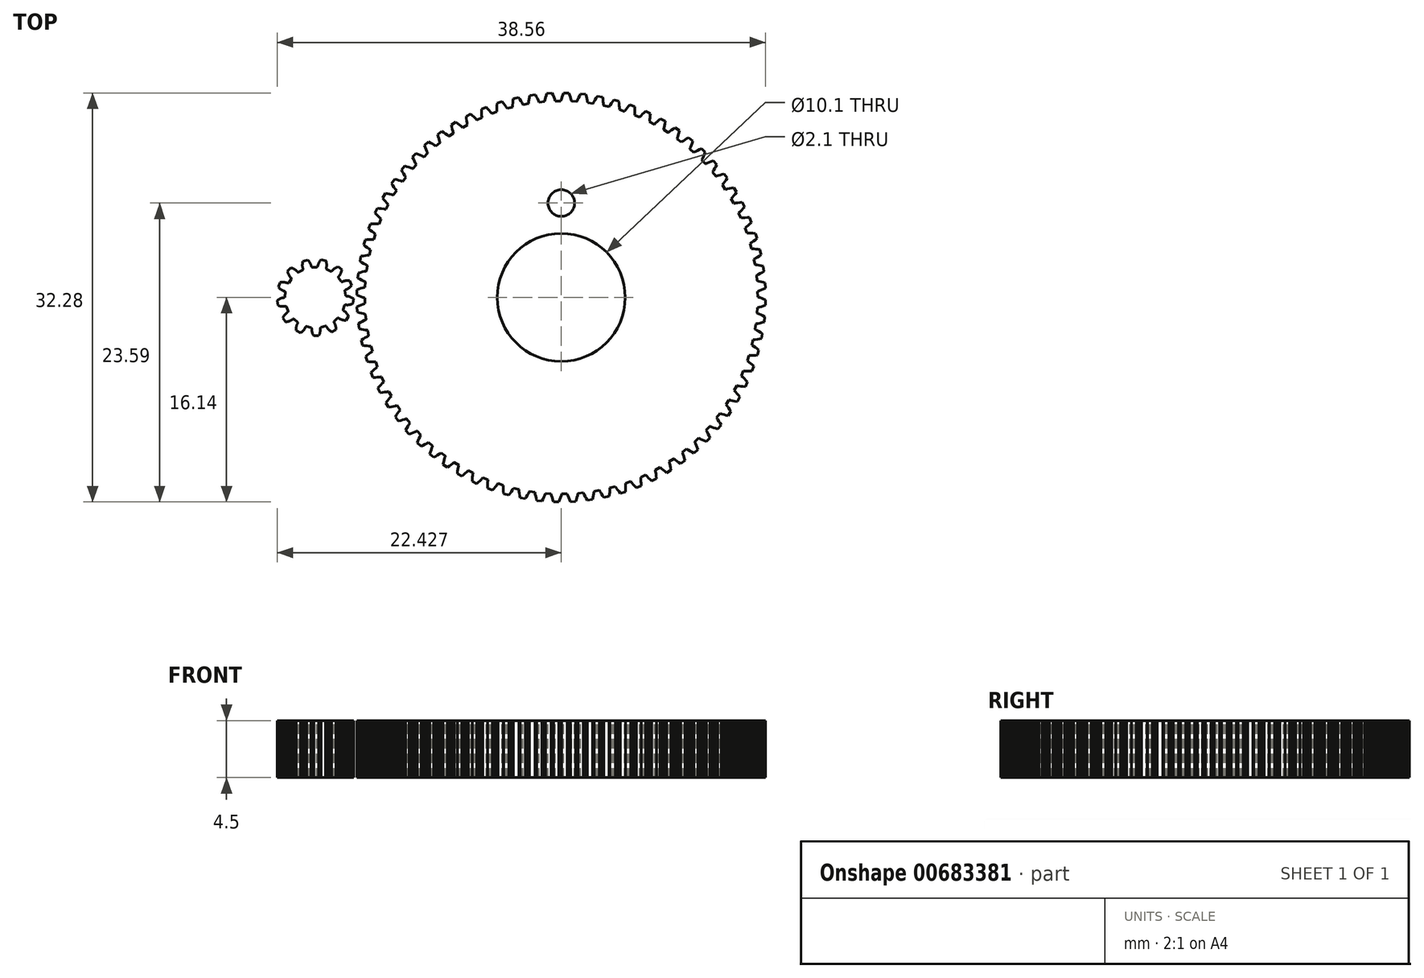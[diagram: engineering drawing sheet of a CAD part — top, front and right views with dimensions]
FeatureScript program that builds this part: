
annotation { "Feature Type Name" : "Feature", "Feature Type Description" : "" }
export const myFeature = defineFeature(function(context is Context, id is Id, definition is map)
    precondition{}
    {
        {
            var Q0;
            Q0=qCreatedBy(makeId("Top.planeOp"),FACE);
            var sketch = newSketch(context, id + "F0", { "sketchPlane" : qUnion([Q0])});
            skLineSegment(sketch, "E0", {"start": v(-13.88, 0.17) * mm, "end": v(-13.87, 0.14) * mm});
            skLineSegment(sketch, "E1", {"start": v(-13.87, 0.14) * mm, "end": v(-13.86, 0.13) * mm});
            skLineSegment(sketch, "E2", {"start": v(-13.86, 0.13) * mm, "end": v(-13.85, 0.12) * mm});
            skLineSegment(sketch, "E3", {"start": v(-13.85, 0.12) * mm, "end": v(-13.84, 0.12) * mm});
            skLineSegment(sketch, "E4", {"start": v(-13.84, 0.12) * mm, "end": v(-13.83, 0.11) * mm});
            skLineSegment(sketch, "E5", {"start": v(-13.83, 0.11) * mm, "end": v(-13.82, 0.1) * mm});
            skLineSegment(sketch, "E6", {"start": v(-13.82, 0.1) * mm, "end": v(-13.8, 0.1) * mm});
            skLineSegment(sketch, "E7", {"start": v(-13.8, 0.1) * mm, "end": v(-13.78, 0.1) * mm});
            skLineSegment(sketch, "E8", {"start": v(-13.78, 0.1) * mm, "end": v(-13.76, 0.1) * mm});
            skLineSegment(sketch, "E9", {"start": v(-13.76, 0.1) * mm, "end": v(-13.71, 0.1) * mm});
            skLineSegment(sketch, "E10", {"start": v(-13.71, 0.1) * mm, "end": v(-13.67, 0.1) * mm});
            skLineSegment(sketch, "E11", {"start": v(-13.67, 0.1) * mm, "end": v(-13.63, 0.08) * mm});
            skLineSegment(sketch, "E12", {"start": v(-13.63, 0.08) * mm, "end": v(-13.59, 0.07) * mm});
            skLineSegment(sketch, "E13", {"start": v(-13.59, 0.07) * mm, "end": v(-13.54, 0.06) * mm});
            skLineSegment(sketch, "E14", {"start": v(-13.54, 0.06) * mm, "end": v(-13.5, 0.04) * mm});
            skLineSegment(sketch, "E15", {"start": v(-13.5, 0.04) * mm, "end": v(-13.46, 0.02) * mm});
            skLineSegment(sketch, "E16", {"start": v(-13.46, 0.02) * mm, "end": v(-13.42, 0) * mm});
            skLineSegment(sketch, "E17", {"start": v(-13.42, 0) * mm, "end": v(-13.38, -0.02) * mm});
            skLineSegment(sketch, "E18", {"start": v(-13.38, -0.02) * mm, "end": v(-13.34, -0.04) * mm});
            skLineSegment(sketch, "E19", {"start": v(-13.34, -0.04) * mm, "end": v(-13.3, -0.07) * mm});
            skLineSegment(sketch, "E20", {"start": v(-13.3, -0.07) * mm, "end": v(-13.25, -0.1) * mm});
            skLineSegment(sketch, "E21", {"start": v(-13.25, -0.1) * mm, "end": v(-13.3, -0.49) * mm});
            skLineSegment(sketch, "E22", {"start": v(-13.3, -0.49) * mm, "end": v(-13.34, -0.5) * mm});
            skLineSegment(sketch, "E23", {"start": v(-13.34, -0.5) * mm, "end": v(-13.38, -0.52) * mm});
            skLineSegment(sketch, "E24", {"start": v(-13.38, -0.52) * mm, "end": v(-13.43, -0.54) * mm});
            skLineSegment(sketch, "E25", {"start": v(-13.43, -0.54) * mm, "end": v(-13.47, -0.55) * mm});
            skLineSegment(sketch, "E26", {"start": v(-13.47, -0.55) * mm, "end": v(-13.52, -0.56) * mm});
            skLineSegment(sketch, "E27", {"start": v(-13.52, -0.56) * mm, "end": v(-13.56, -0.57) * mm});
            skLineSegment(sketch, "E28", {"start": v(-13.56, -0.57) * mm, "end": v(-13.6, -0.58) * mm});
            skLineSegment(sketch, "E29", {"start": v(-13.6, -0.58) * mm, "end": v(-13.65, -0.59) * mm});
            skLineSegment(sketch, "E30", {"start": v(-13.65, -0.59) * mm, "end": v(-13.7, -0.6) * mm});
            skLineSegment(sketch, "E31", {"start": v(-13.7, -0.6) * mm, "end": v(-13.74, -0.6) * mm});
            skLineSegment(sketch, "E32", {"start": v(-13.74, -0.6) * mm, "end": v(-13.78, -0.59) * mm});
            skLineSegment(sketch, "E33", {"start": v(-13.78, -0.59) * mm, "end": v(-13.82, -0.58) * mm});
            skLineSegment(sketch, "E34", {"start": v(-13.82, -0.58) * mm, "end": v(-13.84, -0.58) * mm});
            skLineSegment(sketch, "E35", {"start": v(-13.84, -0.58) * mm, "end": v(-13.86, -0.58) * mm});
            skLineSegment(sketch, "E36", {"start": v(-13.86, -0.58) * mm, "end": v(-13.89, -0.58) * mm});
            skLineSegment(sketch, "E37", {"start": v(-13.89, -0.58) * mm, "end": v(-13.9, -0.58) * mm});
            skLineSegment(sketch, "E38", {"start": v(-13.9, -0.58) * mm, "end": v(-13.9, -0.58) * mm});
            skLineSegment(sketch, "E39", {"start": v(-13.9, -0.58) * mm, "end": v(-13.92, -0.59) * mm});
            skLineSegment(sketch, "E40", {"start": v(-13.92, -0.59) * mm, "end": v(-13.93, -0.6) * mm});
            skLineSegment(sketch, "E41", {"start": v(-13.93, -0.6) * mm, "end": v(-13.94, -0.6) * mm});
            skLineSegment(sketch, "E42", {"start": v(-13.94, -0.6) * mm, "end": v(-13.96, -0.62) * mm});
            skLineSegment(sketch, "E43", {"start": v(-13.96, -0.62) * mm, "end": v(-14.08, -0.96) * mm});
            skLineSegment(sketch, "E44", {"start": v(-14.08, -0.96) * mm, "end": v(-14.08, -1) * mm});
            skLineSegment(sketch, "E45", {"start": v(-14.08, -1) * mm, "end": v(-14.08, -1) * mm});
            skLineSegment(sketch, "E46", {"start": v(-14.08, -1) * mm, "end": v(-14.07, -1.02) * mm});
            skLineSegment(sketch, "E47", {"start": v(-14.07, -1.02) * mm, "end": v(-14.06, -1.03) * mm});
            skLineSegment(sketch, "E48", {"start": v(-14.06, -1.03) * mm, "end": v(-14.06, -1.03) * mm});
            skLineSegment(sketch, "E49", {"start": v(-14.06, -1.03) * mm, "end": v(-14.05, -1.04) * mm});
            skLineSegment(sketch, "E50", {"start": v(-14.05, -1.04) * mm, "end": v(-14.03, -1.06) * mm});
            skLineSegment(sketch, "E51", {"start": v(-14.03, -1.06) * mm, "end": v(-14.01, -1.07) * mm});
            skLineSegment(sketch, "E52", {"start": v(-14.01, -1.07) * mm, "end": v(-14, -1.08) * mm});
            skLineSegment(sketch, "E53", {"start": v(-14, -1.08) * mm, "end": v(-13.96, -1.1) * mm});
            skLineSegment(sketch, "E54", {"start": v(-13.96, -1.1) * mm, "end": v(-13.93, -1.13) * mm});
            skLineSegment(sketch, "E55", {"start": v(-13.93, -1.13) * mm, "end": v(-13.9, -1.15) * mm});
            skLineSegment(sketch, "E56", {"start": v(-13.9, -1.15) * mm, "end": v(-13.86, -1.18) * mm});
            skLineSegment(sketch, "E57", {"start": v(-13.86, -1.18) * mm, "end": v(-13.83, -1.22) * mm});
            skLineSegment(sketch, "E58", {"start": v(-13.83, -1.22) * mm, "end": v(-13.8, -1.25) * mm});
            skLineSegment(sketch, "E59", {"start": v(-13.8, -1.25) * mm, "end": v(-13.77, -1.29) * mm});
            skLineSegment(sketch, "E60", {"start": v(-13.77, -1.29) * mm, "end": v(-13.74, -1.32) * mm});
            skLineSegment(sketch, "E61", {"start": v(-13.74, -1.32) * mm, "end": v(-13.72, -1.36) * mm});
            skLineSegment(sketch, "E62", {"start": v(-13.72, -1.36) * mm, "end": v(-13.7, -1.4) * mm});
            skLineSegment(sketch, "E63", {"start": v(-13.7, -1.4) * mm, "end": v(-13.67, -1.44) * mm});
            skLineSegment(sketch, "E64", {"start": v(-13.67, -1.44) * mm, "end": v(-13.64, -1.49) * mm});
            skLineSegment(sketch, "E65", {"start": v(-13.64, -1.49) * mm, "end": v(-13.86, -1.82) * mm});
            skLineSegment(sketch, "E66", {"start": v(-13.86, -1.82) * mm, "end": v(-13.9, -1.81) * mm});
            skLineSegment(sketch, "E67", {"start": v(-13.9, -1.81) * mm, "end": v(-13.96, -1.8) * mm});
            skLineSegment(sketch, "E68", {"start": v(-13.96, -1.8) * mm, "end": v(-14, -1.8) * mm});
            skLineSegment(sketch, "E69", {"start": v(-14, -1.8) * mm, "end": v(-14.05, -1.79) * mm});
            skLineSegment(sketch, "E70", {"start": v(-14.05, -1.79) * mm, "end": v(-14.1, -1.78) * mm});
            skLineSegment(sketch, "E71", {"start": v(-14.1, -1.78) * mm, "end": v(-14.14, -1.77) * mm});
            skLineSegment(sketch, "E72", {"start": v(-14.14, -1.77) * mm, "end": v(-14.18, -1.75) * mm});
            skLineSegment(sketch, "E73", {"start": v(-14.18, -1.75) * mm, "end": v(-14.22, -1.74) * mm});
            skLineSegment(sketch, "E74", {"start": v(-14.22, -1.74) * mm, "end": v(-14.26, -1.72) * mm});
            skLineSegment(sketch, "E75", {"start": v(-14.26, -1.72) * mm, "end": v(-14.3, -1.7) * mm});
            skLineSegment(sketch, "E76", {"start": v(-14.3, -1.7) * mm, "end": v(-14.34, -1.68) * mm});
            skLineSegment(sketch, "E77", {"start": v(-14.34, -1.68) * mm, "end": v(-14.37, -1.65) * mm});
            skLineSegment(sketch, "E78", {"start": v(-14.37, -1.65) * mm, "end": v(-14.39, -1.64) * mm});
            skLineSegment(sketch, "E79", {"start": v(-14.39, -1.64) * mm, "end": v(-14.4, -1.63) * mm});
            skLineSegment(sketch, "E80", {"start": v(-14.4, -1.63) * mm, "end": v(-14.43, -1.62) * mm});
            skLineSegment(sketch, "E81", {"start": v(-14.43, -1.62) * mm, "end": v(-14.44, -1.62) * mm});
            skLineSegment(sketch, "E82", {"start": v(-14.44, -1.62) * mm, "end": v(-14.45, -1.61) * mm});
            skLineSegment(sketch, "E83", {"start": v(-14.45, -1.61) * mm, "end": v(-14.46, -1.61) * mm});
            skLineSegment(sketch, "E84", {"start": v(-14.46, -1.61) * mm, "end": v(-14.47, -1.61) * mm});
            skLineSegment(sketch, "E85", {"start": v(-14.47, -1.61) * mm, "end": v(-14.49, -1.61) * mm});
            skLineSegment(sketch, "E86", {"start": v(-14.49, -1.61) * mm, "end": v(-14.51, -1.62) * mm});
            skLineSegment(sketch, "E87", {"start": v(-14.51, -1.62) * mm, "end": v(-14.78, -1.87) * mm});
            skLineSegment(sketch, "E88", {"start": v(-14.78, -1.87) * mm, "end": v(-14.8, -1.9) * mm});
            skLineSegment(sketch, "E89", {"start": v(-14.8, -1.9) * mm, "end": v(-14.8, -1.9) * mm});
            skLineSegment(sketch, "E90", {"start": v(-14.8, -1.9) * mm, "end": v(-14.8, -1.92) * mm});
            skLineSegment(sketch, "E91", {"start": v(-14.8, -1.92) * mm, "end": v(-14.8, -1.93) * mm});
            skLineSegment(sketch, "E92", {"start": v(-14.8, -1.93) * mm, "end": v(-14.8, -1.95) * mm});
            skLineSegment(sketch, "E93", {"start": v(-14.8, -1.95) * mm, "end": v(-14.79, -1.96) * mm});
            skLineSegment(sketch, "E94", {"start": v(-14.79, -1.96) * mm, "end": v(-14.78, -1.98) * mm});
            skLineSegment(sketch, "E95", {"start": v(-14.78, -1.98) * mm, "end": v(-14.77, -2) * mm});
            skLineSegment(sketch, "E96", {"start": v(-14.77, -2) * mm, "end": v(-14.76, -2.01) * mm});
            skLineSegment(sketch, "E97", {"start": v(-14.76, -2.01) * mm, "end": v(-14.74, -2.05) * mm});
            skLineSegment(sketch, "E98", {"start": v(-14.74, -2.05) * mm, "end": v(-14.72, -2.09) * mm});
            skLineSegment(sketch, "E99", {"start": v(-14.72, -2.09) * mm, "end": v(-14.7, -2.13) * mm});
            skLineSegment(sketch, "E100", {"start": v(-14.7, -2.13) * mm, "end": v(-14.69, -2.17) * mm});
            skLineSegment(sketch, "E101", {"start": v(-14.69, -2.17) * mm, "end": v(-14.67, -2.21) * mm});
            skLineSegment(sketch, "E102", {"start": v(-14.67, -2.21) * mm, "end": v(-14.66, -2.26) * mm});
            skLineSegment(sketch, "E103", {"start": v(-14.66, -2.26) * mm, "end": v(-14.66, -2.3) * mm});
            skLineSegment(sketch, "E104", {"start": v(-14.66, -2.3) * mm, "end": v(-14.65, -2.35) * mm});
            skLineSegment(sketch, "E105", {"start": v(-14.65, -2.35) * mm, "end": v(-14.64, -2.4) * mm});
            skLineSegment(sketch, "E106", {"start": v(-14.64, -2.4) * mm, "end": v(-14.64, -2.44) * mm});
            skLineSegment(sketch, "E107", {"start": v(-14.64, -2.44) * mm, "end": v(-14.64, -2.49) * mm});
            skLineSegment(sketch, "E108", {"start": v(-14.64, -2.49) * mm, "end": v(-14.64, -2.54) * mm});
            skLineSegment(sketch, "E109", {"start": v(-14.64, -2.54) * mm, "end": v(-14.98, -2.73) * mm});
            skLineSegment(sketch, "E110", {"start": v(-14.98, -2.73) * mm, "end": v(-15.02, -2.7) * mm});
            skLineSegment(sketch, "E111", {"start": v(-15.02, -2.7) * mm, "end": v(-15.06, -2.67) * mm});
            skLineSegment(sketch, "E112", {"start": v(-15.06, -2.67) * mm, "end": v(-15.1, -2.65) * mm});
            skLineSegment(sketch, "E113", {"start": v(-15.1, -2.65) * mm, "end": v(-15.13, -2.62) * mm});
            skLineSegment(sketch, "E114", {"start": v(-15.13, -2.62) * mm, "end": v(-15.17, -2.59) * mm});
            skLineSegment(sketch, "E115", {"start": v(-15.17, -2.59) * mm, "end": v(-15.2, -2.56) * mm});
            skLineSegment(sketch, "E116", {"start": v(-15.2, -2.56) * mm, "end": v(-15.24, -2.52) * mm});
            skLineSegment(sketch, "E117", {"start": v(-15.24, -2.52) * mm, "end": v(-15.27, -2.5) * mm});
            skLineSegment(sketch, "E118", {"start": v(-15.27, -2.5) * mm, "end": v(-15.3, -2.46) * mm});
            skLineSegment(sketch, "E119", {"start": v(-15.3, -2.46) * mm, "end": v(-15.32, -2.42) * mm});
            skLineSegment(sketch, "E120", {"start": v(-15.32, -2.42) * mm, "end": v(-15.34, -2.38) * mm});
            skLineSegment(sketch, "E121", {"start": v(-15.34, -2.38) * mm, "end": v(-15.36, -2.35) * mm});
            skLineSegment(sketch, "E122", {"start": v(-15.36, -2.35) * mm, "end": v(-15.37, -2.33) * mm});
            skLineSegment(sketch, "E123", {"start": v(-15.37, -2.33) * mm, "end": v(-15.38, -2.31) * mm});
            skLineSegment(sketch, "E124", {"start": v(-15.38, -2.31) * mm, "end": v(-15.4, -2.3) * mm});
            skLineSegment(sketch, "E125", {"start": v(-15.4, -2.3) * mm, "end": v(-15.4, -2.28) * mm});
            skLineSegment(sketch, "E126", {"start": v(-15.4, -2.28) * mm, "end": v(-15.4, -2.28) * mm});
            skLineSegment(sketch, "E127", {"start": v(-15.4, -2.28) * mm, "end": v(-15.42, -2.27) * mm});
            skLineSegment(sketch, "E128", {"start": v(-15.42, -2.27) * mm, "end": v(-15.43, -2.26) * mm});
            skLineSegment(sketch, "E129", {"start": v(-15.43, -2.26) * mm, "end": v(-15.44, -2.26) * mm});
            skLineSegment(sketch, "E130", {"start": v(-15.44, -2.26) * mm, "end": v(-15.47, -2.25) * mm});
            skLineSegment(sketch, "E131", {"start": v(-15.47, -2.25) * mm, "end": v(-15.82, -2.35) * mm});
            skLineSegment(sketch, "E132", {"start": v(-15.82, -2.35) * mm, "end": v(-15.84, -2.36) * mm});
            skLineSegment(sketch, "E133", {"start": v(-15.84, -2.36) * mm, "end": v(-15.85, -2.38) * mm});
            skLineSegment(sketch, "E134", {"start": v(-15.85, -2.38) * mm, "end": v(-15.86, -2.39) * mm});
            skLineSegment(sketch, "E135", {"start": v(-15.86, -2.39) * mm, "end": v(-15.86, -2.4) * mm});
            skLineSegment(sketch, "E136", {"start": v(-15.86, -2.4) * mm, "end": v(-15.86, -2.41) * mm});
            skLineSegment(sketch, "E137", {"start": v(-15.86, -2.41) * mm, "end": v(-15.87, -2.42) * mm});
            skLineSegment(sketch, "E138", {"start": v(-15.87, -2.42) * mm, "end": v(-15.87, -2.44) * mm});
            skLineSegment(sketch, "E139", {"start": v(-15.87, -2.44) * mm, "end": v(-15.87, -2.46) * mm});
            skLineSegment(sketch, "E140", {"start": v(-15.87, -2.46) * mm, "end": v(-15.87, -2.49) * mm});
            skLineSegment(sketch, "E141", {"start": v(-15.87, -2.49) * mm, "end": v(-15.87, -2.53) * mm});
            skLineSegment(sketch, "E142", {"start": v(-15.87, -2.53) * mm, "end": v(-15.87, -2.57) * mm});
            skLineSegment(sketch, "E143", {"start": v(-15.87, -2.57) * mm, "end": v(-15.87, -2.61) * mm});
            skLineSegment(sketch, "E144", {"start": v(-15.87, -2.61) * mm, "end": v(-15.88, -2.66) * mm});
            skLineSegment(sketch, "E145", {"start": v(-15.88, -2.66) * mm, "end": v(-15.89, -2.7) * mm});
            skLineSegment(sketch, "E146", {"start": v(-15.89, -2.7) * mm, "end": v(-15.9, -2.74) * mm});
            skLineSegment(sketch, "E147", {"start": v(-15.9, -2.74) * mm, "end": v(-15.9, -2.79) * mm});
            skLineSegment(sketch, "E148", {"start": v(-15.9, -2.79) * mm, "end": v(-15.92, -2.83) * mm});
            skLineSegment(sketch, "E149", {"start": v(-15.92, -2.83) * mm, "end": v(-15.94, -2.88) * mm});
            skLineSegment(sketch, "E150", {"start": v(-15.94, -2.88) * mm, "end": v(-15.96, -2.92) * mm});
            skLineSegment(sketch, "E151", {"start": v(-15.96, -2.92) * mm, "end": v(-15.98, -2.96) * mm});
            skLineSegment(sketch, "E152", {"start": v(-15.98, -2.96) * mm, "end": v(-16, -3) * mm});
            skLineSegment(sketch, "E153", {"start": v(-16, -3) * mm, "end": v(-16.4, -3.02) * mm});
            skLineSegment(sketch, "E154", {"start": v(-16.4, -3.02) * mm, "end": v(-16.42, -2.97) * mm});
            skLineSegment(sketch, "E155", {"start": v(-16.42, -2.97) * mm, "end": v(-16.44, -2.93) * mm});
            skLineSegment(sketch, "E156", {"start": v(-16.44, -2.93) * mm, "end": v(-16.46, -2.89) * mm});
            skLineSegment(sketch, "E157", {"start": v(-16.46, -2.89) * mm, "end": v(-16.48, -2.85) * mm});
            skLineSegment(sketch, "E158", {"start": v(-16.48, -2.85) * mm, "end": v(-16.5, -2.8) * mm});
            skLineSegment(sketch, "E159", {"start": v(-16.5, -2.8) * mm, "end": v(-16.51, -2.76) * mm});
            skLineSegment(sketch, "E160", {"start": v(-16.51, -2.76) * mm, "end": v(-16.53, -2.72) * mm});
            skLineSegment(sketch, "E161", {"start": v(-16.53, -2.72) * mm, "end": v(-16.54, -2.67) * mm});
            skLineSegment(sketch, "E162", {"start": v(-16.54, -2.67) * mm, "end": v(-16.55, -2.63) * mm});
            skLineSegment(sketch, "E163", {"start": v(-16.55, -2.63) * mm, "end": v(-16.55, -2.59) * mm});
            skLineSegment(sketch, "E164", {"start": v(-16.55, -2.59) * mm, "end": v(-16.56, -2.54) * mm});
            skLineSegment(sketch, "E165", {"start": v(-16.56, -2.54) * mm, "end": v(-16.55, -2.5) * mm});
            skLineSegment(sketch, "E166", {"start": v(-16.55, -2.5) * mm, "end": v(-16.55, -2.48) * mm});
            skLineSegment(sketch, "E167", {"start": v(-16.55, -2.48) * mm, "end": v(-16.56, -2.46) * mm});
            skLineSegment(sketch, "E168", {"start": v(-16.56, -2.46) * mm, "end": v(-16.56, -2.44) * mm});
            skLineSegment(sketch, "E169", {"start": v(-16.56, -2.44) * mm, "end": v(-16.56, -2.43) * mm});
            skLineSegment(sketch, "E170", {"start": v(-16.56, -2.43) * mm, "end": v(-16.56, -2.42) * mm});
            skLineSegment(sketch, "E171", {"start": v(-16.56, -2.42) * mm, "end": v(-16.57, -2.4) * mm});
            skLineSegment(sketch, "E172", {"start": v(-16.57, -2.4) * mm, "end": v(-16.58, -2.4) * mm});
            skLineSegment(sketch, "E173", {"start": v(-16.58, -2.4) * mm, "end": v(-16.58, -2.38) * mm});
            skLineSegment(sketch, "E174", {"start": v(-16.58, -2.38) * mm, "end": v(-16.6, -2.37) * mm});
            skLineSegment(sketch, "E175", {"start": v(-16.6, -2.37) * mm, "end": v(-16.96, -2.3) * mm});
            skLineSegment(sketch, "E176", {"start": v(-16.96, -2.3) * mm, "end": v(-17, -2.3) * mm});
            skLineSegment(sketch, "E177", {"start": v(-17, -2.3) * mm, "end": v(-17, -2.3) * mm});
            skLineSegment(sketch, "E178", {"start": v(-17, -2.3) * mm, "end": v(-17.02, -2.3) * mm});
            skLineSegment(sketch, "E179", {"start": v(-17.02, -2.3) * mm, "end": v(-17.02, -2.32) * mm});
            skLineSegment(sketch, "E180", {"start": v(-17.02, -2.32) * mm, "end": v(-17.03, -2.32) * mm});
            skLineSegment(sketch, "E181", {"start": v(-17.03, -2.32) * mm, "end": v(-17.04, -2.33) * mm});
            skLineSegment(sketch, "E182", {"start": v(-17.04, -2.33) * mm, "end": v(-17.05, -2.35) * mm});
            skLineSegment(sketch, "E183", {"start": v(-17.05, -2.35) * mm, "end": v(-17.06, -2.37) * mm});
            skLineSegment(sketch, "E184", {"start": v(-17.06, -2.37) * mm, "end": v(-17.07, -2.39) * mm});
            skLineSegment(sketch, "E185", {"start": v(-17.07, -2.39) * mm, "end": v(-17.09, -2.43) * mm});
            skLineSegment(sketch, "E186", {"start": v(-17.09, -2.43) * mm, "end": v(-17.1, -2.46) * mm});
            skLineSegment(sketch, "E187", {"start": v(-17.1, -2.46) * mm, "end": v(-17.13, -2.5) * mm});
            skLineSegment(sketch, "E188", {"start": v(-17.13, -2.5) * mm, "end": v(-17.16, -2.54) * mm});
            skLineSegment(sketch, "E189", {"start": v(-17.16, -2.54) * mm, "end": v(-17.18, -2.57) * mm});
            skLineSegment(sketch, "E190", {"start": v(-17.18, -2.57) * mm, "end": v(-17.21, -2.6) * mm});
            skLineSegment(sketch, "E191", {"start": v(-17.21, -2.6) * mm, "end": v(-17.25, -2.64) * mm});
            skLineSegment(sketch, "E192", {"start": v(-17.25, -2.64) * mm, "end": v(-17.28, -2.67) * mm});
            skLineSegment(sketch, "E193", {"start": v(-17.28, -2.67) * mm, "end": v(-17.32, -2.7) * mm});
            skLineSegment(sketch, "E194", {"start": v(-17.32, -2.7) * mm, "end": v(-17.35, -2.73) * mm});
            skLineSegment(sketch, "E195", {"start": v(-17.35, -2.73) * mm, "end": v(-17.4, -2.76) * mm});
            skLineSegment(sketch, "E196", {"start": v(-17.4, -2.76) * mm, "end": v(-17.43, -2.79) * mm});
            skLineSegment(sketch, "E197", {"start": v(-17.43, -2.79) * mm, "end": v(-17.78, -2.61) * mm});
            skLineSegment(sketch, "E198", {"start": v(-17.78, -2.61) * mm, "end": v(-17.78, -2.57) * mm});
            skLineSegment(sketch, "E199", {"start": v(-17.78, -2.57) * mm, "end": v(-17.78, -2.52) * mm});
            skLineSegment(sketch, "E200", {"start": v(-17.78, -2.52) * mm, "end": v(-17.78, -2.47) * mm});
            skLineSegment(sketch, "E201", {"start": v(-17.78, -2.47) * mm, "end": v(-17.78, -2.42) * mm});
            skLineSegment(sketch, "E202", {"start": v(-17.78, -2.42) * mm, "end": v(-17.77, -2.38) * mm});
            skLineSegment(sketch, "E203", {"start": v(-17.77, -2.38) * mm, "end": v(-17.77, -2.33) * mm});
            skLineSegment(sketch, "E204", {"start": v(-17.77, -2.33) * mm, "end": v(-17.76, -2.29) * mm});
            skLineSegment(sketch, "E205", {"start": v(-17.76, -2.29) * mm, "end": v(-17.75, -2.24) * mm});
            skLineSegment(sketch, "E206", {"start": v(-17.75, -2.24) * mm, "end": v(-17.74, -2.2) * mm});
            skLineSegment(sketch, "E207", {"start": v(-17.74, -2.2) * mm, "end": v(-17.72, -2.16) * mm});
            skLineSegment(sketch, "E208", {"start": v(-17.72, -2.16) * mm, "end": v(-17.7, -2.12) * mm});
            skLineSegment(sketch, "E209", {"start": v(-17.7, -2.12) * mm, "end": v(-17.68, -2.08) * mm});
            skLineSegment(sketch, "E210", {"start": v(-17.68, -2.08) * mm, "end": v(-17.67, -2.07) * mm});
            skLineSegment(sketch, "E211", {"start": v(-17.67, -2.07) * mm, "end": v(-17.67, -2.05) * mm});
            skLineSegment(sketch, "E212", {"start": v(-17.67, -2.05) * mm, "end": v(-17.66, -2.03) * mm});
            skLineSegment(sketch, "E213", {"start": v(-17.66, -2.03) * mm, "end": v(-17.66, -2.02) * mm});
            skLineSegment(sketch, "E214", {"start": v(-17.66, -2.02) * mm, "end": v(-17.65, -2) * mm});
            skLineSegment(sketch, "E215", {"start": v(-17.65, -2) * mm, "end": v(-17.65, -2) * mm});
            skLineSegment(sketch, "E216", {"start": v(-17.65, -2) * mm, "end": v(-17.65, -1.98) * mm});
            skLineSegment(sketch, "E217", {"start": v(-17.65, -1.98) * mm, "end": v(-17.66, -1.96) * mm});
            skLineSegment(sketch, "E218", {"start": v(-17.66, -1.96) * mm, "end": v(-17.67, -1.94) * mm});
            skLineSegment(sketch, "E219", {"start": v(-17.67, -1.94) * mm, "end": v(-17.95, -1.7) * mm});
            skLineSegment(sketch, "E220", {"start": v(-17.95, -1.7) * mm, "end": v(-17.97, -1.7) * mm});
            skLineSegment(sketch, "E221", {"start": v(-17.97, -1.7) * mm, "end": v(-17.99, -1.7) * mm});
            skLineSegment(sketch, "E222", {"start": v(-17.99, -1.7) * mm, "end": v(-18, -1.7) * mm});
            skLineSegment(sketch, "E223", {"start": v(-18, -1.7) * mm, "end": v(-18.01, -1.7) * mm});
            skLineSegment(sketch, "E224", {"start": v(-18.01, -1.7) * mm, "end": v(-18.02, -1.7) * mm});
            skLineSegment(sketch, "E225", {"start": v(-18.02, -1.7) * mm, "end": v(-18.03, -1.7) * mm});
            skLineSegment(sketch, "E226", {"start": v(-18.03, -1.7) * mm, "end": v(-18.05, -1.72) * mm});
            skLineSegment(sketch, "E227", {"start": v(-18.05, -1.72) * mm, "end": v(-18.07, -1.73) * mm});
            skLineSegment(sketch, "E228", {"start": v(-18.07, -1.73) * mm, "end": v(-18.09, -1.74) * mm});
            skLineSegment(sketch, "E229", {"start": v(-18.09, -1.74) * mm, "end": v(-18.12, -1.77) * mm});
            skLineSegment(sketch, "E230", {"start": v(-18.12, -1.77) * mm, "end": v(-18.16, -1.8) * mm});
            skLineSegment(sketch, "E231", {"start": v(-18.16, -1.8) * mm, "end": v(-18.2, -1.82) * mm});
            skLineSegment(sketch, "E232", {"start": v(-18.2, -1.82) * mm, "end": v(-18.23, -1.83) * mm});
            skLineSegment(sketch, "E233", {"start": v(-18.23, -1.83) * mm, "end": v(-18.27, -1.85) * mm});
            skLineSegment(sketch, "E234", {"start": v(-18.27, -1.85) * mm, "end": v(-18.32, -1.87) * mm});
            skLineSegment(sketch, "E235", {"start": v(-18.32, -1.87) * mm, "end": v(-18.36, -1.88) * mm});
            skLineSegment(sketch, "E236", {"start": v(-18.36, -1.88) * mm, "end": v(-18.4, -1.9) * mm});
            skLineSegment(sketch, "E237", {"start": v(-18.4, -1.9) * mm, "end": v(-18.45, -1.9) * mm});
            skLineSegment(sketch, "E238", {"start": v(-18.45, -1.9) * mm, "end": v(-18.5, -1.91) * mm});
            skLineSegment(sketch, "E239", {"start": v(-18.5, -1.91) * mm, "end": v(-18.55, -1.92) * mm});
            skLineSegment(sketch, "E240", {"start": v(-18.55, -1.92) * mm, "end": v(-18.6, -1.93) * mm});
            skLineSegment(sketch, "E241", {"start": v(-18.6, -1.93) * mm, "end": v(-18.82, -1.61) * mm});
            skLineSegment(sketch, "E242", {"start": v(-18.82, -1.61) * mm, "end": v(-18.8, -1.57) * mm});
            skLineSegment(sketch, "E243", {"start": v(-18.8, -1.57) * mm, "end": v(-18.78, -1.53) * mm});
            skLineSegment(sketch, "E244", {"start": v(-18.78, -1.53) * mm, "end": v(-18.76, -1.48) * mm});
            skLineSegment(sketch, "E245", {"start": v(-18.76, -1.48) * mm, "end": v(-18.73, -1.44) * mm});
            skLineSegment(sketch, "E246", {"start": v(-18.73, -1.44) * mm, "end": v(-18.7, -1.4) * mm});
            skLineSegment(sketch, "E247", {"start": v(-18.7, -1.4) * mm, "end": v(-18.68, -1.37) * mm});
            skLineSegment(sketch, "E248", {"start": v(-18.68, -1.37) * mm, "end": v(-18.65, -1.33) * mm});
            skLineSegment(sketch, "E249", {"start": v(-18.65, -1.33) * mm, "end": v(-18.62, -1.3) * mm});
            skLineSegment(sketch, "E250", {"start": v(-18.62, -1.3) * mm, "end": v(-18.6, -1.27) * mm});
            skLineSegment(sketch, "E251", {"start": v(-18.6, -1.27) * mm, "end": v(-18.56, -1.24) * mm});
            skLineSegment(sketch, "E252", {"start": v(-18.56, -1.24) * mm, "end": v(-18.53, -1.21) * mm});
            skLineSegment(sketch, "E253", {"start": v(-18.53, -1.21) * mm, "end": v(-18.5, -1.19) * mm});
            skLineSegment(sketch, "E254", {"start": v(-18.5, -1.19) * mm, "end": v(-18.47, -1.18) * mm});
            skLineSegment(sketch, "E255", {"start": v(-18.47, -1.18) * mm, "end": v(-18.46, -1.16) * mm});
            skLineSegment(sketch, "E256", {"start": v(-18.46, -1.16) * mm, "end": v(-18.44, -1.15) * mm});
            skLineSegment(sketch, "E257", {"start": v(-18.44, -1.15) * mm, "end": v(-18.43, -1.14) * mm});
            skLineSegment(sketch, "E258", {"start": v(-18.43, -1.14) * mm, "end": v(-18.43, -1.13) * mm});
            skLineSegment(sketch, "E259", {"start": v(-18.43, -1.13) * mm, "end": v(-18.42, -1.12) * mm});
            skLineSegment(sketch, "E260", {"start": v(-18.42, -1.12) * mm, "end": v(-18.41, -1.11) * mm});
            skLineSegment(sketch, "E261", {"start": v(-18.41, -1.11) * mm, "end": v(-18.4, -1.1) * mm});
            skLineSegment(sketch, "E262", {"start": v(-18.4, -1.1) * mm, "end": v(-18.41, -1.07) * mm});
            skLineSegment(sketch, "E263", {"start": v(-18.41, -1.07) * mm, "end": v(-18.55, -0.73) * mm});
            skLineSegment(sketch, "E264", {"start": v(-18.55, -0.73) * mm, "end": v(-18.57, -0.7) * mm});
            skLineSegment(sketch, "E265", {"start": v(-18.57, -0.7) * mm, "end": v(-18.58, -0.7) * mm});
            skLineSegment(sketch, "E266", {"start": v(-18.58, -0.7) * mm, "end": v(-18.6, -0.7) * mm});
            skLineSegment(sketch, "E267", {"start": v(-18.6, -0.7) * mm, "end": v(-18.6, -0.7) * mm});
            skLineSegment(sketch, "E268", {"start": v(-18.6, -0.7) * mm, "end": v(-18.62, -0.7) * mm});
            skLineSegment(sketch, "E269", {"start": v(-18.62, -0.7) * mm, "end": v(-18.63, -0.7) * mm});
            skLineSegment(sketch, "E270", {"start": v(-18.63, -0.7) * mm, "end": v(-18.65, -0.7) * mm});
            skLineSegment(sketch, "E271", {"start": v(-18.65, -0.7) * mm, "end": v(-18.67, -0.7) * mm});
            skLineSegment(sketch, "E272", {"start": v(-18.67, -0.7) * mm, "end": v(-18.7, -0.7) * mm});
            skLineSegment(sketch, "E273", {"start": v(-18.7, -0.7) * mm, "end": v(-18.73, -0.7) * mm});
            skLineSegment(sketch, "E274", {"start": v(-18.73, -0.7) * mm, "end": v(-18.77, -0.71) * mm});
            skLineSegment(sketch, "E275", {"start": v(-18.77, -0.71) * mm, "end": v(-18.82, -0.71) * mm});
            skLineSegment(sketch, "E276", {"start": v(-18.82, -0.71) * mm, "end": v(-18.86, -0.71) * mm});
            skLineSegment(sketch, "E277", {"start": v(-18.86, -0.71) * mm, "end": v(-18.9, -0.7) * mm});
            skLineSegment(sketch, "E278", {"start": v(-18.9, -0.7) * mm, "end": v(-18.95, -0.7) * mm});
            skLineSegment(sketch, "E279", {"start": v(-18.95, -0.7) * mm, "end": v(-19, -0.7) * mm});
            skLineSegment(sketch, "E280", {"start": v(-19, -0.7) * mm, "end": v(-19.04, -0.69) * mm});
            skLineSegment(sketch, "E281", {"start": v(-19.04, -0.69) * mm, "end": v(-19.09, -0.67) * mm});
            skLineSegment(sketch, "E282", {"start": v(-19.09, -0.67) * mm, "end": v(-19.13, -0.66) * mm});
            skLineSegment(sketch, "E283", {"start": v(-19.13, -0.66) * mm, "end": v(-19.18, -0.65) * mm});
            skLineSegment(sketch, "E284", {"start": v(-19.18, -0.65) * mm, "end": v(-19.23, -0.63) * mm});
            skLineSegment(sketch, "E285", {"start": v(-19.23, -0.63) * mm, "end": v(-19.28, -0.24) * mm});
            skLineSegment(sketch, "E286", {"start": v(-19.28, -0.24) * mm, "end": v(-19.24, -0.21) * mm});
            skLineSegment(sketch, "E287", {"start": v(-19.24, -0.21) * mm, "end": v(-19.2, -0.18) * mm});
            skLineSegment(sketch, "E288", {"start": v(-19.2, -0.18) * mm, "end": v(-19.16, -0.16) * mm});
            skLineSegment(sketch, "E289", {"start": v(-19.16, -0.16) * mm, "end": v(-19.12, -0.13) * mm});
            skLineSegment(sketch, "E290", {"start": v(-19.12, -0.13) * mm, "end": v(-19.08, -0.11) * mm});
            skLineSegment(sketch, "E291", {"start": v(-19.08, -0.11) * mm, "end": v(-19.04, -0.1) * mm});
            skLineSegment(sketch, "E292", {"start": v(-19.04, -0.1) * mm, "end": v(-19, -0.07) * mm});
            skLineSegment(sketch, "E293", {"start": v(-19, -0.07) * mm, "end": v(-18.96, -0.06) * mm});
            skLineSegment(sketch, "E294", {"start": v(-18.96, -0.06) * mm, "end": v(-18.91, -0.04) * mm});
            skLineSegment(sketch, "E295", {"start": v(-18.91, -0.04) * mm, "end": v(-18.87, -0.03) * mm});
            skLineSegment(sketch, "E296", {"start": v(-18.87, -0.03) * mm, "end": v(-18.83, -0.02) * mm});
            skLineSegment(sketch, "E297", {"start": v(-18.83, -0.02) * mm, "end": v(-18.79, -0.02) * mm});
            skLineSegment(sketch, "E298", {"start": v(-18.79, -0.02) * mm, "end": v(-18.77, -0.02) * mm});
            skLineSegment(sketch, "E299", {"start": v(-18.77, -0.02) * mm, "end": v(-18.75, -0.02) * mm});
            skLineSegment(sketch, "E300", {"start": v(-18.75, -0.02) * mm, "end": v(-18.73, 0) * mm});
            skLineSegment(sketch, "E301", {"start": v(-18.73, 0) * mm, "end": v(-18.72, 0) * mm});
            skLineSegment(sketch, "E302", {"start": v(-18.72, 0) * mm, "end": v(-18.7, 0) * mm});
            skLineSegment(sketch, "E303", {"start": v(-18.7, 0) * mm, "end": v(-18.7, 0) * mm});
            skLineSegment(sketch, "E304", {"start": v(-18.7, 0) * mm, "end": v(-18.69, 0.01) * mm});
            skLineSegment(sketch, "E305", {"start": v(-18.69, 0.01) * mm, "end": v(-18.67, 0.02) * mm});
            skLineSegment(sketch, "E306", {"start": v(-18.67, 0.02) * mm, "end": v(-18.66, 0.05) * mm});
            skLineSegment(sketch, "E307", {"start": v(-18.66, 0.05) * mm, "end": v(-18.63, 0.41) * mm});
            skLineSegment(sketch, "E308", {"start": v(-18.63, 0.41) * mm, "end": v(-18.63, 0.44) * mm});
            skLineSegment(sketch, "E309", {"start": v(-18.63, 0.44) * mm, "end": v(-18.64, 0.45) * mm});
            skLineSegment(sketch, "E310", {"start": v(-18.64, 0.45) * mm, "end": v(-18.65, 0.46) * mm});
            skLineSegment(sketch, "E311", {"start": v(-18.65, 0.46) * mm, "end": v(-18.66, 0.47) * mm});
            skLineSegment(sketch, "E312", {"start": v(-18.66, 0.47) * mm, "end": v(-18.67, 0.47) * mm});
            skLineSegment(sketch, "E313", {"start": v(-18.67, 0.47) * mm, "end": v(-18.68, 0.48) * mm});
            skLineSegment(sketch, "E314", {"start": v(-18.68, 0.48) * mm, "end": v(-18.7, 0.5) * mm});
            skLineSegment(sketch, "E315", {"start": v(-18.7, 0.5) * mm, "end": v(-18.72, 0.5) * mm});
            skLineSegment(sketch, "E316", {"start": v(-18.72, 0.5) * mm, "end": v(-18.74, 0.5) * mm});
            skLineSegment(sketch, "E317", {"start": v(-18.74, 0.5) * mm, "end": v(-18.78, 0.52) * mm});
            skLineSegment(sketch, "E318", {"start": v(-18.78, 0.52) * mm, "end": v(-18.82, 0.53) * mm});
            skLineSegment(sketch, "E319", {"start": v(-18.82, 0.53) * mm, "end": v(-18.86, 0.55) * mm});
            skLineSegment(sketch, "E320", {"start": v(-18.86, 0.55) * mm, "end": v(-18.9, 0.57) * mm});
            skLineSegment(sketch, "E321", {"start": v(-18.9, 0.57) * mm, "end": v(-18.93, 0.6) * mm});
            skLineSegment(sketch, "E322", {"start": v(-18.93, 0.6) * mm, "end": v(-18.97, 0.62) * mm});
            skLineSegment(sketch, "E323", {"start": v(-18.97, 0.62) * mm, "end": v(-19, 0.65) * mm});
            skLineSegment(sketch, "E324", {"start": v(-19, 0.65) * mm, "end": v(-19.04, 0.68) * mm});
            skLineSegment(sketch, "E325", {"start": v(-19.04, 0.68) * mm, "end": v(-19.08, 0.71) * mm});
            skLineSegment(sketch, "E326", {"start": v(-19.08, 0.71) * mm, "end": v(-19.11, 0.74) * mm});
            skLineSegment(sketch, "E327", {"start": v(-19.11, 0.74) * mm, "end": v(-19.15, 0.78) * mm});
            skLineSegment(sketch, "E328", {"start": v(-19.15, 0.78) * mm, "end": v(-19.18, 0.82) * mm});
            skLineSegment(sketch, "E329", {"start": v(-19.18, 0.82) * mm, "end": v(-19.05, 1.19) * mm});
            skLineSegment(sketch, "E330", {"start": v(-19.05, 1.19) * mm, "end": v(-19, 1.2) * mm});
            skLineSegment(sketch, "E331", {"start": v(-19, 1.2) * mm, "end": v(-18.95, 1.2) * mm});
            skLineSegment(sketch, "E332", {"start": v(-18.95, 1.2) * mm, "end": v(-18.9, 1.2) * mm});
            skLineSegment(sketch, "E333", {"start": v(-18.9, 1.2) * mm, "end": v(-18.86, 1.2) * mm});
            skLineSegment(sketch, "E334", {"start": v(-18.86, 1.2) * mm, "end": v(-18.81, 1.2) * mm});
            skLineSegment(sketch, "E335", {"start": v(-18.81, 1.2) * mm, "end": v(-18.76, 1.2) * mm});
            skLineSegment(sketch, "E336", {"start": v(-18.76, 1.2) * mm, "end": v(-18.72, 1.2) * mm});
            skLineSegment(sketch, "E337", {"start": v(-18.72, 1.2) * mm, "end": v(-18.68, 1.2) * mm});
            skLineSegment(sketch, "E338", {"start": v(-18.68, 1.2) * mm, "end": v(-18.63, 1.19) * mm});
            skLineSegment(sketch, "E339", {"start": v(-18.63, 1.19) * mm, "end": v(-18.6, 1.18) * mm});
            skLineSegment(sketch, "E340", {"start": v(-18.6, 1.18) * mm, "end": v(-18.55, 1.17) * mm});
            skLineSegment(sketch, "E341", {"start": v(-18.55, 1.17) * mm, "end": v(-18.51, 1.15) * mm});
            skLineSegment(sketch, "E342", {"start": v(-18.51, 1.15) * mm, "end": v(-18.5, 1.14) * mm});
            skLineSegment(sketch, "E343", {"start": v(-18.5, 1.14) * mm, "end": v(-18.47, 1.14) * mm});
            skLineSegment(sketch, "E344", {"start": v(-18.47, 1.14) * mm, "end": v(-18.45, 1.13) * mm});
            skLineSegment(sketch, "E345", {"start": v(-18.45, 1.13) * mm, "end": v(-18.44, 1.13) * mm});
            skLineSegment(sketch, "E346", {"start": v(-18.44, 1.13) * mm, "end": v(-18.43, 1.13) * mm});
            skLineSegment(sketch, "E347", {"start": v(-18.43, 1.13) * mm, "end": v(-18.42, 1.13) * mm});
            skLineSegment(sketch, "E348", {"start": v(-18.42, 1.13) * mm, "end": v(-18.4, 1.13) * mm});
            skLineSegment(sketch, "E349", {"start": v(-18.4, 1.13) * mm, "end": v(-18.39, 1.14) * mm});
            skLineSegment(sketch, "E350", {"start": v(-18.39, 1.14) * mm, "end": v(-18.37, 1.16) * mm});
            skLineSegment(sketch, "E351", {"start": v(-18.37, 1.16) * mm, "end": v(-18.17, 1.46) * mm});
            skLineSegment(sketch, "E352", {"start": v(-18.17, 1.46) * mm, "end": v(-18.16, 1.49) * mm});
            skLineSegment(sketch, "E353", {"start": v(-18.16, 1.49) * mm, "end": v(-18.16, 1.5) * mm});
            skLineSegment(sketch, "E354", {"start": v(-18.16, 1.5) * mm, "end": v(-18.16, 1.51) * mm});
            skLineSegment(sketch, "E355", {"start": v(-18.16, 1.51) * mm, "end": v(-18.17, 1.52) * mm});
            skLineSegment(sketch, "E356", {"start": v(-18.17, 1.52) * mm, "end": v(-18.17, 1.54) * mm});
            skLineSegment(sketch, "E357", {"start": v(-18.17, 1.54) * mm, "end": v(-18.18, 1.54) * mm});
            skLineSegment(sketch, "E358", {"start": v(-18.18, 1.54) * mm, "end": v(-18.2, 1.56) * mm});
            skLineSegment(sketch, "E359", {"start": v(-18.2, 1.56) * mm, "end": v(-18.2, 1.58) * mm});
            skLineSegment(sketch, "E360", {"start": v(-18.2, 1.58) * mm, "end": v(-18.22, 1.6) * mm});
            skLineSegment(sketch, "E361", {"start": v(-18.22, 1.6) * mm, "end": v(-18.25, 1.62) * mm});
            skLineSegment(sketch, "E362", {"start": v(-18.25, 1.62) * mm, "end": v(-18.28, 1.65) * mm});
            skLineSegment(sketch, "E363", {"start": v(-18.28, 1.65) * mm, "end": v(-18.3, 1.69) * mm});
            skLineSegment(sketch, "E364", {"start": v(-18.3, 1.69) * mm, "end": v(-18.33, 1.73) * mm});
            skLineSegment(sketch, "E365", {"start": v(-18.33, 1.73) * mm, "end": v(-18.35, 1.76) * mm});
            skLineSegment(sketch, "E366", {"start": v(-18.35, 1.76) * mm, "end": v(-18.37, 1.8) * mm});
            skLineSegment(sketch, "E367", {"start": v(-18.37, 1.8) * mm, "end": v(-18.4, 1.85) * mm});
            skLineSegment(sketch, "E368", {"start": v(-18.4, 1.85) * mm, "end": v(-18.4, 1.89) * mm});
            skLineSegment(sketch, "E369", {"start": v(-18.4, 1.89) * mm, "end": v(-18.43, 1.93) * mm});
            skLineSegment(sketch, "E370", {"start": v(-18.43, 1.93) * mm, "end": v(-18.44, 1.98) * mm});
            skLineSegment(sketch, "E371", {"start": v(-18.44, 1.98) * mm, "end": v(-18.45, 2.03) * mm});
            skLineSegment(sketch, "E372", {"start": v(-18.45, 2.03) * mm, "end": v(-18.47, 2.07) * mm});
            skLineSegment(sketch, "E373", {"start": v(-18.47, 2.07) * mm, "end": v(-18.18, 2.34) * mm});
            skLineSegment(sketch, "E374", {"start": v(-18.18, 2.34) * mm, "end": v(-18.13, 2.32) * mm});
            skLineSegment(sketch, "E375", {"start": v(-18.13, 2.32) * mm, "end": v(-18.09, 2.3) * mm});
            skLineSegment(sketch, "E376", {"start": v(-18.09, 2.3) * mm, "end": v(-18.04, 2.29) * mm});
            skLineSegment(sketch, "E377", {"start": v(-18.04, 2.29) * mm, "end": v(-18, 2.27) * mm});
            skLineSegment(sketch, "E378", {"start": v(-18, 2.27) * mm, "end": v(-17.96, 2.25) * mm});
            skLineSegment(sketch, "E379", {"start": v(-17.96, 2.25) * mm, "end": v(-17.92, 2.23) * mm});
            skLineSegment(sketch, "E380", {"start": v(-17.92, 2.23) * mm, "end": v(-17.88, 2.2) * mm});
            skLineSegment(sketch, "E381", {"start": v(-17.88, 2.2) * mm, "end": v(-17.84, 2.18) * mm});
            skLineSegment(sketch, "E382", {"start": v(-17.84, 2.18) * mm, "end": v(-17.8, 2.15) * mm});
            skLineSegment(sketch, "E383", {"start": v(-17.8, 2.15) * mm, "end": v(-17.78, 2.12) * mm});
            skLineSegment(sketch, "E384", {"start": v(-17.78, 2.12) * mm, "end": v(-17.75, 2.1) * mm});
            skLineSegment(sketch, "E385", {"start": v(-17.75, 2.1) * mm, "end": v(-17.72, 2.06) * mm});
            skLineSegment(sketch, "E386", {"start": v(-17.72, 2.06) * mm, "end": v(-17.7, 2.04) * mm});
            skLineSegment(sketch, "E387", {"start": v(-17.7, 2.04) * mm, "end": v(-17.7, 2.03) * mm});
            skLineSegment(sketch, "E388", {"start": v(-17.7, 2.03) * mm, "end": v(-17.67, 2.02) * mm});
            skLineSegment(sketch, "E389", {"start": v(-17.67, 2.02) * mm, "end": v(-17.66, 2) * mm});
            skLineSegment(sketch, "E390", {"start": v(-17.66, 2) * mm, "end": v(-17.65, 2) * mm});
            skLineSegment(sketch, "E391", {"start": v(-17.65, 2) * mm, "end": v(-17.64, 2) * mm});
            skLineSegment(sketch, "E392", {"start": v(-17.64, 2) * mm, "end": v(-17.63, 2) * mm});
            skLineSegment(sketch, "E393", {"start": v(-17.63, 2) * mm, "end": v(-17.62, 2) * mm});
            skLineSegment(sketch, "E394", {"start": v(-17.62, 2) * mm, "end": v(-17.59, 2) * mm});
            skLineSegment(sketch, "E395", {"start": v(-17.59, 2) * mm, "end": v(-17.27, 2.17) * mm});
            skLineSegment(sketch, "E396", {"start": v(-17.27, 2.17) * mm, "end": v(-17.25, 2.2) * mm});
            skLineSegment(sketch, "E397", {"start": v(-17.25, 2.2) * mm, "end": v(-17.25, 2.2) * mm});
            skLineSegment(sketch, "E398", {"start": v(-17.25, 2.2) * mm, "end": v(-17.24, 2.22) * mm});
            skLineSegment(sketch, "E399", {"start": v(-17.24, 2.22) * mm, "end": v(-17.24, 2.23) * mm});
            skLineSegment(sketch, "E400", {"start": v(-17.24, 2.23) * mm, "end": v(-17.24, 2.24) * mm});
            skLineSegment(sketch, "E401", {"start": v(-17.24, 2.24) * mm, "end": v(-17.24, 2.25) * mm});
            skLineSegment(sketch, "E402", {"start": v(-17.24, 2.25) * mm, "end": v(-17.25, 2.28) * mm});
            skLineSegment(sketch, "E403", {"start": v(-17.25, 2.28) * mm, "end": v(-17.25, 2.3) * mm});
            skLineSegment(sketch, "E404", {"start": v(-17.25, 2.3) * mm, "end": v(-17.26, 2.32) * mm});
            skLineSegment(sketch, "E405", {"start": v(-17.26, 2.32) * mm, "end": v(-17.27, 2.36) * mm});
            skLineSegment(sketch, "E406", {"start": v(-17.27, 2.36) * mm, "end": v(-17.28, 2.4) * mm});
            skLineSegment(sketch, "E407", {"start": v(-17.28, 2.4) * mm, "end": v(-17.29, 2.44) * mm});
            skLineSegment(sketch, "E408", {"start": v(-17.29, 2.44) * mm, "end": v(-17.3, 2.48) * mm});
            skLineSegment(sketch, "E409", {"start": v(-17.3, 2.48) * mm, "end": v(-17.3, 2.53) * mm});
            skLineSegment(sketch, "E410", {"start": v(-17.3, 2.53) * mm, "end": v(-17.3, 2.57) * mm});
            skLineSegment(sketch, "E411", {"start": v(-17.3, 2.57) * mm, "end": v(-17.29, 2.62) * mm});
            skLineSegment(sketch, "E412", {"start": v(-17.29, 2.62) * mm, "end": v(-17.29, 2.67) * mm});
            skLineSegment(sketch, "E413", {"start": v(-17.29, 2.67) * mm, "end": v(-17.28, 2.71) * mm});
            skLineSegment(sketch, "E414", {"start": v(-17.28, 2.71) * mm, "end": v(-17.27, 2.76) * mm});
            skLineSegment(sketch, "E415", {"start": v(-17.27, 2.76) * mm, "end": v(-17.26, 2.8) * mm});
            skLineSegment(sketch, "E416", {"start": v(-17.26, 2.8) * mm, "end": v(-17.25, 2.86) * mm});
            skLineSegment(sketch, "E417", {"start": v(-17.25, 2.86) * mm, "end": v(-16.87, 2.96) * mm});
            skLineSegment(sketch, "E418", {"start": v(-16.87, 2.96) * mm, "end": v(-16.84, 2.92) * mm});
            skLineSegment(sketch, "E419", {"start": v(-16.84, 2.92) * mm, "end": v(-16.8, 2.89) * mm});
            skLineSegment(sketch, "E420", {"start": v(-16.8, 2.89) * mm, "end": v(-16.78, 2.85) * mm});
            skLineSegment(sketch, "E421", {"start": v(-16.78, 2.85) * mm, "end": v(-16.75, 2.81) * mm});
            skLineSegment(sketch, "E422", {"start": v(-16.75, 2.81) * mm, "end": v(-16.72, 2.77) * mm});
            skLineSegment(sketch, "E423", {"start": v(-16.72, 2.77) * mm, "end": v(-16.7, 2.74) * mm});
            skLineSegment(sketch, "E424", {"start": v(-16.7, 2.74) * mm, "end": v(-16.67, 2.7) * mm});
            skLineSegment(sketch, "E425", {"start": v(-16.67, 2.7) * mm, "end": v(-16.65, 2.66) * mm});
            skLineSegment(sketch, "E426", {"start": v(-16.65, 2.66) * mm, "end": v(-16.63, 2.62) * mm});
            skLineSegment(sketch, "E427", {"start": v(-16.63, 2.62) * mm, "end": v(-16.62, 2.58) * mm});
            skLineSegment(sketch, "E428", {"start": v(-16.62, 2.58) * mm, "end": v(-16.6, 2.54) * mm});
            skLineSegment(sketch, "E429", {"start": v(-16.6, 2.54) * mm, "end": v(-16.6, 2.5) * mm});
            skLineSegment(sketch, "E430", {"start": v(-16.6, 2.5) * mm, "end": v(-16.6, 2.48) * mm});
            skLineSegment(sketch, "E431", {"start": v(-16.6, 2.48) * mm, "end": v(-16.58, 2.46) * mm});
            skLineSegment(sketch, "E432", {"start": v(-16.58, 2.46) * mm, "end": v(-16.58, 2.44) * mm});
            skLineSegment(sketch, "E433", {"start": v(-16.58, 2.44) * mm, "end": v(-16.57, 2.43) * mm});
            skLineSegment(sketch, "E434", {"start": v(-16.57, 2.43) * mm, "end": v(-16.57, 2.42) * mm});
            skLineSegment(sketch, "E435", {"start": v(-16.57, 2.42) * mm, "end": v(-16.56, 2.4) * mm});
            skLineSegment(sketch, "E436", {"start": v(-16.56, 2.4) * mm, "end": v(-16.55, 2.4) * mm});
            skLineSegment(sketch, "E437", {"start": v(-16.55, 2.4) * mm, "end": v(-16.54, 2.39) * mm});
            skLineSegment(sketch, "E438", {"start": v(-16.54, 2.39) * mm, "end": v(-16.5, 2.38) * mm});
            skLineSegment(sketch, "E439", {"start": v(-16.5, 2.38) * mm, "end": v(-16.15, 2.39) * mm});
            skLineSegment(sketch, "E440", {"start": v(-16.15, 2.39) * mm, "end": v(-16.12, 2.4) * mm});
            skLineSegment(sketch, "E441", {"start": v(-16.12, 2.4) * mm, "end": v(-16.1, 2.4) * mm});
            skLineSegment(sketch, "E442", {"start": v(-16.1, 2.4) * mm, "end": v(-16.1, 2.42) * mm});
            skLineSegment(sketch, "E443", {"start": v(-16.1, 2.42) * mm, "end": v(-16.1, 2.43) * mm});
            skLineSegment(sketch, "E444", {"start": v(-16.1, 2.43) * mm, "end": v(-16.09, 2.44) * mm});
            skLineSegment(sketch, "E445", {"start": v(-16.09, 2.44) * mm, "end": v(-16.08, 2.45) * mm});
            skLineSegment(sketch, "E446", {"start": v(-16.08, 2.45) * mm, "end": v(-16.08, 2.47) * mm});
            skLineSegment(sketch, "E447", {"start": v(-16.08, 2.47) * mm, "end": v(-16.07, 2.49) * mm});
            skLineSegment(sketch, "E448", {"start": v(-16.07, 2.49) * mm, "end": v(-16.07, 2.5) * mm});
            skLineSegment(sketch, "E449", {"start": v(-16.07, 2.5) * mm, "end": v(-16.06, 2.55) * mm});
            skLineSegment(sketch, "E450", {"start": v(-16.06, 2.55) * mm, "end": v(-16.05, 2.6) * mm});
            skLineSegment(sketch, "E451", {"start": v(-16.05, 2.6) * mm, "end": v(-16.04, 2.63) * mm});
            skLineSegment(sketch, "E452", {"start": v(-16.04, 2.63) * mm, "end": v(-16.02, 2.67) * mm});
            skLineSegment(sketch, "E453", {"start": v(-16.02, 2.67) * mm, "end": v(-16, 2.71) * mm});
            skLineSegment(sketch, "E454", {"start": v(-16, 2.71) * mm, "end": v(-15.98, 2.75) * mm});
            skLineSegment(sketch, "E455", {"start": v(-15.98, 2.75) * mm, "end": v(-15.96, 2.8) * mm});
            skLineSegment(sketch, "E456", {"start": v(-15.96, 2.8) * mm, "end": v(-15.93, 2.83) * mm});
            skLineSegment(sketch, "E457", {"start": v(-15.93, 2.83) * mm, "end": v(-15.9, 2.87) * mm});
            skLineSegment(sketch, "E458", {"start": v(-15.9, 2.87) * mm, "end": v(-15.87, 2.9) * mm});
            skLineSegment(sketch, "E459", {"start": v(-15.87, 2.9) * mm, "end": v(-15.84, 2.95) * mm});
            skLineSegment(sketch, "E460", {"start": v(-15.84, 2.95) * mm, "end": v(-15.81, 2.99) * mm});
            skLineSegment(sketch, "E461", {"start": v(-15.81, 2.99) * mm, "end": v(-15.43, 2.9) * mm});
            skLineSegment(sketch, "E462", {"start": v(-15.43, 2.9) * mm, "end": v(-15.42, 2.85) * mm});
            skLineSegment(sketch, "E463", {"start": v(-15.42, 2.85) * mm, "end": v(-15.4, 2.8) * mm});
            skLineSegment(sketch, "E464", {"start": v(-15.4, 2.8) * mm, "end": v(-15.4, 2.76) * mm});
            skLineSegment(sketch, "E465", {"start": v(-15.4, 2.76) * mm, "end": v(-15.39, 2.71) * mm});
            skLineSegment(sketch, "E466", {"start": v(-15.39, 2.71) * mm, "end": v(-15.38, 2.67) * mm});
            skLineSegment(sketch, "E467", {"start": v(-15.38, 2.67) * mm, "end": v(-15.38, 2.62) * mm});
            skLineSegment(sketch, "E468", {"start": v(-15.38, 2.62) * mm, "end": v(-15.37, 2.58) * mm});
            skLineSegment(sketch, "E469", {"start": v(-15.37, 2.58) * mm, "end": v(-15.37, 2.53) * mm});
            skLineSegment(sketch, "E470", {"start": v(-15.37, 2.53) * mm, "end": v(-15.37, 2.49) * mm});
            skLineSegment(sketch, "E471", {"start": v(-15.37, 2.49) * mm, "end": v(-15.38, 2.44) * mm});
            skLineSegment(sketch, "E472", {"start": v(-15.38, 2.44) * mm, "end": v(-15.39, 2.4) * mm});
            skLineSegment(sketch, "E473", {"start": v(-15.39, 2.4) * mm, "end": v(-15.4, 2.36) * mm});
            skLineSegment(sketch, "E474", {"start": v(-15.4, 2.36) * mm, "end": v(-15.4, 2.34) * mm});
            skLineSegment(sketch, "E475", {"start": v(-15.4, 2.34) * mm, "end": v(-15.4, 2.32) * mm});
            skLineSegment(sketch, "E476", {"start": v(-15.4, 2.32) * mm, "end": v(-15.4, 2.3) * mm});
            skLineSegment(sketch, "E477", {"start": v(-15.4, 2.3) * mm, "end": v(-15.4, 2.29) * mm});
            skLineSegment(sketch, "E478", {"start": v(-15.4, 2.29) * mm, "end": v(-15.4, 2.28) * mm});
            skLineSegment(sketch, "E479", {"start": v(-15.4, 2.28) * mm, "end": v(-15.4, 2.26) * mm});
            skLineSegment(sketch, "E480", {"start": v(-15.4, 2.26) * mm, "end": v(-15.4, 2.25) * mm});
            skLineSegment(sketch, "E481", {"start": v(-15.4, 2.25) * mm, "end": v(-15.4, 2.24) * mm});
            skLineSegment(sketch, "E482", {"start": v(-15.4, 2.24) * mm, "end": v(-15.38, 2.22) * mm});
            skLineSegment(sketch, "E483", {"start": v(-15.38, 2.22) * mm, "end": v(-15.05, 2.06) * mm});
            skLineSegment(sketch, "E484", {"start": v(-15.05, 2.06) * mm, "end": v(-15.02, 2.05) * mm});
            skLineSegment(sketch, "E485", {"start": v(-15.02, 2.05) * mm, "end": v(-15, 2.06) * mm});
            skLineSegment(sketch, "E486", {"start": v(-15, 2.06) * mm, "end": v(-15, 2.06) * mm});
            skLineSegment(sketch, "E487", {"start": v(-15, 2.06) * mm, "end": v(-14.99, 2.07) * mm});
            skLineSegment(sketch, "E488", {"start": v(-14.99, 2.07) * mm, "end": v(-14.98, 2.07) * mm});
            skLineSegment(sketch, "E489", {"start": v(-14.98, 2.07) * mm, "end": v(-14.97, 2.08) * mm});
            skLineSegment(sketch, "E490", {"start": v(-14.97, 2.08) * mm, "end": v(-14.95, 2.1) * mm});
            skLineSegment(sketch, "E491", {"start": v(-14.95, 2.1) * mm, "end": v(-14.94, 2.11) * mm});
            skLineSegment(sketch, "E492", {"start": v(-14.94, 2.11) * mm, "end": v(-14.92, 2.13) * mm});
            skLineSegment(sketch, "E493", {"start": v(-14.92, 2.13) * mm, "end": v(-14.9, 2.16) * mm});
            skLineSegment(sketch, "E494", {"start": v(-14.9, 2.16) * mm, "end": v(-14.87, 2.2) * mm});
            skLineSegment(sketch, "E495", {"start": v(-14.87, 2.2) * mm, "end": v(-14.84, 2.22) * mm});
            skLineSegment(sketch, "E496", {"start": v(-14.84, 2.22) * mm, "end": v(-14.8, 2.25) * mm});
            skLineSegment(sketch, "E497", {"start": v(-14.8, 2.25) * mm, "end": v(-14.77, 2.28) * mm});
            skLineSegment(sketch, "E498", {"start": v(-14.77, 2.28) * mm, "end": v(-14.73, 2.3) * mm});
            skLineSegment(sketch, "E499", {"start": v(-14.73, 2.3) * mm, "end": v(-14.7, 2.33) * mm});
            skLineSegment(sketch, "E500", {"start": v(-14.7, 2.33) * mm, "end": v(-14.65, 2.35) * mm});
            skLineSegment(sketch, "E501", {"start": v(-14.65, 2.35) * mm, "end": v(-14.61, 2.37) * mm});
            skLineSegment(sketch, "E502", {"start": v(-14.61, 2.37) * mm, "end": v(-14.57, 2.4) * mm});
            skLineSegment(sketch, "E503", {"start": v(-14.57, 2.4) * mm, "end": v(-14.52, 2.41) * mm});
            skLineSegment(sketch, "E504", {"start": v(-14.52, 2.41) * mm, "end": v(-14.48, 2.43) * mm});
            skLineSegment(sketch, "E505", {"start": v(-14.48, 2.43) * mm, "end": v(-14.18, 2.18) * mm});
            skLineSegment(sketch, "E506", {"start": v(-14.18, 2.18) * mm, "end": v(-14.19, 2.13) * mm});
            skLineSegment(sketch, "E507", {"start": v(-14.19, 2.13) * mm, "end": v(-14.2, 2.08) * mm});
            skLineSegment(sketch, "E508", {"start": v(-14.2, 2.08) * mm, "end": v(-14.21, 2.04) * mm});
            skLineSegment(sketch, "E509", {"start": v(-14.21, 2.04) * mm, "end": v(-14.23, 2) * mm});
            skLineSegment(sketch, "E510", {"start": v(-14.23, 2) * mm, "end": v(-14.24, 1.95) * mm});
            skLineSegment(sketch, "E511", {"start": v(-14.24, 1.95) * mm, "end": v(-14.26, 1.9) * mm});
            skLineSegment(sketch, "E512", {"start": v(-14.26, 1.9) * mm, "end": v(-14.28, 1.86) * mm});
            skLineSegment(sketch, "E513", {"start": v(-14.28, 1.86) * mm, "end": v(-14.3, 1.82) * mm});
            skLineSegment(sketch, "E514", {"start": v(-14.3, 1.82) * mm, "end": v(-14.32, 1.79) * mm});
            skLineSegment(sketch, "E515", {"start": v(-14.32, 1.79) * mm, "end": v(-14.35, 1.75) * mm});
            skLineSegment(sketch, "E516", {"start": v(-14.35, 1.75) * mm, "end": v(-14.37, 1.72) * mm});
            skLineSegment(sketch, "E517", {"start": v(-14.37, 1.72) * mm, "end": v(-14.4, 1.69) * mm});
            skLineSegment(sketch, "E518", {"start": v(-14.4, 1.69) * mm, "end": v(-14.41, 1.67) * mm});
            skLineSegment(sketch, "E519", {"start": v(-14.41, 1.67) * mm, "end": v(-14.43, 1.65) * mm});
            skLineSegment(sketch, "E520", {"start": v(-14.43, 1.65) * mm, "end": v(-14.44, 1.64) * mm});
            skLineSegment(sketch, "E521", {"start": v(-14.44, 1.64) * mm, "end": v(-14.44, 1.63) * mm});
            skLineSegment(sketch, "E522", {"start": v(-14.44, 1.63) * mm, "end": v(-14.45, 1.61) * mm});
            skLineSegment(sketch, "E523", {"start": v(-14.45, 1.61) * mm, "end": v(-14.45, 1.6) * mm});
            skLineSegment(sketch, "E524", {"start": v(-14.45, 1.6) * mm, "end": v(-14.46, 1.6) * mm});
            skLineSegment(sketch, "E525", {"start": v(-14.46, 1.6) * mm, "end": v(-14.46, 1.58) * mm});
            skLineSegment(sketch, "E526", {"start": v(-14.46, 1.58) * mm, "end": v(-14.45, 1.55) * mm});
            skLineSegment(sketch, "E527", {"start": v(-14.45, 1.55) * mm, "end": v(-14.23, 1.26) * mm});
            skLineSegment(sketch, "E528", {"start": v(-14.23, 1.26) * mm, "end": v(-14.21, 1.24) * mm});
            skLineSegment(sketch, "E529", {"start": v(-14.21, 1.24) * mm, "end": v(-14.2, 1.23) * mm});
            skLineSegment(sketch, "E530", {"start": v(-14.2, 1.23) * mm, "end": v(-14.18, 1.23) * mm});
            skLineSegment(sketch, "E531", {"start": v(-14.18, 1.23) * mm, "end": v(-14.17, 1.23) * mm});
            skLineSegment(sketch, "E532", {"start": v(-14.17, 1.23) * mm, "end": v(-14.16, 1.24) * mm});
            skLineSegment(sketch, "E533", {"start": v(-14.16, 1.24) * mm, "end": v(-14.15, 1.24) * mm});
            skLineSegment(sketch, "E534", {"start": v(-14.15, 1.24) * mm, "end": v(-14.13, 1.24) * mm});
            skLineSegment(sketch, "E535", {"start": v(-14.13, 1.24) * mm, "end": v(-14.1, 1.25) * mm});
            skLineSegment(sketch, "E536", {"start": v(-14.1, 1.25) * mm, "end": v(-14.09, 1.26) * mm});
            skLineSegment(sketch, "E537", {"start": v(-14.09, 1.26) * mm, "end": v(-14.05, 1.28) * mm});
            skLineSegment(sketch, "E538", {"start": v(-14.05, 1.28) * mm, "end": v(-14.01, 1.3) * mm});
            skLineSegment(sketch, "E539", {"start": v(-14.01, 1.3) * mm, "end": v(-13.97, 1.3) * mm});
            skLineSegment(sketch, "E540", {"start": v(-13.97, 1.3) * mm, "end": v(-13.93, 1.31) * mm});
            skLineSegment(sketch, "E541", {"start": v(-13.93, 1.31) * mm, "end": v(-13.88, 1.32) * mm});
            skLineSegment(sketch, "E542", {"start": v(-13.88, 1.32) * mm, "end": v(-13.84, 1.32) * mm});
            skLineSegment(sketch, "E543", {"start": v(-13.84, 1.32) * mm, "end": v(-13.8, 1.33) * mm});
            skLineSegment(sketch, "E544", {"start": v(-13.8, 1.33) * mm, "end": v(-13.75, 1.33) * mm});
            skLineSegment(sketch, "E545", {"start": v(-13.75, 1.33) * mm, "end": v(-13.7, 1.33) * mm});
            skLineSegment(sketch, "E546", {"start": v(-13.7, 1.33) * mm, "end": v(-13.65, 1.33) * mm});
            skLineSegment(sketch, "E547", {"start": v(-13.65, 1.33) * mm, "end": v(-13.6, 1.32) * mm});
            skLineSegment(sketch, "E548", {"start": v(-13.6, 1.32) * mm, "end": v(-13.55, 1.32) * mm});
            skLineSegment(sketch, "E549", {"start": v(-13.55, 1.32) * mm, "end": v(-13.4, 0.96) * mm});
            skLineSegment(sketch, "E550", {"start": v(-13.4, 0.96) * mm, "end": v(-13.44, 0.92) * mm});
            skLineSegment(sketch, "E551", {"start": v(-13.44, 0.92) * mm, "end": v(-13.47, 0.88) * mm});
            skLineSegment(sketch, "E552", {"start": v(-13.47, 0.88) * mm, "end": v(-13.5, 0.85) * mm});
            skLineSegment(sketch, "E553", {"start": v(-13.5, 0.85) * mm, "end": v(-13.54, 0.81) * mm});
            skLineSegment(sketch, "E554", {"start": v(-13.54, 0.81) * mm, "end": v(-13.57, 0.78) * mm});
            skLineSegment(sketch, "E555", {"start": v(-13.57, 0.78) * mm, "end": v(-13.6, 0.75) * mm});
            skLineSegment(sketch, "E556", {"start": v(-13.6, 0.75) * mm, "end": v(-13.64, 0.72) * mm});
            skLineSegment(sketch, "E557", {"start": v(-13.64, 0.72) * mm, "end": v(-13.68, 0.7) * mm});
            skLineSegment(sketch, "E558", {"start": v(-13.68, 0.7) * mm, "end": v(-13.72, 0.68) * mm});
            skLineSegment(sketch, "E559", {"start": v(-13.72, 0.68) * mm, "end": v(-13.75, 0.65) * mm});
            skLineSegment(sketch, "E560", {"start": v(-13.75, 0.65) * mm, "end": v(-13.8, 0.64) * mm});
            skLineSegment(sketch, "E561", {"start": v(-13.8, 0.64) * mm, "end": v(-13.83, 0.62) * mm});
            skLineSegment(sketch, "E562", {"start": v(-13.83, 0.62) * mm, "end": v(-13.85, 0.62) * mm});
            skLineSegment(sketch, "E563", {"start": v(-13.85, 0.62) * mm, "end": v(-13.87, 0.6) * mm});
            skLineSegment(sketch, "E564", {"start": v(-13.87, 0.6) * mm, "end": v(-13.89, 0.6) * mm});
            skLineSegment(sketch, "E565", {"start": v(-13.89, 0.6) * mm, "end": v(-13.9, 0.6) * mm});
            skLineSegment(sketch, "E566", {"start": v(-13.9, 0.6) * mm, "end": v(-13.9, 0.58) * mm});
            skLineSegment(sketch, "E567", {"start": v(-13.9, 0.58) * mm, "end": v(-13.92, 0.57) * mm});
            skLineSegment(sketch, "E568", {"start": v(-13.92, 0.57) * mm, "end": v(-13.92, 0.57) * mm});
            skLineSegment(sketch, "E569", {"start": v(-13.92, 0.57) * mm, "end": v(-13.93, 0.55) * mm});
            skLineSegment(sketch, "E570", {"start": v(-13.93, 0.55) * mm, "end": v(-13.94, 0.52) * mm});
            skLineSegment(sketch, "E571", {"start": v(-13.94, 0.52) * mm, "end": v(-13.88, 0.17) * mm});
            skLineSegment(sketch, "E572", {"start": v(-17.28, 0) * mm, "end": v(-15.26, 0) * mm});
            skLineSegment(sketch, "E573", {"start": v(-16.27, -1) * mm, "end": v(-16.27, 1) * mm});
            skLineSegment(sketch, "E574", {"start": v(-12.36, -0.04) * mm, "end": v(-12.4, -0.03) * mm});
            skLineSegment(sketch, "E575", {"start": v(-12.4, -0.03) * mm, "end": v(-12.44, -0.01) * mm});
            skLineSegment(sketch, "E576", {"start": v(-12.44, -0.01) * mm, "end": v(-12.52, 0.01) * mm});
            skLineSegment(sketch, "E577", {"start": v(-12.52, 0.01) * mm, "end": v(-12.68, 0.07) * mm});
            skLineSegment(sketch, "E578", {"start": v(-12.68, 0.07) * mm, "end": v(-12.83, 0.13) * mm});
            skLineSegment(sketch, "E579", {"start": v(-12.83, 0.13) * mm, "end": v(-12.99, 0.2) * mm});
            skLineSegment(sketch, "E580", {"start": v(-12.99, 0.2) * mm, "end": v(-12.98, 0.6) * mm});
            skLineSegment(sketch, "E581", {"start": v(-12.98, 0.6) * mm, "end": v(-12.82, 0.67) * mm});
            skLineSegment(sketch, "E582", {"start": v(-12.82, 0.67) * mm, "end": v(-12.66, 0.72) * mm});
            skLineSegment(sketch, "E583", {"start": v(-12.66, 0.72) * mm, "end": v(-12.5, 0.77) * mm});
            skLineSegment(sketch, "E584", {"start": v(-12.5, 0.77) * mm, "end": v(-12.42, 0.79) * mm});
            skLineSegment(sketch, "E585", {"start": v(-12.42, 0.79) * mm, "end": v(-12.38, 0.8) * mm});
            skLineSegment(sketch, "E586", {"start": v(-12.38, 0.8) * mm, "end": v(-12.34, 0.8) * mm});
            skLineSegment(sketch, "E587", {"start": v(-12.34, 0.8) * mm, "end": v(-12.31, 1.24) * mm});
            skLineSegment(sketch, "E588", {"start": v(-12.31, 1.24) * mm, "end": v(-12.35, 1.26) * mm});
            skLineSegment(sketch, "E589", {"start": v(-12.35, 1.26) * mm, "end": v(-12.39, 1.27) * mm});
            skLineSegment(sketch, "E590", {"start": v(-12.39, 1.27) * mm, "end": v(-12.46, 1.3) * mm});
            skLineSegment(sketch, "E591", {"start": v(-12.46, 1.3) * mm, "end": v(-12.62, 1.37) * mm});
            skLineSegment(sketch, "E592", {"start": v(-12.62, 1.37) * mm, "end": v(-12.77, 1.44) * mm});
            skLineSegment(sketch, "E593", {"start": v(-12.77, 1.44) * mm, "end": v(-12.92, 1.52) * mm});
            skLineSegment(sketch, "E594", {"start": v(-12.92, 1.52) * mm, "end": v(-12.87, 1.94) * mm});
            skLineSegment(sketch, "E595", {"start": v(-12.87, 1.94) * mm, "end": v(-12.7, 1.98) * mm});
            skLineSegment(sketch, "E596", {"start": v(-12.7, 1.98) * mm, "end": v(-12.55, 2.02) * mm});
            skLineSegment(sketch, "E597", {"start": v(-12.55, 2.02) * mm, "end": v(-12.38, 2.06) * mm});
            skLineSegment(sketch, "E598", {"start": v(-12.38, 2.06) * mm, "end": v(-12.3, 2.07) * mm});
            skLineSegment(sketch, "E599", {"start": v(-12.3, 2.07) * mm, "end": v(-12.26, 2.08) * mm});
            skLineSegment(sketch, "E600", {"start": v(-12.26, 2.08) * mm, "end": v(-12.22, 2.08) * mm});
            skLineSegment(sketch, "E601", {"start": v(-12.22, 2.08) * mm, "end": v(-12.16, 2.51) * mm});
            skLineSegment(sketch, "E602", {"start": v(-12.16, 2.51) * mm, "end": v(-12.2, 2.53) * mm});
            skLineSegment(sketch, "E603", {"start": v(-12.2, 2.53) * mm, "end": v(-12.23, 2.55) * mm});
            skLineSegment(sketch, "E604", {"start": v(-12.23, 2.55) * mm, "end": v(-12.3, 2.59) * mm});
            skLineSegment(sketch, "E605", {"start": v(-12.3, 2.59) * mm, "end": v(-12.45, 2.67) * mm});
            skLineSegment(sketch, "E606", {"start": v(-12.45, 2.67) * mm, "end": v(-12.6, 2.75) * mm});
            skLineSegment(sketch, "E607", {"start": v(-12.6, 2.75) * mm, "end": v(-12.74, 2.84) * mm});
            skLineSegment(sketch, "E608", {"start": v(-12.74, 2.84) * mm, "end": v(-12.66, 3.25) * mm});
            skLineSegment(sketch, "E609", {"start": v(-12.66, 3.25) * mm, "end": v(-12.5, 3.29) * mm});
            skLineSegment(sketch, "E610", {"start": v(-12.5, 3.29) * mm, "end": v(-12.33, 3.31) * mm});
            skLineSegment(sketch, "E611", {"start": v(-12.33, 3.31) * mm, "end": v(-12.16, 3.33) * mm});
            skLineSegment(sketch, "E612", {"start": v(-12.16, 3.33) * mm, "end": v(-12.08, 3.34) * mm});
            skLineSegment(sketch, "E613", {"start": v(-12.08, 3.34) * mm, "end": v(-12.04, 3.34) * mm});
            skLineSegment(sketch, "E614", {"start": v(-12.04, 3.34) * mm, "end": v(-12, 3.35) * mm});
            skLineSegment(sketch, "E615", {"start": v(-12, 3.35) * mm, "end": v(-11.9, 3.77) * mm});
            skLineSegment(sketch, "E616", {"start": v(-11.9, 3.77) * mm, "end": v(-11.93, 3.8) * mm});
            skLineSegment(sketch, "E617", {"start": v(-11.93, 3.8) * mm, "end": v(-11.97, 3.81) * mm});
            skLineSegment(sketch, "E618", {"start": v(-11.97, 3.81) * mm, "end": v(-12.04, 3.86) * mm});
            skLineSegment(sketch, "E619", {"start": v(-12.04, 3.86) * mm, "end": v(-12.18, 3.95) * mm});
            skLineSegment(sketch, "E620", {"start": v(-12.18, 3.95) * mm, "end": v(-12.31, 4.04) * mm});
            skLineSegment(sketch, "E621", {"start": v(-12.31, 4.04) * mm, "end": v(-12.45, 4.15) * mm});
            skLineSegment(sketch, "E622", {"start": v(-12.45, 4.15) * mm, "end": v(-12.34, 4.55) * mm});
            skLineSegment(sketch, "E623", {"start": v(-12.34, 4.55) * mm, "end": v(-12.17, 4.57) * mm});
            skLineSegment(sketch, "E624", {"start": v(-12.17, 4.57) * mm, "end": v(-12, 4.58) * mm});
            skLineSegment(sketch, "E625", {"start": v(-12, 4.58) * mm, "end": v(-11.83, 4.58) * mm});
            skLineSegment(sketch, "E626", {"start": v(-11.83, 4.58) * mm, "end": v(-11.75, 4.59) * mm});
            skLineSegment(sketch, "E627", {"start": v(-11.75, 4.59) * mm, "end": v(-11.7, 4.59) * mm});
            skLineSegment(sketch, "E628", {"start": v(-11.7, 4.59) * mm, "end": v(-11.67, 4.59) * mm});
            skLineSegment(sketch, "E629", {"start": v(-11.67, 4.59) * mm, "end": v(-11.53, 5) * mm});
            skLineSegment(sketch, "E630", {"start": v(-11.53, 5) * mm, "end": v(-11.57, 5.02) * mm});
            skLineSegment(sketch, "E631", {"start": v(-11.57, 5.02) * mm, "end": v(-11.6, 5.05) * mm});
            skLineSegment(sketch, "E632", {"start": v(-11.6, 5.05) * mm, "end": v(-11.67, 5.1) * mm});
            skLineSegment(sketch, "E633", {"start": v(-11.67, 5.1) * mm, "end": v(-11.8, 5.2) * mm});
            skLineSegment(sketch, "E634", {"start": v(-11.8, 5.2) * mm, "end": v(-11.93, 5.3) * mm});
            skLineSegment(sketch, "E635", {"start": v(-11.93, 5.3) * mm, "end": v(-12.05, 5.42) * mm});
            skLineSegment(sketch, "E636", {"start": v(-12.05, 5.42) * mm, "end": v(-11.9, 5.81) * mm});
            skLineSegment(sketch, "E637", {"start": v(-11.9, 5.81) * mm, "end": v(-11.74, 5.81) * mm});
            skLineSegment(sketch, "E638", {"start": v(-11.74, 5.81) * mm, "end": v(-11.57, 5.81) * mm});
            skLineSegment(sketch, "E639", {"start": v(-11.57, 5.81) * mm, "end": v(-11.4, 5.8) * mm});
            skLineSegment(sketch, "E640", {"start": v(-11.4, 5.8) * mm, "end": v(-11.32, 5.8) * mm});
            skLineSegment(sketch, "E641", {"start": v(-11.32, 5.8) * mm, "end": v(-11.28, 5.8) * mm});
            skLineSegment(sketch, "E642", {"start": v(-11.28, 5.8) * mm, "end": v(-11.24, 5.8) * mm});
            skLineSegment(sketch, "E643", {"start": v(-11.24, 5.8) * mm, "end": v(-11.07, 6.2) * mm});
            skLineSegment(sketch, "E644", {"start": v(-11.07, 6.2) * mm, "end": v(-11.1, 6.22) * mm});
            skLineSegment(sketch, "E645", {"start": v(-11.1, 6.22) * mm, "end": v(-11.13, 6.25) * mm});
            skLineSegment(sketch, "E646", {"start": v(-11.13, 6.25) * mm, "end": v(-11.2, 6.3) * mm});
            skLineSegment(sketch, "E647", {"start": v(-11.2, 6.3) * mm, "end": v(-11.32, 6.42) * mm});
            skLineSegment(sketch, "E648", {"start": v(-11.32, 6.42) * mm, "end": v(-11.44, 6.53) * mm});
            skLineSegment(sketch, "E649", {"start": v(-11.44, 6.53) * mm, "end": v(-11.55, 6.66) * mm});
            skLineSegment(sketch, "E650", {"start": v(-11.55, 6.66) * mm, "end": v(-11.38, 7.03) * mm});
            skLineSegment(sketch, "E651", {"start": v(-11.38, 7.03) * mm, "end": v(-11.2, 7.02) * mm});
            skLineSegment(sketch, "E652", {"start": v(-11.2, 7.02) * mm, "end": v(-11.04, 7) * mm});
            skLineSegment(sketch, "E653", {"start": v(-11.04, 7) * mm, "end": v(-10.87, 6.99) * mm});
            skLineSegment(sketch, "E654", {"start": v(-10.87, 6.99) * mm, "end": v(-10.8, 6.97) * mm});
            skLineSegment(sketch, "E655", {"start": v(-10.8, 6.97) * mm, "end": v(-10.75, 6.97) * mm});
            skLineSegment(sketch, "E656", {"start": v(-10.75, 6.97) * mm, "end": v(-10.71, 6.96) * mm});
            skLineSegment(sketch, "E657", {"start": v(-10.71, 6.96) * mm, "end": v(-10.51, 7.35) * mm});
            skLineSegment(sketch, "E658", {"start": v(-10.51, 7.35) * mm, "end": v(-10.54, 7.38) * mm});
            skLineSegment(sketch, "E659", {"start": v(-10.54, 7.38) * mm, "end": v(-10.57, 7.4) * mm});
            skLineSegment(sketch, "E660", {"start": v(-10.57, 7.4) * mm, "end": v(-10.63, 7.47) * mm});
            skLineSegment(sketch, "E661", {"start": v(-10.63, 7.47) * mm, "end": v(-10.74, 7.59) * mm});
            skLineSegment(sketch, "E662", {"start": v(-10.74, 7.59) * mm, "end": v(-10.85, 7.72) * mm});
            skLineSegment(sketch, "E663", {"start": v(-10.85, 7.72) * mm, "end": v(-10.95, 7.85) * mm});
            skLineSegment(sketch, "E664", {"start": v(-10.95, 7.85) * mm, "end": v(-10.74, 8.21) * mm});
            skLineSegment(sketch, "E665", {"start": v(-10.74, 8.21) * mm, "end": v(-10.58, 8.19) * mm});
            skLineSegment(sketch, "E666", {"start": v(-10.58, 8.19) * mm, "end": v(-10.41, 8.16) * mm});
            skLineSegment(sketch, "E667", {"start": v(-10.41, 8.16) * mm, "end": v(-10.25, 8.12) * mm});
            skLineSegment(sketch, "E668", {"start": v(-10.25, 8.12) * mm, "end": v(-10.17, 8.1) * mm});
            skLineSegment(sketch, "E669", {"start": v(-10.17, 8.1) * mm, "end": v(-10.13, 8.1) * mm});
            skLineSegment(sketch, "E670", {"start": v(-10.13, 8.1) * mm, "end": v(-10.09, 8.08) * mm});
            skLineSegment(sketch, "E671", {"start": v(-10.09, 8.08) * mm, "end": v(-9.86, 8.45) * mm});
            skLineSegment(sketch, "E672", {"start": v(-9.86, 8.45) * mm, "end": v(-9.88, 8.48) * mm});
            skLineSegment(sketch, "E673", {"start": v(-9.88, 8.48) * mm, "end": v(-9.91, 8.51) * mm});
            skLineSegment(sketch, "E674", {"start": v(-9.91, 8.51) * mm, "end": v(-9.96, 8.58) * mm});
            skLineSegment(sketch, "E675", {"start": v(-9.96, 8.58) * mm, "end": v(-10.06, 8.7) * mm});
            skLineSegment(sketch, "E676", {"start": v(-10.06, 8.7) * mm, "end": v(-10.16, 8.84) * mm});
            skLineSegment(sketch, "E677", {"start": v(-10.16, 8.84) * mm, "end": v(-10.26, 8.99) * mm});
            skLineSegment(sketch, "E678", {"start": v(-10.26, 8.99) * mm, "end": v(-10.02, 9.33) * mm});
            skLineSegment(sketch, "E679", {"start": v(-10.02, 9.33) * mm, "end": v(-9.85, 9.3) * mm});
            skLineSegment(sketch, "E680", {"start": v(-9.85, 9.3) * mm, "end": v(-9.7, 9.25) * mm});
            skLineSegment(sketch, "E681", {"start": v(-9.7, 9.25) * mm, "end": v(-9.53, 9.2) * mm});
            skLineSegment(sketch, "E682", {"start": v(-9.53, 9.2) * mm, "end": v(-9.45, 9.17) * mm});
            skLineSegment(sketch, "E683", {"start": v(-9.45, 9.17) * mm, "end": v(-9.42, 9.16) * mm});
            skLineSegment(sketch, "E684", {"start": v(-9.42, 9.16) * mm, "end": v(-9.38, 9.15) * mm});
            skLineSegment(sketch, "E685", {"start": v(-9.38, 9.15) * mm, "end": v(-9.12, 9.5) * mm});
            skLineSegment(sketch, "E686", {"start": v(-9.12, 9.5) * mm, "end": v(-9.14, 9.53) * mm});
            skLineSegment(sketch, "E687", {"start": v(-9.14, 9.53) * mm, "end": v(-9.16, 9.56) * mm});
            skLineSegment(sketch, "E688", {"start": v(-9.16, 9.56) * mm, "end": v(-9.2, 9.63) * mm});
            skLineSegment(sketch, "E689", {"start": v(-9.2, 9.63) * mm, "end": v(-9.3, 9.77) * mm});
            skLineSegment(sketch, "E690", {"start": v(-9.3, 9.77) * mm, "end": v(-9.39, 9.91) * mm});
            skLineSegment(sketch, "E691", {"start": v(-9.39, 9.91) * mm, "end": v(-9.47, 10.06) * mm});
            skLineSegment(sketch, "E692", {"start": v(-9.47, 10.06) * mm, "end": v(-9.2, 10.38) * mm});
            skLineSegment(sketch, "E693", {"start": v(-9.2, 10.38) * mm, "end": v(-9.04, 10.33) * mm});
            skLineSegment(sketch, "E694", {"start": v(-9.04, 10.33) * mm, "end": v(-8.88, 10.28) * mm});
            skLineSegment(sketch, "E695", {"start": v(-8.88, 10.28) * mm, "end": v(-8.73, 10.22) * mm});
            skLineSegment(sketch, "E696", {"start": v(-8.73, 10.22) * mm, "end": v(-8.65, 10.18) * mm});
            skLineSegment(sketch, "E697", {"start": v(-8.65, 10.18) * mm, "end": v(-8.62, 10.17) * mm});
            skLineSegment(sketch, "E698", {"start": v(-8.62, 10.17) * mm, "end": v(-8.58, 10.15) * mm});
            skLineSegment(sketch, "E699", {"start": v(-8.58, 10.15) * mm, "end": v(-8.29, 10.48) * mm});
            skLineSegment(sketch, "E700", {"start": v(-8.29, 10.48) * mm, "end": v(-8.31, 10.51) * mm});
            skLineSegment(sketch, "E701", {"start": v(-8.31, 10.51) * mm, "end": v(-8.33, 10.55) * mm});
            skLineSegment(sketch, "E702", {"start": v(-8.33, 10.55) * mm, "end": v(-8.37, 10.62) * mm});
            skLineSegment(sketch, "E703", {"start": v(-8.37, 10.62) * mm, "end": v(-8.45, 10.76) * mm});
            skLineSegment(sketch, "E704", {"start": v(-8.45, 10.76) * mm, "end": v(-8.52, 10.91) * mm});
            skLineSegment(sketch, "E705", {"start": v(-8.52, 10.91) * mm, "end": v(-8.6, 11.07) * mm});
            skLineSegment(sketch, "E706", {"start": v(-8.6, 11.07) * mm, "end": v(-8.3, 11.37) * mm});
            skLineSegment(sketch, "E707", {"start": v(-8.3, 11.37) * mm, "end": v(-8.15, 11.3) * mm});
            skLineSegment(sketch, "E708", {"start": v(-8.15, 11.3) * mm, "end": v(-8, 11.23) * mm});
            skLineSegment(sketch, "E709", {"start": v(-8, 11.23) * mm, "end": v(-7.85, 11.16) * mm});
            skLineSegment(sketch, "E710", {"start": v(-7.85, 11.16) * mm, "end": v(-7.77, 11.12) * mm});
            skLineSegment(sketch, "E711", {"start": v(-7.77, 11.12) * mm, "end": v(-7.74, 11.1) * mm});
            skLineSegment(sketch, "E712", {"start": v(-7.74, 11.1) * mm, "end": v(-7.7, 11.08) * mm});
            skLineSegment(sketch, "E713", {"start": v(-7.7, 11.08) * mm, "end": v(-7.39, 11.38) * mm});
            skLineSegment(sketch, "E714", {"start": v(-7.39, 11.38) * mm, "end": v(-7.4, 11.42) * mm});
            skLineSegment(sketch, "E715", {"start": v(-7.4, 11.42) * mm, "end": v(-7.42, 11.46) * mm});
            skLineSegment(sketch, "E716", {"start": v(-7.42, 11.46) * mm, "end": v(-7.46, 11.53) * mm});
            skLineSegment(sketch, "E717", {"start": v(-7.46, 11.53) * mm, "end": v(-7.52, 11.69) * mm});
            skLineSegment(sketch, "E718", {"start": v(-7.52, 11.69) * mm, "end": v(-7.58, 11.84) * mm});
            skLineSegment(sketch, "E719", {"start": v(-7.58, 11.84) * mm, "end": v(-7.64, 12) * mm});
            skLineSegment(sketch, "E720", {"start": v(-7.64, 12) * mm, "end": v(-7.33, 12.28) * mm});
            skLineSegment(sketch, "E721", {"start": v(-7.33, 12.28) * mm, "end": v(-7.18, 12.2) * mm});
            skLineSegment(sketch, "E722", {"start": v(-7.18, 12.2) * mm, "end": v(-7.03, 12.12) * mm});
            skLineSegment(sketch, "E723", {"start": v(-7.03, 12.12) * mm, "end": v(-6.89, 12.03) * mm});
            skLineSegment(sketch, "E724", {"start": v(-6.89, 12.03) * mm, "end": v(-6.82, 11.99) * mm});
            skLineSegment(sketch, "E725", {"start": v(-6.82, 11.99) * mm, "end": v(-6.78, 11.96) * mm});
            skLineSegment(sketch, "E726", {"start": v(-6.78, 11.96) * mm, "end": v(-6.75, 11.94) * mm});
            skLineSegment(sketch, "E727", {"start": v(-6.75, 11.94) * mm, "end": v(-6.4, 12.21) * mm});
            skLineSegment(sketch, "E728", {"start": v(-6.4, 12.21) * mm, "end": v(-6.42, 12.25) * mm});
            skLineSegment(sketch, "E729", {"start": v(-6.42, 12.25) * mm, "end": v(-6.44, 12.3) * mm});
            skLineSegment(sketch, "E730", {"start": v(-6.44, 12.3) * mm, "end": v(-6.47, 12.37) * mm});
            skLineSegment(sketch, "E731", {"start": v(-6.47, 12.37) * mm, "end": v(-6.52, 12.53) * mm});
            skLineSegment(sketch, "E732", {"start": v(-6.52, 12.53) * mm, "end": v(-6.57, 12.69) * mm});
            skLineSegment(sketch, "E733", {"start": v(-6.57, 12.69) * mm, "end": v(-6.61, 12.85) * mm});
            skLineSegment(sketch, "E734", {"start": v(-6.61, 12.85) * mm, "end": v(-6.28, 13.1) * mm});
            skLineSegment(sketch, "E735", {"start": v(-6.28, 13.1) * mm, "end": v(-6.13, 13) * mm});
            skLineSegment(sketch, "E736", {"start": v(-6.13, 13) * mm, "end": v(-6, 12.92) * mm});
            skLineSegment(sketch, "E737", {"start": v(-6, 12.92) * mm, "end": v(-5.86, 12.82) * mm});
            skLineSegment(sketch, "E738", {"start": v(-5.86, 12.82) * mm, "end": v(-5.8, 12.77) * mm});
            skLineSegment(sketch, "E739", {"start": v(-5.8, 12.77) * mm, "end": v(-5.76, 12.74) * mm});
            skLineSegment(sketch, "E740", {"start": v(-5.76, 12.74) * mm, "end": v(-5.73, 12.72) * mm});
            skLineSegment(sketch, "E741", {"start": v(-5.73, 12.72) * mm, "end": v(-5.37, 12.96) * mm});
            skLineSegment(sketch, "E742", {"start": v(-5.37, 12.96) * mm, "end": v(-5.38, 13) * mm});
            skLineSegment(sketch, "E743", {"start": v(-5.38, 13) * mm, "end": v(-5.4, 13.04) * mm});
            skLineSegment(sketch, "E744", {"start": v(-5.4, 13.04) * mm, "end": v(-5.41, 13.12) * mm});
            skLineSegment(sketch, "E745", {"start": v(-5.41, 13.12) * mm, "end": v(-5.45, 13.28) * mm});
            skLineSegment(sketch, "E746", {"start": v(-5.45, 13.28) * mm, "end": v(-5.49, 13.45) * mm});
            skLineSegment(sketch, "E747", {"start": v(-5.49, 13.45) * mm, "end": v(-5.52, 13.61) * mm});
            skLineSegment(sketch, "E748", {"start": v(-5.52, 13.61) * mm, "end": v(-5.16, 13.83) * mm});
            skLineSegment(sketch, "E749", {"start": v(-5.16, 13.83) * mm, "end": v(-5.03, 13.73) * mm});
            skLineSegment(sketch, "E750", {"start": v(-5.03, 13.73) * mm, "end": v(-4.9, 13.63) * mm});
            skLineSegment(sketch, "E751", {"start": v(-4.9, 13.63) * mm, "end": v(-4.77, 13.52) * mm});
            skLineSegment(sketch, "E752", {"start": v(-4.77, 13.52) * mm, "end": v(-4.7, 13.46) * mm});
            skLineSegment(sketch, "E753", {"start": v(-4.7, 13.46) * mm, "end": v(-4.68, 13.44) * mm});
            skLineSegment(sketch, "E754", {"start": v(-4.68, 13.44) * mm, "end": v(-4.65, 13.4) * mm});
            skLineSegment(sketch, "E755", {"start": v(-4.65, 13.4) * mm, "end": v(-4.27, 13.62) * mm});
            skLineSegment(sketch, "E756", {"start": v(-4.27, 13.62) * mm, "end": v(-4.28, 13.66) * mm});
            skLineSegment(sketch, "E757", {"start": v(-4.28, 13.66) * mm, "end": v(-4.28, 13.7) * mm});
            skLineSegment(sketch, "E758", {"start": v(-4.28, 13.7) * mm, "end": v(-4.3, 13.78) * mm});
            skLineSegment(sketch, "E759", {"start": v(-4.3, 13.78) * mm, "end": v(-4.33, 13.95) * mm});
            skLineSegment(sketch, "E760", {"start": v(-4.33, 13.95) * mm, "end": v(-4.35, 14.11) * mm});
            skLineSegment(sketch, "E761", {"start": v(-4.35, 14.11) * mm, "end": v(-4.36, 14.28) * mm});
            skLineSegment(sketch, "E762", {"start": v(-4.36, 14.28) * mm, "end": v(-4, 14.47) * mm});
            skLineSegment(sketch, "E763", {"start": v(-4, 14.47) * mm, "end": v(-3.87, 14.36) * mm});
            skLineSegment(sketch, "E764", {"start": v(-3.87, 14.36) * mm, "end": v(-3.74, 14.24) * mm});
            skLineSegment(sketch, "E765", {"start": v(-3.74, 14.24) * mm, "end": v(-3.63, 14.13) * mm});
            skLineSegment(sketch, "E766", {"start": v(-3.63, 14.13) * mm, "end": v(-3.57, 14.07) * mm});
            skLineSegment(sketch, "E767", {"start": v(-3.57, 14.07) * mm, "end": v(-3.54, 14.04) * mm});
            skLineSegment(sketch, "E768", {"start": v(-3.54, 14.04) * mm, "end": v(-3.51, 14) * mm});
            skLineSegment(sketch, "E769", {"start": v(-3.51, 14) * mm, "end": v(-3.12, 14.19) * mm});
            skLineSegment(sketch, "E770", {"start": v(-3.12, 14.19) * mm, "end": v(-3.12, 14.23) * mm});
            skLineSegment(sketch, "E771", {"start": v(-3.12, 14.23) * mm, "end": v(-3.13, 14.27) * mm});
            skLineSegment(sketch, "E772", {"start": v(-3.13, 14.27) * mm, "end": v(-3.14, 14.35) * mm});
            skLineSegment(sketch, "E773", {"start": v(-3.14, 14.35) * mm, "end": v(-3.15, 14.52) * mm});
            skLineSegment(sketch, "E774", {"start": v(-3.15, 14.52) * mm, "end": v(-3.16, 14.68) * mm});
            skLineSegment(sketch, "E775", {"start": v(-3.16, 14.68) * mm, "end": v(-3.16, 14.85) * mm});
            skLineSegment(sketch, "E776", {"start": v(-3.16, 14.85) * mm, "end": v(-2.77, 15.01) * mm});
            skLineSegment(sketch, "E777", {"start": v(-2.77, 15.01) * mm, "end": v(-2.66, 14.89) * mm});
            skLineSegment(sketch, "E778", {"start": v(-2.66, 14.89) * mm, "end": v(-2.54, 14.76) * mm});
            skLineSegment(sketch, "E779", {"start": v(-2.54, 14.76) * mm, "end": v(-2.44, 14.64) * mm});
            skLineSegment(sketch, "E780", {"start": v(-2.44, 14.64) * mm, "end": v(-2.39, 14.57) * mm});
            skLineSegment(sketch, "E781", {"start": v(-2.39, 14.57) * mm, "end": v(-2.36, 14.54) * mm});
            skLineSegment(sketch, "E782", {"start": v(-2.36, 14.54) * mm, "end": v(-2.33, 14.5) * mm});
            skLineSegment(sketch, "E783", {"start": v(-2.33, 14.5) * mm, "end": v(-1.93, 14.66) * mm});
            skLineSegment(sketch, "E784", {"start": v(-1.93, 14.66) * mm, "end": v(-1.93, 14.7) * mm});
            skLineSegment(sketch, "E785", {"start": v(-1.93, 14.7) * mm, "end": v(-1.93, 14.74) * mm});
            skLineSegment(sketch, "E786", {"start": v(-1.93, 14.74) * mm, "end": v(-1.93, 14.82) * mm});
            skLineSegment(sketch, "E787", {"start": v(-1.93, 14.82) * mm, "end": v(-1.93, 14.99) * mm});
            skLineSegment(sketch, "E788", {"start": v(-1.93, 14.99) * mm, "end": v(-1.92, 15.15) * mm});
            skLineSegment(sketch, "E789", {"start": v(-1.92, 15.15) * mm, "end": v(-1.91, 15.32) * mm});
            skLineSegment(sketch, "E790", {"start": v(-1.91, 15.32) * mm, "end": v(-1.51, 15.45) * mm});
            skLineSegment(sketch, "E791", {"start": v(-1.51, 15.45) * mm, "end": v(-1.4, 15.32) * mm});
            skLineSegment(sketch, "E792", {"start": v(-1.4, 15.32) * mm, "end": v(-1.3, 15.18) * mm});
            skLineSegment(sketch, "E793", {"start": v(-1.3, 15.18) * mm, "end": v(-1.2, 15.05) * mm});
            skLineSegment(sketch, "E794", {"start": v(-1.2, 15.05) * mm, "end": v(-1.16, 14.98) * mm});
            skLineSegment(sketch, "E795", {"start": v(-1.16, 14.98) * mm, "end": v(-1.14, 14.95) * mm});
            skLineSegment(sketch, "E796", {"start": v(-1.14, 14.95) * mm, "end": v(-1.12, 14.91) * mm});
            skLineSegment(sketch, "E797", {"start": v(-1.12, 14.91) * mm, "end": v(-0.7, 15.02) * mm});
            skLineSegment(sketch, "E798", {"start": v(-0.7, 15.02) * mm, "end": v(-0.7, 15.07) * mm});
            skLineSegment(sketch, "E799", {"start": v(-0.7, 15.07) * mm, "end": v(-0.7, 15.1) * mm});
            skLineSegment(sketch, "E800", {"start": v(-0.7, 15.1) * mm, "end": v(-0.69, 15.19) * mm});
            skLineSegment(sketch, "E801", {"start": v(-0.69, 15.19) * mm, "end": v(-0.67, 15.35) * mm});
            skLineSegment(sketch, "E802", {"start": v(-0.67, 15.35) * mm, "end": v(-0.65, 15.52) * mm});
            skLineSegment(sketch, "E803", {"start": v(-0.65, 15.52) * mm, "end": v(-0.63, 15.69) * mm});
            skLineSegment(sketch, "E804", {"start": v(-0.63, 15.69) * mm, "end": v(-0.22, 15.78) * mm});
            skLineSegment(sketch, "E805", {"start": v(-0.22, 15.78) * mm, "end": v(-0.13, 15.64) * mm});
            skLineSegment(sketch, "E806", {"start": v(-0.13, 15.64) * mm, "end": v(-0.04, 15.5) * mm});
            skLineSegment(sketch, "E807", {"start": v(-0.04, 15.5) * mm, "end": v(0.05, 15.36) * mm});
            skLineSegment(sketch, "E808", {"start": v(0.05, 15.36) * mm, "end": v(0.09, 15.28) * mm});
            skLineSegment(sketch, "E809", {"start": v(0.09, 15.28) * mm, "end": v(0.1, 15.25) * mm});
            skLineSegment(sketch, "E810", {"start": v(0.1, 15.25) * mm, "end": v(0.13, 15.21) * mm});
            skLineSegment(sketch, "E811", {"start": v(0.13, 15.21) * mm, "end": v(0.56, 15.3) * mm});
            skLineSegment(sketch, "E812", {"start": v(0.56, 15.3) * mm, "end": v(0.56, 15.33) * mm});
            skLineSegment(sketch, "E813", {"start": v(0.56, 15.33) * mm, "end": v(0.57, 15.37) * mm});
            skLineSegment(sketch, "E814", {"start": v(0.57, 15.37) * mm, "end": v(0.58, 15.45) * mm});
            skLineSegment(sketch, "E815", {"start": v(0.58, 15.45) * mm, "end": v(0.6, 15.62) * mm});
            skLineSegment(sketch, "E816", {"start": v(0.6, 15.62) * mm, "end": v(0.64, 15.78) * mm});
            skLineSegment(sketch, "E817", {"start": v(0.64, 15.78) * mm, "end": v(0.68, 15.95) * mm});
            skLineSegment(sketch, "E818", {"start": v(0.68, 15.95) * mm, "end": v(1.1, 16) * mm});
            skLineSegment(sketch, "E819", {"start": v(1.1, 16) * mm, "end": v(1.18, 15.86) * mm});
            skLineSegment(sketch, "E820", {"start": v(1.18, 15.86) * mm, "end": v(1.25, 15.7) * mm});
            skLineSegment(sketch, "E821", {"start": v(1.25, 15.7) * mm, "end": v(1.33, 15.56) * mm});
            skLineSegment(sketch, "E822", {"start": v(1.33, 15.56) * mm, "end": v(1.36, 15.48) * mm});
            skLineSegment(sketch, "E823", {"start": v(1.36, 15.48) * mm, "end": v(1.38, 15.45) * mm});
            skLineSegment(sketch, "E824", {"start": v(1.38, 15.45) * mm, "end": v(1.4, 15.4) * mm});
            skLineSegment(sketch, "E825", {"start": v(1.4, 15.4) * mm, "end": v(1.83, 15.45) * mm});
            skLineSegment(sketch, "E826", {"start": v(1.83, 15.45) * mm, "end": v(1.84, 15.5) * mm});
            skLineSegment(sketch, "E827", {"start": v(1.84, 15.5) * mm, "end": v(1.84, 15.53) * mm});
            skLineSegment(sketch, "E828", {"start": v(1.84, 15.53) * mm, "end": v(1.86, 15.61) * mm});
            skLineSegment(sketch, "E829", {"start": v(1.86, 15.61) * mm, "end": v(1.9, 15.77) * mm});
            skLineSegment(sketch, "E830", {"start": v(1.9, 15.77) * mm, "end": v(1.95, 15.93) * mm});
            skLineSegment(sketch, "E831", {"start": v(1.95, 15.93) * mm, "end": v(2, 16.1) * mm});
            skLineSegment(sketch, "E832", {"start": v(2, 16.1) * mm, "end": v(2.42, 16.12) * mm});
            skLineSegment(sketch, "E833", {"start": v(2.42, 16.12) * mm, "end": v(2.5, 15.97) * mm});
            skLineSegment(sketch, "E834", {"start": v(2.5, 15.97) * mm, "end": v(2.56, 15.81) * mm});
            skLineSegment(sketch, "E835", {"start": v(2.56, 15.81) * mm, "end": v(2.62, 15.66) * mm});
            skLineSegment(sketch, "E836", {"start": v(2.62, 15.66) * mm, "end": v(2.65, 15.58) * mm});
            skLineSegment(sketch, "E837", {"start": v(2.65, 15.58) * mm, "end": v(2.66, 15.54) * mm});
            skLineSegment(sketch, "E838", {"start": v(2.66, 15.54) * mm, "end": v(2.67, 15.5) * mm});
            skLineSegment(sketch, "E839", {"start": v(2.67, 15.5) * mm, "end": v(3.1, 15.5) * mm});
            skLineSegment(sketch, "E840", {"start": v(3.1, 15.5) * mm, "end": v(3.12, 15.55) * mm});
            skLineSegment(sketch, "E841", {"start": v(3.12, 15.55) * mm, "end": v(3.13, 15.59) * mm});
            skLineSegment(sketch, "E842", {"start": v(3.13, 15.59) * mm, "end": v(3.16, 15.67) * mm});
            skLineSegment(sketch, "E843", {"start": v(3.16, 15.67) * mm, "end": v(3.21, 15.82) * mm});
            skLineSegment(sketch, "E844", {"start": v(3.21, 15.82) * mm, "end": v(3.27, 15.98) * mm});
            skLineSegment(sketch, "E845", {"start": v(3.27, 15.98) * mm, "end": v(3.34, 16.14) * mm});
            skLineSegment(sketch, "E846", {"start": v(3.34, 16.14) * mm, "end": v(3.76, 16.12) * mm});
            skLineSegment(sketch, "E847", {"start": v(3.76, 16.12) * mm, "end": v(3.81, 15.97) * mm});
            skLineSegment(sketch, "E848", {"start": v(3.81, 15.97) * mm, "end": v(3.87, 15.8) * mm});
            skLineSegment(sketch, "E849", {"start": v(3.87, 15.8) * mm, "end": v(3.91, 15.65) * mm});
            skLineSegment(sketch, "E850", {"start": v(3.91, 15.65) * mm, "end": v(3.93, 15.57) * mm});
            skLineSegment(sketch, "E851", {"start": v(3.93, 15.57) * mm, "end": v(3.94, 15.53) * mm});
            skLineSegment(sketch, "E852", {"start": v(3.94, 15.53) * mm, "end": v(3.95, 15.49) * mm});
            skLineSegment(sketch, "E853", {"start": v(3.95, 15.49) * mm, "end": v(4.39, 15.46) * mm});
            skLineSegment(sketch, "E854", {"start": v(4.39, 15.46) * mm, "end": v(4.4, 15.5) * mm});
            skLineSegment(sketch, "E855", {"start": v(4.4, 15.5) * mm, "end": v(4.42, 15.54) * mm});
            skLineSegment(sketch, "E856", {"start": v(4.42, 15.54) * mm, "end": v(4.45, 15.61) * mm});
            skLineSegment(sketch, "E857", {"start": v(4.45, 15.61) * mm, "end": v(4.52, 15.76) * mm});
            skLineSegment(sketch, "E858", {"start": v(4.52, 15.76) * mm, "end": v(4.6, 15.91) * mm});
            skLineSegment(sketch, "E859", {"start": v(4.6, 15.91) * mm, "end": v(4.67, 16.06) * mm});
            skLineSegment(sketch, "E860", {"start": v(4.67, 16.06) * mm, "end": v(5.09, 16.02) * mm});
            skLineSegment(sketch, "E861", {"start": v(5.09, 16.02) * mm, "end": v(5.13, 15.86) * mm});
            skLineSegment(sketch, "E862", {"start": v(5.13, 15.86) * mm, "end": v(5.17, 15.7) * mm});
            skLineSegment(sketch, "E863", {"start": v(5.17, 15.7) * mm, "end": v(5.2, 15.53) * mm});
            skLineSegment(sketch, "E864", {"start": v(5.2, 15.53) * mm, "end": v(5.22, 15.45) * mm});
            skLineSegment(sketch, "E865", {"start": v(5.22, 15.45) * mm, "end": v(5.22, 15.4) * mm});
            skLineSegment(sketch, "E866", {"start": v(5.22, 15.4) * mm, "end": v(5.23, 15.37) * mm});
            skLineSegment(sketch, "E867", {"start": v(5.23, 15.37) * mm, "end": v(5.66, 15.3) * mm});
            skLineSegment(sketch, "E868", {"start": v(5.66, 15.3) * mm, "end": v(5.68, 15.34) * mm});
            skLineSegment(sketch, "E869", {"start": v(5.68, 15.34) * mm, "end": v(5.7, 15.38) * mm});
            skLineSegment(sketch, "E870", {"start": v(5.7, 15.38) * mm, "end": v(5.74, 15.45) * mm});
            skLineSegment(sketch, "E871", {"start": v(5.74, 15.45) * mm, "end": v(5.82, 15.6) * mm});
            skLineSegment(sketch, "E872", {"start": v(5.82, 15.6) * mm, "end": v(5.9, 15.74) * mm});
            skLineSegment(sketch, "E873", {"start": v(5.9, 15.74) * mm, "end": v(6, 15.88) * mm});
            skLineSegment(sketch, "E874", {"start": v(6, 15.88) * mm, "end": v(6.4, 15.8) * mm});
            skLineSegment(sketch, "E875", {"start": v(6.4, 15.8) * mm, "end": v(6.43, 15.64) * mm});
            skLineSegment(sketch, "E876", {"start": v(6.43, 15.64) * mm, "end": v(6.46, 15.47) * mm});
            skLineSegment(sketch, "E877", {"start": v(6.46, 15.47) * mm, "end": v(6.48, 15.3) * mm});
            skLineSegment(sketch, "E878", {"start": v(6.48, 15.3) * mm, "end": v(6.49, 15.23) * mm});
            skLineSegment(sketch, "E879", {"start": v(6.49, 15.23) * mm, "end": v(6.49, 15.18) * mm});
            skLineSegment(sketch, "E880", {"start": v(6.49, 15.18) * mm, "end": v(6.5, 15.14) * mm});
            skLineSegment(sketch, "E881", {"start": v(6.5, 15.14) * mm, "end": v(6.92, 15.04) * mm});
            skLineSegment(sketch, "E882", {"start": v(6.92, 15.04) * mm, "end": v(6.94, 15.08) * mm});
            skLineSegment(sketch, "E883", {"start": v(6.94, 15.08) * mm, "end": v(6.96, 15.11) * mm});
            skLineSegment(sketch, "E884", {"start": v(6.96, 15.11) * mm, "end": v(7, 15.18) * mm});
            skLineSegment(sketch, "E885", {"start": v(7, 15.18) * mm, "end": v(7.1, 15.32) * mm});
            skLineSegment(sketch, "E886", {"start": v(7.1, 15.32) * mm, "end": v(7.2, 15.46) * mm});
            skLineSegment(sketch, "E887", {"start": v(7.2, 15.46) * mm, "end": v(7.3, 15.6) * mm});
            skLineSegment(sketch, "E888", {"start": v(7.3, 15.6) * mm, "end": v(7.7, 15.48) * mm});
            skLineSegment(sketch, "E889", {"start": v(7.7, 15.48) * mm, "end": v(7.71, 15.31) * mm});
            skLineSegment(sketch, "E890", {"start": v(7.71, 15.31) * mm, "end": v(7.72, 15.15) * mm});
            skLineSegment(sketch, "E891", {"start": v(7.72, 15.15) * mm, "end": v(7.73, 14.98) * mm});
            skLineSegment(sketch, "E892", {"start": v(7.73, 14.98) * mm, "end": v(7.73, 14.9) * mm});
            skLineSegment(sketch, "E893", {"start": v(7.73, 14.9) * mm, "end": v(7.73, 14.86) * mm});
            skLineSegment(sketch, "E894", {"start": v(7.73, 14.86) * mm, "end": v(7.73, 14.82) * mm});
            skLineSegment(sketch, "E895", {"start": v(7.73, 14.82) * mm, "end": v(8.15, 14.68) * mm});
            skLineSegment(sketch, "E896", {"start": v(8.15, 14.68) * mm, "end": v(8.17, 14.71) * mm});
            skLineSegment(sketch, "E897", {"start": v(8.17, 14.71) * mm, "end": v(8.2, 14.75) * mm});
            skLineSegment(sketch, "E898", {"start": v(8.2, 14.75) * mm, "end": v(8.24, 14.81) * mm});
            skLineSegment(sketch, "E899", {"start": v(8.24, 14.81) * mm, "end": v(8.35, 14.94) * mm});
            skLineSegment(sketch, "E900", {"start": v(8.35, 14.94) * mm, "end": v(8.45, 15.07) * mm});
            skLineSegment(sketch, "E901", {"start": v(8.45, 15.07) * mm, "end": v(8.57, 15.2) * mm});
            skLineSegment(sketch, "E902", {"start": v(8.57, 15.2) * mm, "end": v(8.96, 15.05) * mm});
            skLineSegment(sketch, "E903", {"start": v(8.96, 15.05) * mm, "end": v(8.96, 14.88) * mm});
            skLineSegment(sketch, "E904", {"start": v(8.96, 14.88) * mm, "end": v(8.96, 14.72) * mm});
            skLineSegment(sketch, "E905", {"start": v(8.96, 14.72) * mm, "end": v(8.95, 14.55) * mm});
            skLineSegment(sketch, "E906", {"start": v(8.95, 14.55) * mm, "end": v(8.95, 14.47) * mm});
            skLineSegment(sketch, "E907", {"start": v(8.95, 14.47) * mm, "end": v(8.94, 14.43) * mm});
            skLineSegment(sketch, "E908", {"start": v(8.94, 14.43) * mm, "end": v(8.94, 14.39) * mm});
            skLineSegment(sketch, "E909", {"start": v(8.94, 14.39) * mm, "end": v(9.34, 14.22) * mm});
            skLineSegment(sketch, "E910", {"start": v(9.34, 14.22) * mm, "end": v(9.37, 14.25) * mm});
            skLineSegment(sketch, "E911", {"start": v(9.37, 14.25) * mm, "end": v(9.4, 14.28) * mm});
            skLineSegment(sketch, "E912", {"start": v(9.4, 14.28) * mm, "end": v(9.45, 14.34) * mm});
            skLineSegment(sketch, "E913", {"start": v(9.45, 14.34) * mm, "end": v(9.56, 14.46) * mm});
            skLineSegment(sketch, "E914", {"start": v(9.56, 14.46) * mm, "end": v(9.68, 14.58) * mm});
            skLineSegment(sketch, "E915", {"start": v(9.68, 14.58) * mm, "end": v(9.8, 14.7) * mm});
            skLineSegment(sketch, "E916", {"start": v(9.8, 14.7) * mm, "end": v(10.18, 14.52) * mm});
            skLineSegment(sketch, "E917", {"start": v(10.18, 14.52) * mm, "end": v(10.17, 14.35) * mm});
            skLineSegment(sketch, "E918", {"start": v(10.17, 14.35) * mm, "end": v(10.15, 14.19) * mm});
            skLineSegment(sketch, "E919", {"start": v(10.15, 14.19) * mm, "end": v(10.13, 14.02) * mm});
            skLineSegment(sketch, "E920", {"start": v(10.13, 14.02) * mm, "end": v(10.12, 13.94) * mm});
            skLineSegment(sketch, "E921", {"start": v(10.12, 13.94) * mm, "end": v(10.11, 13.9) * mm});
            skLineSegment(sketch, "E922", {"start": v(10.11, 13.9) * mm, "end": v(10.1, 13.86) * mm});
            skLineSegment(sketch, "E923", {"start": v(10.1, 13.86) * mm, "end": v(10.5, 13.66) * mm});
            skLineSegment(sketch, "E924", {"start": v(10.5, 13.66) * mm, "end": v(10.52, 13.69) * mm});
            skLineSegment(sketch, "E925", {"start": v(10.52, 13.69) * mm, "end": v(10.55, 13.72) * mm});
            skLineSegment(sketch, "E926", {"start": v(10.55, 13.72) * mm, "end": v(10.61, 13.77) * mm});
            skLineSegment(sketch, "E927", {"start": v(10.61, 13.77) * mm, "end": v(10.73, 13.88) * mm});
            skLineSegment(sketch, "E928", {"start": v(10.73, 13.88) * mm, "end": v(10.86, 14) * mm});
            skLineSegment(sketch, "E929", {"start": v(10.86, 14) * mm, "end": v(11, 14.1) * mm});
            skLineSegment(sketch, "E930", {"start": v(11, 14.1) * mm, "end": v(11.36, 13.9) * mm});
            skLineSegment(sketch, "E931", {"start": v(11.36, 13.9) * mm, "end": v(11.33, 13.72) * mm});
            skLineSegment(sketch, "E932", {"start": v(11.33, 13.72) * mm, "end": v(11.3, 13.56) * mm});
            skLineSegment(sketch, "E933", {"start": v(11.3, 13.56) * mm, "end": v(11.27, 13.4) * mm});
            skLineSegment(sketch, "E934", {"start": v(11.27, 13.4) * mm, "end": v(11.25, 13.32) * mm});
            skLineSegment(sketch, "E935", {"start": v(11.25, 13.32) * mm, "end": v(11.24, 13.28) * mm});
            skLineSegment(sketch, "E936", {"start": v(11.24, 13.28) * mm, "end": v(11.23, 13.24) * mm});
            skLineSegment(sketch, "E937", {"start": v(11.23, 13.24) * mm, "end": v(11.6, 13) * mm});
            skLineSegment(sketch, "E938", {"start": v(11.6, 13) * mm, "end": v(11.63, 13.03) * mm});
            skLineSegment(sketch, "E939", {"start": v(11.63, 13.03) * mm, "end": v(11.66, 13.06) * mm});
            skLineSegment(sketch, "E940", {"start": v(11.66, 13.06) * mm, "end": v(11.72, 13.1) * mm});
            skLineSegment(sketch, "E941", {"start": v(11.72, 13.1) * mm, "end": v(11.86, 13.21) * mm});
            skLineSegment(sketch, "E942", {"start": v(11.86, 13.21) * mm, "end": v(12, 13.3) * mm});
            skLineSegment(sketch, "E943", {"start": v(12, 13.3) * mm, "end": v(12.13, 13.4) * mm});
            skLineSegment(sketch, "E944", {"start": v(12.13, 13.4) * mm, "end": v(12.48, 13.17) * mm});
            skLineSegment(sketch, "E945", {"start": v(12.48, 13.17) * mm, "end": v(12.44, 13) * mm});
            skLineSegment(sketch, "E946", {"start": v(12.44, 13) * mm, "end": v(12.4, 12.84) * mm});
            skLineSegment(sketch, "E947", {"start": v(12.4, 12.84) * mm, "end": v(12.35, 12.68) * mm});
            skLineSegment(sketch, "E948", {"start": v(12.35, 12.68) * mm, "end": v(12.32, 12.6) * mm});
            skLineSegment(sketch, "E949", {"start": v(12.32, 12.6) * mm, "end": v(12.3, 12.56) * mm});
            skLineSegment(sketch, "E950", {"start": v(12.3, 12.56) * mm, "end": v(12.3, 12.52) * mm});
            skLineSegment(sketch, "E951", {"start": v(12.3, 12.52) * mm, "end": v(12.64, 12.26) * mm});
            skLineSegment(sketch, "E952", {"start": v(12.64, 12.26) * mm, "end": v(12.68, 12.29) * mm});
            skLineSegment(sketch, "E953", {"start": v(12.68, 12.29) * mm, "end": v(12.7, 12.3) * mm});
            skLineSegment(sketch, "E954", {"start": v(12.7, 12.3) * mm, "end": v(12.78, 12.36) * mm});
            skLineSegment(sketch, "E955", {"start": v(12.78, 12.36) * mm, "end": v(12.92, 12.45) * mm});
            skLineSegment(sketch, "E956", {"start": v(12.92, 12.45) * mm, "end": v(13.06, 12.53) * mm});
            skLineSegment(sketch, "E957", {"start": v(13.06, 12.53) * mm, "end": v(13.2, 12.62) * mm});
            skLineSegment(sketch, "E958", {"start": v(13.2, 12.62) * mm, "end": v(13.53, 12.35) * mm});
            skLineSegment(sketch, "E959", {"start": v(13.53, 12.35) * mm, "end": v(13.48, 12.19) * mm});
            skLineSegment(sketch, "E960", {"start": v(13.48, 12.19) * mm, "end": v(13.42, 12.03) * mm});
            skLineSegment(sketch, "E961", {"start": v(13.42, 12.03) * mm, "end": v(13.36, 11.88) * mm});
            skLineSegment(sketch, "E962", {"start": v(13.36, 11.88) * mm, "end": v(13.33, 11.8) * mm});
            skLineSegment(sketch, "E963", {"start": v(13.33, 11.8) * mm, "end": v(13.31, 11.76) * mm});
            skLineSegment(sketch, "E964", {"start": v(13.31, 11.76) * mm, "end": v(13.3, 11.73) * mm});
            skLineSegment(sketch, "E965", {"start": v(13.3, 11.73) * mm, "end": v(13.62, 11.44) * mm});
            skLineSegment(sketch, "E966", {"start": v(13.62, 11.44) * mm, "end": v(13.66, 11.46) * mm});
            skLineSegment(sketch, "E967", {"start": v(13.66, 11.46) * mm, "end": v(13.7, 11.48) * mm});
            skLineSegment(sketch, "E968", {"start": v(13.7, 11.48) * mm, "end": v(13.76, 11.52) * mm});
            skLineSegment(sketch, "E969", {"start": v(13.76, 11.52) * mm, "end": v(13.91, 11.6) * mm});
            skLineSegment(sketch, "E970", {"start": v(13.91, 11.6) * mm, "end": v(14.06, 11.67) * mm});
            skLineSegment(sketch, "E971", {"start": v(14.06, 11.67) * mm, "end": v(14.22, 11.74) * mm});
            skLineSegment(sketch, "E972", {"start": v(14.22, 11.74) * mm, "end": v(14.52, 11.45) * mm});
            skLineSegment(sketch, "E973", {"start": v(14.52, 11.45) * mm, "end": v(14.45, 11.3) * mm});
            skLineSegment(sketch, "E974", {"start": v(14.45, 11.3) * mm, "end": v(14.38, 11.14) * mm});
            skLineSegment(sketch, "E975", {"start": v(14.38, 11.14) * mm, "end": v(14.3, 11) * mm});
            skLineSegment(sketch, "E976", {"start": v(14.3, 11) * mm, "end": v(14.27, 10.92) * mm});
            skLineSegment(sketch, "E977", {"start": v(14.27, 10.92) * mm, "end": v(14.25, 10.88) * mm});
            skLineSegment(sketch, "E978", {"start": v(14.25, 10.88) * mm, "end": v(14.23, 10.85) * mm});
            skLineSegment(sketch, "E979", {"start": v(14.23, 10.85) * mm, "end": v(14.53, 10.53) * mm});
            skLineSegment(sketch, "E980", {"start": v(14.53, 10.53) * mm, "end": v(14.57, 10.55) * mm});
            skLineSegment(sketch, "E981", {"start": v(14.57, 10.55) * mm, "end": v(14.6, 10.57) * mm});
            skLineSegment(sketch, "E982", {"start": v(14.6, 10.57) * mm, "end": v(14.68, 10.6) * mm});
            skLineSegment(sketch, "E983", {"start": v(14.68, 10.6) * mm, "end": v(14.83, 10.67) * mm});
            skLineSegment(sketch, "E984", {"start": v(14.83, 10.67) * mm, "end": v(14.99, 10.73) * mm});
            skLineSegment(sketch, "E985", {"start": v(14.99, 10.73) * mm, "end": v(15.15, 10.79) * mm});
            skLineSegment(sketch, "E986", {"start": v(15.15, 10.79) * mm, "end": v(15.42, 10.47) * mm});
            skLineSegment(sketch, "E987", {"start": v(15.42, 10.47) * mm, "end": v(15.34, 10.32) * mm});
            skLineSegment(sketch, "E988", {"start": v(15.34, 10.32) * mm, "end": v(15.26, 10.18) * mm});
            skLineSegment(sketch, "E989", {"start": v(15.26, 10.18) * mm, "end": v(15.18, 10.03) * mm});
            skLineSegment(sketch, "E990", {"start": v(15.18, 10.03) * mm, "end": v(15.13, 9.96) * mm});
            skLineSegment(sketch, "E991", {"start": v(15.13, 9.96) * mm, "end": v(15.11, 9.93) * mm});
            skLineSegment(sketch, "E992", {"start": v(15.11, 9.93) * mm, "end": v(15.09, 9.9) * mm});
            skLineSegment(sketch, "E993", {"start": v(15.09, 9.9) * mm, "end": v(15.36, 9.56) * mm});
            skLineSegment(sketch, "E994", {"start": v(15.36, 9.56) * mm, "end": v(15.4, 9.57) * mm});
            skLineSegment(sketch, "E995", {"start": v(15.4, 9.57) * mm, "end": v(15.44, 9.59) * mm});
            skLineSegment(sketch, "E996", {"start": v(15.44, 9.59) * mm, "end": v(15.52, 9.61) * mm});
            skLineSegment(sketch, "E997", {"start": v(15.52, 9.61) * mm, "end": v(15.67, 9.67) * mm});
            skLineSegment(sketch, "E998", {"start": v(15.67, 9.67) * mm, "end": v(15.83, 9.72) * mm});
            skLineSegment(sketch, "E999", {"start": v(15.83, 9.72) * mm, "end": v(16, 9.76) * mm});
            skLineSegment(sketch, "E1000", {"start": v(16, 9.76) * mm, "end": v(16.25, 9.42) * mm});
            skLineSegment(sketch, "E1001", {"start": v(16.25, 9.42) * mm, "end": v(16.16, 9.28) * mm});
            skLineSegment(sketch, "E1002", {"start": v(16.16, 9.28) * mm, "end": v(16.06, 9.14) * mm});
            skLineSegment(sketch, "E1003", {"start": v(16.06, 9.14) * mm, "end": v(15.97, 9) * mm});
            skLineSegment(sketch, "E1004", {"start": v(15.97, 9) * mm, "end": v(15.92, 8.94) * mm});
            skLineSegment(sketch, "E1005", {"start": v(15.92, 8.94) * mm, "end": v(15.9, 8.9) * mm});
            skLineSegment(sketch, "E1006", {"start": v(15.9, 8.9) * mm, "end": v(15.86, 8.88) * mm});
            skLineSegment(sketch, "E1007", {"start": v(15.86, 8.88) * mm, "end": v(16.1, 8.51) * mm});
            skLineSegment(sketch, "E1008", {"start": v(16.1, 8.51) * mm, "end": v(16.15, 8.53) * mm});
            skLineSegment(sketch, "E1009", {"start": v(16.15, 8.53) * mm, "end": v(16.19, 8.54) * mm});
            skLineSegment(sketch, "E1010", {"start": v(16.19, 8.54) * mm, "end": v(16.27, 8.56) * mm});
            skLineSegment(sketch, "E1011", {"start": v(16.27, 8.56) * mm, "end": v(16.43, 8.6) * mm});
            skLineSegment(sketch, "E1012", {"start": v(16.43, 8.6) * mm, "end": v(16.6, 8.63) * mm});
            skLineSegment(sketch, "E1013", {"start": v(16.6, 8.63) * mm, "end": v(16.76, 8.66) * mm});
            skLineSegment(sketch, "E1014", {"start": v(16.76, 8.66) * mm, "end": v(16.98, 8.3) * mm});
            skLineSegment(sketch, "E1015", {"start": v(16.98, 8.3) * mm, "end": v(16.88, 8.17) * mm});
            skLineSegment(sketch, "E1016", {"start": v(16.88, 8.17) * mm, "end": v(16.77, 8.04) * mm});
            skLineSegment(sketch, "E1017", {"start": v(16.77, 8.04) * mm, "end": v(16.67, 7.92) * mm});
            skLineSegment(sketch, "E1018", {"start": v(16.67, 7.92) * mm, "end": v(16.61, 7.85) * mm});
            skLineSegment(sketch, "E1019", {"start": v(16.61, 7.85) * mm, "end": v(16.58, 7.82) * mm});
            skLineSegment(sketch, "E1020", {"start": v(16.58, 7.82) * mm, "end": v(16.55, 7.8) * mm});
            skLineSegment(sketch, "E1021", {"start": v(16.55, 7.8) * mm, "end": v(16.77, 7.42) * mm});
            skLineSegment(sketch, "E1022", {"start": v(16.77, 7.42) * mm, "end": v(16.8, 7.42) * mm});
            skLineSegment(sketch, "E1023", {"start": v(16.8, 7.42) * mm, "end": v(16.85, 7.43) * mm});
            skLineSegment(sketch, "E1024", {"start": v(16.85, 7.43) * mm, "end": v(16.93, 7.45) * mm});
            skLineSegment(sketch, "E1025", {"start": v(16.93, 7.45) * mm, "end": v(17.1, 7.47) * mm});
            skLineSegment(sketch, "E1026", {"start": v(17.1, 7.47) * mm, "end": v(17.26, 7.5) * mm});
            skLineSegment(sketch, "E1027", {"start": v(17.26, 7.5) * mm, "end": v(17.43, 7.51) * mm});
            skLineSegment(sketch, "E1028", {"start": v(17.43, 7.51) * mm, "end": v(17.62, 7.14) * mm});
            skLineSegment(sketch, "E1029", {"start": v(17.62, 7.14) * mm, "end": v(17.5, 7.01) * mm});
            skLineSegment(sketch, "E1030", {"start": v(17.5, 7.01) * mm, "end": v(17.4, 6.9) * mm});
            skLineSegment(sketch, "E1031", {"start": v(17.4, 6.9) * mm, "end": v(17.27, 6.77) * mm});
            skLineSegment(sketch, "E1032", {"start": v(17.27, 6.77) * mm, "end": v(17.21, 6.72) * mm});
            skLineSegment(sketch, "E1033", {"start": v(17.21, 6.72) * mm, "end": v(17.18, 6.69) * mm});
            skLineSegment(sketch, "E1034", {"start": v(17.18, 6.69) * mm, "end": v(17.15, 6.66) * mm});
            skLineSegment(sketch, "E1035", {"start": v(17.15, 6.66) * mm, "end": v(17.33, 6.27) * mm});
            skLineSegment(sketch, "E1036", {"start": v(17.33, 6.27) * mm, "end": v(17.37, 6.27) * mm});
            skLineSegment(sketch, "E1037", {"start": v(17.37, 6.27) * mm, "end": v(17.42, 6.27) * mm});
            skLineSegment(sketch, "E1038", {"start": v(17.42, 6.27) * mm, "end": v(17.5, 6.28) * mm});
            skLineSegment(sketch, "E1039", {"start": v(17.5, 6.28) * mm, "end": v(17.66, 6.3) * mm});
            skLineSegment(sketch, "E1040", {"start": v(17.66, 6.3) * mm, "end": v(17.83, 6.3) * mm});
            skLineSegment(sketch, "E1041", {"start": v(17.83, 6.3) * mm, "end": v(18, 6.3) * mm});
            skLineSegment(sketch, "E1042", {"start": v(18, 6.3) * mm, "end": v(18.16, 5.92) * mm});
            skLineSegment(sketch, "E1043", {"start": v(18.16, 5.92) * mm, "end": v(18.04, 5.8) * mm});
            skLineSegment(sketch, "E1044", {"start": v(18.04, 5.8) * mm, "end": v(17.91, 5.7) * mm});
            skLineSegment(sketch, "E1045", {"start": v(17.91, 5.7) * mm, "end": v(17.78, 5.58) * mm});
            skLineSegment(sketch, "E1046", {"start": v(17.78, 5.58) * mm, "end": v(17.72, 5.53) * mm});
            skLineSegment(sketch, "E1047", {"start": v(17.72, 5.53) * mm, "end": v(17.69, 5.5) * mm});
            skLineSegment(sketch, "E1048", {"start": v(17.69, 5.5) * mm, "end": v(17.65, 5.48) * mm});
            skLineSegment(sketch, "E1049", {"start": v(17.65, 5.48) * mm, "end": v(17.8, 5.07) * mm});
            skLineSegment(sketch, "E1050", {"start": v(17.8, 5.07) * mm, "end": v(17.84, 5.07) * mm});
            skLineSegment(sketch, "E1051", {"start": v(17.84, 5.07) * mm, "end": v(17.88, 5.08) * mm});
            skLineSegment(sketch, "E1052", {"start": v(17.88, 5.08) * mm, "end": v(17.97, 5.08) * mm});
            skLineSegment(sketch, "E1053", {"start": v(17.97, 5.08) * mm, "end": v(18.13, 5.08) * mm});
            skLineSegment(sketch, "E1054", {"start": v(18.13, 5.08) * mm, "end": v(18.3, 5.07) * mm});
            skLineSegment(sketch, "E1055", {"start": v(18.3, 5.07) * mm, "end": v(18.47, 5.06) * mm});
            skLineSegment(sketch, "E1056", {"start": v(18.47, 5.06) * mm, "end": v(18.6, 4.66) * mm});
            skLineSegment(sketch, "E1057", {"start": v(18.6, 4.66) * mm, "end": v(18.46, 4.55) * mm});
            skLineSegment(sketch, "E1058", {"start": v(18.46, 4.55) * mm, "end": v(18.33, 4.45) * mm});
            skLineSegment(sketch, "E1059", {"start": v(18.33, 4.45) * mm, "end": v(18.2, 4.36) * mm});
            skLineSegment(sketch, "E1060", {"start": v(18.2, 4.36) * mm, "end": v(18.13, 4.3) * mm});
            skLineSegment(sketch, "E1061", {"start": v(18.13, 4.3) * mm, "end": v(18.1, 4.29) * mm});
            skLineSegment(sketch, "E1062", {"start": v(18.1, 4.29) * mm, "end": v(18.06, 4.26) * mm});
            skLineSegment(sketch, "E1063", {"start": v(18.06, 4.26) * mm, "end": v(18.17, 3.84) * mm});
            skLineSegment(sketch, "E1064", {"start": v(18.17, 3.84) * mm, "end": v(18.21, 3.84) * mm});
            skLineSegment(sketch, "E1065", {"start": v(18.21, 3.84) * mm, "end": v(18.25, 3.84) * mm});
            skLineSegment(sketch, "E1066", {"start": v(18.25, 3.84) * mm, "end": v(18.34, 3.84) * mm});
            skLineSegment(sketch, "E1067", {"start": v(18.34, 3.84) * mm, "end": v(18.5, 3.82) * mm});
            skLineSegment(sketch, "E1068", {"start": v(18.5, 3.82) * mm, "end": v(18.67, 3.8) * mm});
            skLineSegment(sketch, "E1069", {"start": v(18.67, 3.8) * mm, "end": v(18.84, 3.78) * mm});
            skLineSegment(sketch, "E1070", {"start": v(18.84, 3.78) * mm, "end": v(18.93, 3.37) * mm});
            skLineSegment(sketch, "E1071", {"start": v(18.93, 3.37) * mm, "end": v(18.79, 3.27) * mm});
            skLineSegment(sketch, "E1072", {"start": v(18.79, 3.27) * mm, "end": v(18.65, 3.18) * mm});
            skLineSegment(sketch, "E1073", {"start": v(18.65, 3.18) * mm, "end": v(18.5, 3.1) * mm});
            skLineSegment(sketch, "E1074", {"start": v(18.5, 3.1) * mm, "end": v(18.43, 3.06) * mm});
            skLineSegment(sketch, "E1075", {"start": v(18.43, 3.06) * mm, "end": v(18.4, 3.04) * mm});
            skLineSegment(sketch, "E1076", {"start": v(18.4, 3.04) * mm, "end": v(18.36, 3.02) * mm});
            skLineSegment(sketch, "E1077", {"start": v(18.36, 3.02) * mm, "end": v(18.44, 2.6) * mm});
            skLineSegment(sketch, "E1078", {"start": v(18.44, 2.6) * mm, "end": v(18.48, 2.59) * mm});
            skLineSegment(sketch, "E1079", {"start": v(18.48, 2.59) * mm, "end": v(18.52, 2.58) * mm});
            skLineSegment(sketch, "E1080", {"start": v(18.52, 2.58) * mm, "end": v(18.6, 2.57) * mm});
            skLineSegment(sketch, "E1081", {"start": v(18.6, 2.57) * mm, "end": v(18.76, 2.54) * mm});
            skLineSegment(sketch, "E1082", {"start": v(18.76, 2.54) * mm, "end": v(18.93, 2.5) * mm});
            skLineSegment(sketch, "E1083", {"start": v(18.93, 2.5) * mm, "end": v(19.1, 2.47) * mm});
            skLineSegment(sketch, "E1084", {"start": v(19.1, 2.47) * mm, "end": v(19.15, 2.05) * mm});
            skLineSegment(sketch, "E1085", {"start": v(19.15, 2.05) * mm, "end": v(19, 1.97) * mm});
            skLineSegment(sketch, "E1086", {"start": v(19, 1.97) * mm, "end": v(18.86, 1.9) * mm});
            skLineSegment(sketch, "E1087", {"start": v(18.86, 1.9) * mm, "end": v(18.7, 1.82) * mm});
            skLineSegment(sketch, "E1088", {"start": v(18.7, 1.82) * mm, "end": v(18.63, 1.79) * mm});
            skLineSegment(sketch, "E1089", {"start": v(18.63, 1.79) * mm, "end": v(18.6, 1.77) * mm});
            skLineSegment(sketch, "E1090", {"start": v(18.6, 1.77) * mm, "end": v(18.56, 1.75) * mm});
            skLineSegment(sketch, "E1091", {"start": v(18.56, 1.75) * mm, "end": v(18.6, 1.32) * mm});
            skLineSegment(sketch, "E1092", {"start": v(18.6, 1.32) * mm, "end": v(18.64, 1.31) * mm});
            skLineSegment(sketch, "E1093", {"start": v(18.64, 1.31) * mm, "end": v(18.68, 1.3) * mm});
            skLineSegment(sketch, "E1094", {"start": v(18.68, 1.3) * mm, "end": v(18.76, 1.28) * mm});
            skLineSegment(sketch, "E1095", {"start": v(18.76, 1.28) * mm, "end": v(18.92, 1.24) * mm});
            skLineSegment(sketch, "E1096", {"start": v(18.92, 1.24) * mm, "end": v(19.08, 1.2) * mm});
            skLineSegment(sketch, "E1097", {"start": v(19.08, 1.2) * mm, "end": v(19.24, 1.14) * mm});
            skLineSegment(sketch, "E1098", {"start": v(19.24, 1.14) * mm, "end": v(19.27, 0.72) * mm});
            skLineSegment(sketch, "E1099", {"start": v(19.27, 0.72) * mm, "end": v(19.11, 0.65) * mm});
            skLineSegment(sketch, "E1100", {"start": v(19.11, 0.65) * mm, "end": v(18.96, 0.59) * mm});
            skLineSegment(sketch, "E1101", {"start": v(18.96, 0.59) * mm, "end": v(18.8, 0.53) * mm});
            skLineSegment(sketch, "E1102", {"start": v(18.8, 0.53) * mm, "end": v(18.73, 0.5) * mm});
            skLineSegment(sketch, "E1103", {"start": v(18.73, 0.5) * mm, "end": v(18.69, 0.49) * mm});
            skLineSegment(sketch, "E1104", {"start": v(18.69, 0.49) * mm, "end": v(18.65, 0.47) * mm});
            skLineSegment(sketch, "E1105", {"start": v(18.65, 0.47) * mm, "end": v(18.66, 0.04) * mm});
            skLineSegment(sketch, "E1106", {"start": v(18.66, 0.04) * mm, "end": v(18.7, 0.03) * mm});
            skLineSegment(sketch, "E1107", {"start": v(18.7, 0.03) * mm, "end": v(18.73, 0.01) * mm});
            skLineSegment(sketch, "E1108", {"start": v(18.73, 0.01) * mm, "end": v(18.81, -0.01) * mm});
            skLineSegment(sketch, "E1109", {"start": v(18.81, -0.01) * mm, "end": v(18.97, -0.07) * mm});
            skLineSegment(sketch, "E1110", {"start": v(18.97, -0.07) * mm, "end": v(19.13, -0.13) * mm});
            skLineSegment(sketch, "E1111", {"start": v(19.13, -0.13) * mm, "end": v(19.28, -0.2) * mm});
            skLineSegment(sketch, "E1112", {"start": v(19.28, -0.2) * mm, "end": v(19.27, -0.6) * mm});
            skLineSegment(sketch, "E1113", {"start": v(19.27, -0.6) * mm, "end": v(19.11, -0.67) * mm});
            skLineSegment(sketch, "E1114", {"start": v(19.11, -0.67) * mm, "end": v(18.95, -0.72) * mm});
            skLineSegment(sketch, "E1115", {"start": v(18.95, -0.72) * mm, "end": v(18.8, -0.77) * mm});
            skLineSegment(sketch, "E1116", {"start": v(18.8, -0.77) * mm, "end": v(18.71, -0.79) * mm});
            skLineSegment(sketch, "E1117", {"start": v(18.71, -0.79) * mm, "end": v(18.67, -0.8) * mm});
            skLineSegment(sketch, "E1118", {"start": v(18.67, -0.8) * mm, "end": v(18.63, -0.8) * mm});
            skLineSegment(sketch, "E1119", {"start": v(18.63, -0.8) * mm, "end": v(18.6, -1.24) * mm});
            skLineSegment(sketch, "E1120", {"start": v(18.6, -1.24) * mm, "end": v(18.64, -1.26) * mm});
            skLineSegment(sketch, "E1121", {"start": v(18.64, -1.26) * mm, "end": v(18.68, -1.27) * mm});
            skLineSegment(sketch, "E1122", {"start": v(18.68, -1.27) * mm, "end": v(18.76, -1.3) * mm});
            skLineSegment(sketch, "E1123", {"start": v(18.76, -1.3) * mm, "end": v(18.9, -1.37) * mm});
            skLineSegment(sketch, "E1124", {"start": v(18.9, -1.37) * mm, "end": v(19.06, -1.44) * mm});
            skLineSegment(sketch, "E1125", {"start": v(19.06, -1.44) * mm, "end": v(19.21, -1.52) * mm});
            skLineSegment(sketch, "E1126", {"start": v(19.21, -1.52) * mm, "end": v(19.17, -1.94) * mm});
            skLineSegment(sketch, "E1127", {"start": v(19.17, -1.94) * mm, "end": v(19, -1.98) * mm});
            skLineSegment(sketch, "E1128", {"start": v(19, -1.98) * mm, "end": v(18.84, -2.02) * mm});
            skLineSegment(sketch, "E1129", {"start": v(18.84, -2.02) * mm, "end": v(18.68, -2.06) * mm});
            skLineSegment(sketch, "E1130", {"start": v(18.68, -2.06) * mm, "end": v(18.6, -2.07) * mm});
            skLineSegment(sketch, "E1131", {"start": v(18.6, -2.07) * mm, "end": v(18.56, -2.08) * mm});
            skLineSegment(sketch, "E1132", {"start": v(18.56, -2.08) * mm, "end": v(18.51, -2.08) * mm});
            skLineSegment(sketch, "E1133", {"start": v(18.51, -2.08) * mm, "end": v(18.45, -2.51) * mm});
            skLineSegment(sketch, "E1134", {"start": v(18.45, -2.51) * mm, "end": v(18.49, -2.53) * mm});
            skLineSegment(sketch, "E1135", {"start": v(18.49, -2.53) * mm, "end": v(18.52, -2.55) * mm});
            skLineSegment(sketch, "E1136", {"start": v(18.52, -2.55) * mm, "end": v(18.6, -2.59) * mm});
            skLineSegment(sketch, "E1137", {"start": v(18.6, -2.59) * mm, "end": v(18.74, -2.67) * mm});
            skLineSegment(sketch, "E1138", {"start": v(18.74, -2.67) * mm, "end": v(18.89, -2.75) * mm});
            skLineSegment(sketch, "E1139", {"start": v(18.89, -2.75) * mm, "end": v(19.03, -2.84) * mm});
            skLineSegment(sketch, "E1140", {"start": v(19.03, -2.84) * mm, "end": v(18.95, -3.25) * mm});
            skLineSegment(sketch, "E1141", {"start": v(18.95, -3.25) * mm, "end": v(18.78, -3.29) * mm});
            skLineSegment(sketch, "E1142", {"start": v(18.78, -3.29) * mm, "end": v(18.62, -3.31) * mm});
            skLineSegment(sketch, "E1143", {"start": v(18.62, -3.31) * mm, "end": v(18.45, -3.33) * mm});
            skLineSegment(sketch, "E1144", {"start": v(18.45, -3.33) * mm, "end": v(18.37, -3.34) * mm});
            skLineSegment(sketch, "E1145", {"start": v(18.37, -3.34) * mm, "end": v(18.33, -3.34) * mm});
            skLineSegment(sketch, "E1146", {"start": v(18.33, -3.34) * mm, "end": v(18.3, -3.35) * mm});
            skLineSegment(sketch, "E1147", {"start": v(18.3, -3.35) * mm, "end": v(18.2, -3.77) * mm});
            skLineSegment(sketch, "E1148", {"start": v(18.2, -3.77) * mm, "end": v(18.23, -3.8) * mm});
            skLineSegment(sketch, "E1149", {"start": v(18.23, -3.8) * mm, "end": v(18.26, -3.81) * mm});
            skLineSegment(sketch, "E1150", {"start": v(18.26, -3.81) * mm, "end": v(18.33, -3.86) * mm});
            skLineSegment(sketch, "E1151", {"start": v(18.33, -3.86) * mm, "end": v(18.47, -3.95) * mm});
            skLineSegment(sketch, "E1152", {"start": v(18.47, -3.95) * mm, "end": v(18.6, -4.04) * mm});
            skLineSegment(sketch, "E1153", {"start": v(18.6, -4.04) * mm, "end": v(18.74, -4.15) * mm});
            skLineSegment(sketch, "E1154", {"start": v(18.74, -4.15) * mm, "end": v(18.63, -4.55) * mm});
            skLineSegment(sketch, "E1155", {"start": v(18.63, -4.55) * mm, "end": v(18.46, -4.57) * mm});
            skLineSegment(sketch, "E1156", {"start": v(18.46, -4.57) * mm, "end": v(18.3, -4.58) * mm});
            skLineSegment(sketch, "E1157", {"start": v(18.3, -4.58) * mm, "end": v(18.13, -4.58) * mm});
            skLineSegment(sketch, "E1158", {"start": v(18.13, -4.58) * mm, "end": v(18.04, -4.59) * mm});
            skLineSegment(sketch, "E1159", {"start": v(18.04, -4.59) * mm, "end": v(18, -4.59) * mm});
            skLineSegment(sketch, "E1160", {"start": v(18, -4.59) * mm, "end": v(17.96, -4.59) * mm});
            skLineSegment(sketch, "E1161", {"start": v(17.96, -4.59) * mm, "end": v(17.83, -5) * mm});
            skLineSegment(sketch, "E1162", {"start": v(17.83, -5) * mm, "end": v(17.86, -5.02) * mm});
            skLineSegment(sketch, "E1163", {"start": v(17.86, -5.02) * mm, "end": v(17.9, -5.05) * mm});
            skLineSegment(sketch, "E1164", {"start": v(17.9, -5.05) * mm, "end": v(17.96, -5.1) * mm});
            skLineSegment(sketch, "E1165", {"start": v(17.96, -5.1) * mm, "end": v(18.1, -5.2) * mm});
            skLineSegment(sketch, "E1166", {"start": v(18.1, -5.2) * mm, "end": v(18.22, -5.3) * mm});
            skLineSegment(sketch, "E1167", {"start": v(18.22, -5.3) * mm, "end": v(18.35, -5.42) * mm});
            skLineSegment(sketch, "E1168", {"start": v(18.35, -5.42) * mm, "end": v(18.2, -5.81) * mm});
            skLineSegment(sketch, "E1169", {"start": v(18.2, -5.81) * mm, "end": v(18.03, -5.81) * mm});
            skLineSegment(sketch, "E1170", {"start": v(18.03, -5.81) * mm, "end": v(17.86, -5.81) * mm});
            skLineSegment(sketch, "E1171", {"start": v(17.86, -5.81) * mm, "end": v(17.7, -5.8) * mm});
            skLineSegment(sketch, "E1172", {"start": v(17.7, -5.8) * mm, "end": v(17.61, -5.8) * mm});
            skLineSegment(sketch, "E1173", {"start": v(17.61, -5.8) * mm, "end": v(17.57, -5.8) * mm});
            skLineSegment(sketch, "E1174", {"start": v(17.57, -5.8) * mm, "end": v(17.53, -5.8) * mm});
            skLineSegment(sketch, "E1175", {"start": v(17.53, -5.8) * mm, "end": v(17.36, -6.2) * mm});
            skLineSegment(sketch, "E1176", {"start": v(17.36, -6.2) * mm, "end": v(17.4, -6.22) * mm});
            skLineSegment(sketch, "E1177", {"start": v(17.4, -6.22) * mm, "end": v(17.43, -6.25) * mm});
            skLineSegment(sketch, "E1178", {"start": v(17.43, -6.25) * mm, "end": v(17.49, -6.3) * mm});
            skLineSegment(sketch, "E1179", {"start": v(17.49, -6.3) * mm, "end": v(17.61, -6.42) * mm});
            skLineSegment(sketch, "E1180", {"start": v(17.61, -6.42) * mm, "end": v(17.73, -6.53) * mm});
            skLineSegment(sketch, "E1181", {"start": v(17.73, -6.53) * mm, "end": v(17.85, -6.66) * mm});
            skLineSegment(sketch, "E1182", {"start": v(17.85, -6.66) * mm, "end": v(17.67, -7.03) * mm});
            skLineSegment(sketch, "E1183", {"start": v(17.67, -7.03) * mm, "end": v(17.5, -7.02) * mm});
            skLineSegment(sketch, "E1184", {"start": v(17.5, -7.02) * mm, "end": v(17.33, -7) * mm});
            skLineSegment(sketch, "E1185", {"start": v(17.33, -7) * mm, "end": v(17.17, -6.99) * mm});
            skLineSegment(sketch, "E1186", {"start": v(17.17, -6.99) * mm, "end": v(17.09, -6.97) * mm});
            skLineSegment(sketch, "E1187", {"start": v(17.09, -6.97) * mm, "end": v(17.05, -6.97) * mm});
            skLineSegment(sketch, "E1188", {"start": v(17.05, -6.97) * mm, "end": v(17, -6.96) * mm});
            skLineSegment(sketch, "E1189", {"start": v(17, -6.96) * mm, "end": v(16.8, -7.35) * mm});
            skLineSegment(sketch, "E1190", {"start": v(16.8, -7.35) * mm, "end": v(16.83, -7.38) * mm});
            skLineSegment(sketch, "E1191", {"start": v(16.83, -7.38) * mm, "end": v(16.86, -7.4) * mm});
            skLineSegment(sketch, "E1192", {"start": v(16.86, -7.4) * mm, "end": v(16.92, -7.47) * mm});
            skLineSegment(sketch, "E1193", {"start": v(16.92, -7.47) * mm, "end": v(17.03, -7.59) * mm});
            skLineSegment(sketch, "E1194", {"start": v(17.03, -7.59) * mm, "end": v(17.14, -7.72) * mm});
            skLineSegment(sketch, "E1195", {"start": v(17.14, -7.72) * mm, "end": v(17.25, -7.85) * mm});
            skLineSegment(sketch, "E1196", {"start": v(17.25, -7.85) * mm, "end": v(17.04, -8.21) * mm});
            skLineSegment(sketch, "E1197", {"start": v(17.04, -8.21) * mm, "end": v(16.87, -8.19) * mm});
            skLineSegment(sketch, "E1198", {"start": v(16.87, -8.19) * mm, "end": v(16.7, -8.16) * mm});
            skLineSegment(sketch, "E1199", {"start": v(16.7, -8.16) * mm, "end": v(16.54, -8.12) * mm});
            skLineSegment(sketch, "E1200", {"start": v(16.54, -8.12) * mm, "end": v(16.46, -8.1) * mm});
            skLineSegment(sketch, "E1201", {"start": v(16.46, -8.1) * mm, "end": v(16.42, -8.1) * mm});
            skLineSegment(sketch, "E1202", {"start": v(16.42, -8.1) * mm, "end": v(16.38, -8.08) * mm});
            skLineSegment(sketch, "E1203", {"start": v(16.38, -8.08) * mm, "end": v(16.15, -8.45) * mm});
            skLineSegment(sketch, "E1204", {"start": v(16.15, -8.45) * mm, "end": v(16.18, -8.48) * mm});
            skLineSegment(sketch, "E1205", {"start": v(16.18, -8.48) * mm, "end": v(16.2, -8.51) * mm});
            skLineSegment(sketch, "E1206", {"start": v(16.2, -8.51) * mm, "end": v(16.26, -8.58) * mm});
            skLineSegment(sketch, "E1207", {"start": v(16.26, -8.58) * mm, "end": v(16.36, -8.7) * mm});
            skLineSegment(sketch, "E1208", {"start": v(16.36, -8.7) * mm, "end": v(16.46, -8.84) * mm});
            skLineSegment(sketch, "E1209", {"start": v(16.46, -8.84) * mm, "end": v(16.55, -8.99) * mm});
            skLineSegment(sketch, "E1210", {"start": v(16.55, -8.99) * mm, "end": v(16.31, -9.33) * mm});
            skLineSegment(sketch, "E1211", {"start": v(16.31, -9.33) * mm, "end": v(16.15, -9.3) * mm});
            skLineSegment(sketch, "E1212", {"start": v(16.15, -9.3) * mm, "end": v(15.99, -9.25) * mm});
            skLineSegment(sketch, "E1213", {"start": v(15.99, -9.25) * mm, "end": v(15.83, -9.2) * mm});
            skLineSegment(sketch, "E1214", {"start": v(15.83, -9.2) * mm, "end": v(15.75, -9.17) * mm});
            skLineSegment(sketch, "E1215", {"start": v(15.75, -9.17) * mm, "end": v(15.7, -9.16) * mm});
            skLineSegment(sketch, "E1216", {"start": v(15.7, -9.16) * mm, "end": v(15.67, -9.15) * mm});
            skLineSegment(sketch, "E1217", {"start": v(15.67, -9.15) * mm, "end": v(15.4, -9.5) * mm});
            skLineSegment(sketch, "E1218", {"start": v(15.4, -9.5) * mm, "end": v(15.43, -9.53) * mm});
            skLineSegment(sketch, "E1219", {"start": v(15.43, -9.53) * mm, "end": v(15.46, -9.56) * mm});
            skLineSegment(sketch, "E1220", {"start": v(15.46, -9.56) * mm, "end": v(15.5, -9.63) * mm});
            skLineSegment(sketch, "E1221", {"start": v(15.5, -9.63) * mm, "end": v(15.6, -9.77) * mm});
            skLineSegment(sketch, "E1222", {"start": v(15.6, -9.77) * mm, "end": v(15.68, -9.91) * mm});
            skLineSegment(sketch, "E1223", {"start": v(15.68, -9.91) * mm, "end": v(15.76, -10.06) * mm});
            skLineSegment(sketch, "E1224", {"start": v(15.76, -10.06) * mm, "end": v(15.5, -10.38) * mm});
            skLineSegment(sketch, "E1225", {"start": v(15.5, -10.38) * mm, "end": v(15.34, -10.33) * mm});
            skLineSegment(sketch, "E1226", {"start": v(15.34, -10.33) * mm, "end": v(15.18, -10.28) * mm});
            skLineSegment(sketch, "E1227", {"start": v(15.18, -10.28) * mm, "end": v(15.02, -10.22) * mm});
            skLineSegment(sketch, "E1228", {"start": v(15.02, -10.22) * mm, "end": v(14.95, -10.18) * mm});
            skLineSegment(sketch, "E1229", {"start": v(14.95, -10.18) * mm, "end": v(14.91, -10.17) * mm});
            skLineSegment(sketch, "E1230", {"start": v(14.91, -10.17) * mm, "end": v(14.87, -10.15) * mm});
            skLineSegment(sketch, "E1231", {"start": v(14.87, -10.15) * mm, "end": v(14.58, -10.48) * mm});
            skLineSegment(sketch, "E1232", {"start": v(14.58, -10.48) * mm, "end": v(14.6, -10.51) * mm});
            skLineSegment(sketch, "E1233", {"start": v(14.6, -10.51) * mm, "end": v(14.62, -10.55) * mm});
            skLineSegment(sketch, "E1234", {"start": v(14.62, -10.55) * mm, "end": v(14.67, -10.62) * mm});
            skLineSegment(sketch, "E1235", {"start": v(14.67, -10.62) * mm, "end": v(14.74, -10.76) * mm});
            skLineSegment(sketch, "E1236", {"start": v(14.74, -10.76) * mm, "end": v(14.82, -10.91) * mm});
            skLineSegment(sketch, "E1237", {"start": v(14.82, -10.91) * mm, "end": v(14.89, -11.07) * mm});
            skLineSegment(sketch, "E1238", {"start": v(14.89, -11.07) * mm, "end": v(14.6, -11.37) * mm});
            skLineSegment(sketch, "E1239", {"start": v(14.6, -11.37) * mm, "end": v(14.44, -11.3) * mm});
            skLineSegment(sketch, "E1240", {"start": v(14.44, -11.3) * mm, "end": v(14.29, -11.23) * mm});
            skLineSegment(sketch, "E1241", {"start": v(14.29, -11.23) * mm, "end": v(14.14, -11.16) * mm});
            skLineSegment(sketch, "E1242", {"start": v(14.14, -11.16) * mm, "end": v(14.07, -11.12) * mm});
            skLineSegment(sketch, "E1243", {"start": v(14.07, -11.12) * mm, "end": v(14.03, -11.1) * mm});
            skLineSegment(sketch, "E1244", {"start": v(14.03, -11.1) * mm, "end": v(14, -11.08) * mm});
            skLineSegment(sketch, "E1245", {"start": v(14, -11.08) * mm, "end": v(13.68, -11.38) * mm});
            skLineSegment(sketch, "E1246", {"start": v(13.68, -11.38) * mm, "end": v(13.7, -11.42) * mm});
            skLineSegment(sketch, "E1247", {"start": v(13.7, -11.42) * mm, "end": v(13.71, -11.46) * mm});
            skLineSegment(sketch, "E1248", {"start": v(13.71, -11.46) * mm, "end": v(13.75, -11.53) * mm});
            skLineSegment(sketch, "E1249", {"start": v(13.75, -11.53) * mm, "end": v(13.81, -11.69) * mm});
            skLineSegment(sketch, "E1250", {"start": v(13.81, -11.69) * mm, "end": v(13.88, -11.84) * mm});
            skLineSegment(sketch, "E1251", {"start": v(13.88, -11.84) * mm, "end": v(13.93, -12) * mm});
            skLineSegment(sketch, "E1252", {"start": v(13.93, -12) * mm, "end": v(13.62, -12.28) * mm});
            skLineSegment(sketch, "E1253", {"start": v(13.62, -12.28) * mm, "end": v(13.47, -12.2) * mm});
            skLineSegment(sketch, "E1254", {"start": v(13.47, -12.2) * mm, "end": v(13.32, -12.12) * mm});
            skLineSegment(sketch, "E1255", {"start": v(13.32, -12.12) * mm, "end": v(13.18, -12.03) * mm});
            skLineSegment(sketch, "E1256", {"start": v(13.18, -12.03) * mm, "end": v(13.11, -11.99) * mm});
            skLineSegment(sketch, "E1257", {"start": v(13.11, -11.99) * mm, "end": v(13.08, -11.96) * mm});
            skLineSegment(sketch, "E1258", {"start": v(13.08, -11.96) * mm, "end": v(13.04, -11.94) * mm});
            skLineSegment(sketch, "E1259", {"start": v(13.04, -11.94) * mm, "end": v(12.7, -12.21) * mm});
            skLineSegment(sketch, "E1260", {"start": v(12.7, -12.21) * mm, "end": v(12.72, -12.25) * mm});
            skLineSegment(sketch, "E1261", {"start": v(12.72, -12.25) * mm, "end": v(12.73, -12.3) * mm});
            skLineSegment(sketch, "E1262", {"start": v(12.73, -12.3) * mm, "end": v(12.76, -12.37) * mm});
            skLineSegment(sketch, "E1263", {"start": v(12.76, -12.37) * mm, "end": v(12.81, -12.53) * mm});
            skLineSegment(sketch, "E1264", {"start": v(12.81, -12.53) * mm, "end": v(12.86, -12.69) * mm});
            skLineSegment(sketch, "E1265", {"start": v(12.86, -12.69) * mm, "end": v(12.9, -12.85) * mm});
            skLineSegment(sketch, "E1266", {"start": v(12.9, -12.85) * mm, "end": v(12.57, -13.1) * mm});
            skLineSegment(sketch, "E1267", {"start": v(12.57, -13.1) * mm, "end": v(12.43, -13) * mm});
            skLineSegment(sketch, "E1268", {"start": v(12.43, -13) * mm, "end": v(12.29, -12.92) * mm});
            skLineSegment(sketch, "E1269", {"start": v(12.29, -12.92) * mm, "end": v(12.15, -12.82) * mm});
            skLineSegment(sketch, "E1270", {"start": v(12.15, -12.82) * mm, "end": v(12.09, -12.77) * mm});
            skLineSegment(sketch, "E1271", {"start": v(12.09, -12.77) * mm, "end": v(12.05, -12.74) * mm});
            skLineSegment(sketch, "E1272", {"start": v(12.05, -12.74) * mm, "end": v(12.02, -12.72) * mm});
            skLineSegment(sketch, "E1273", {"start": v(12.02, -12.72) * mm, "end": v(11.66, -12.96) * mm});
            skLineSegment(sketch, "E1274", {"start": v(11.66, -12.96) * mm, "end": v(11.67, -13) * mm});
            skLineSegment(sketch, "E1275", {"start": v(11.67, -13) * mm, "end": v(11.68, -13.04) * mm});
            skLineSegment(sketch, "E1276", {"start": v(11.68, -13.04) * mm, "end": v(11.7, -13.12) * mm});
            skLineSegment(sketch, "E1277", {"start": v(11.7, -13.12) * mm, "end": v(11.75, -13.28) * mm});
            skLineSegment(sketch, "E1278", {"start": v(11.75, -13.28) * mm, "end": v(11.78, -13.45) * mm});
            skLineSegment(sketch, "E1279", {"start": v(11.78, -13.45) * mm, "end": v(11.81, -13.61) * mm});
            skLineSegment(sketch, "E1280", {"start": v(11.81, -13.61) * mm, "end": v(11.46, -13.83) * mm});
            skLineSegment(sketch, "E1281", {"start": v(11.46, -13.83) * mm, "end": v(11.32, -13.73) * mm});
            skLineSegment(sketch, "E1282", {"start": v(11.32, -13.73) * mm, "end": v(11.19, -13.63) * mm});
            skLineSegment(sketch, "E1283", {"start": v(11.19, -13.63) * mm, "end": v(11.06, -13.52) * mm});
            skLineSegment(sketch, "E1284", {"start": v(11.06, -13.52) * mm, "end": v(11, -13.46) * mm});
            skLineSegment(sketch, "E1285", {"start": v(11, -13.46) * mm, "end": v(10.97, -13.44) * mm});
            skLineSegment(sketch, "E1286", {"start": v(10.97, -13.44) * mm, "end": v(10.94, -13.4) * mm});
            skLineSegment(sketch, "E1287", {"start": v(10.94, -13.4) * mm, "end": v(10.56, -13.62) * mm});
            skLineSegment(sketch, "E1288", {"start": v(10.56, -13.62) * mm, "end": v(10.57, -13.66) * mm});
            skLineSegment(sketch, "E1289", {"start": v(10.57, -13.66) * mm, "end": v(10.58, -13.7) * mm});
            skLineSegment(sketch, "E1290", {"start": v(10.58, -13.7) * mm, "end": v(10.6, -13.78) * mm});
            skLineSegment(sketch, "E1291", {"start": v(10.6, -13.78) * mm, "end": v(10.62, -13.95) * mm});
            skLineSegment(sketch, "E1292", {"start": v(10.62, -13.95) * mm, "end": v(10.64, -14.11) * mm});
            skLineSegment(sketch, "E1293", {"start": v(10.64, -14.11) * mm, "end": v(10.66, -14.28) * mm});
            skLineSegment(sketch, "E1294", {"start": v(10.66, -14.28) * mm, "end": v(10.29, -14.47) * mm});
            skLineSegment(sketch, "E1295", {"start": v(10.29, -14.47) * mm, "end": v(10.16, -14.36) * mm});
            skLineSegment(sketch, "E1296", {"start": v(10.16, -14.36) * mm, "end": v(10.04, -14.24) * mm});
            skLineSegment(sketch, "E1297", {"start": v(10.04, -14.24) * mm, "end": v(9.92, -14.13) * mm});
            skLineSegment(sketch, "E1298", {"start": v(9.92, -14.13) * mm, "end": v(9.86, -14.07) * mm});
            skLineSegment(sketch, "E1299", {"start": v(9.86, -14.07) * mm, "end": v(9.84, -14.04) * mm});
            skLineSegment(sketch, "E1300", {"start": v(9.84, -14.04) * mm, "end": v(9.8, -14) * mm});
            skLineSegment(sketch, "E1301", {"start": v(9.8, -14) * mm, "end": v(9.41, -14.19) * mm});
            skLineSegment(sketch, "E1302", {"start": v(9.41, -14.19) * mm, "end": v(9.42, -14.23) * mm});
            skLineSegment(sketch, "E1303", {"start": v(9.42, -14.23) * mm, "end": v(9.42, -14.27) * mm});
            skLineSegment(sketch, "E1304", {"start": v(9.42, -14.27) * mm, "end": v(9.43, -14.35) * mm});
            skLineSegment(sketch, "E1305", {"start": v(9.43, -14.35) * mm, "end": v(9.44, -14.52) * mm});
            skLineSegment(sketch, "E1306", {"start": v(9.44, -14.52) * mm, "end": v(9.45, -14.68) * mm});
            skLineSegment(sketch, "E1307", {"start": v(9.45, -14.68) * mm, "end": v(9.45, -14.85) * mm});
            skLineSegment(sketch, "E1308", {"start": v(9.45, -14.85) * mm, "end": v(9.07, -15.01) * mm});
            skLineSegment(sketch, "E1309", {"start": v(9.07, -15.01) * mm, "end": v(8.95, -14.89) * mm});
            skLineSegment(sketch, "E1310", {"start": v(8.95, -14.89) * mm, "end": v(8.84, -14.76) * mm});
            skLineSegment(sketch, "E1311", {"start": v(8.84, -14.76) * mm, "end": v(8.73, -14.64) * mm});
            skLineSegment(sketch, "E1312", {"start": v(8.73, -14.64) * mm, "end": v(8.68, -14.57) * mm});
            skLineSegment(sketch, "E1313", {"start": v(8.68, -14.57) * mm, "end": v(8.65, -14.54) * mm});
            skLineSegment(sketch, "E1314", {"start": v(8.65, -14.54) * mm, "end": v(8.63, -14.5) * mm});
            skLineSegment(sketch, "E1315", {"start": v(8.63, -14.5) * mm, "end": v(8.22, -14.66) * mm});
            skLineSegment(sketch, "E1316", {"start": v(8.22, -14.66) * mm, "end": v(8.22, -14.7) * mm});
            skLineSegment(sketch, "E1317", {"start": v(8.22, -14.7) * mm, "end": v(8.22, -14.74) * mm});
            skLineSegment(sketch, "E1318", {"start": v(8.22, -14.74) * mm, "end": v(8.22, -14.82) * mm});
            skLineSegment(sketch, "E1319", {"start": v(8.22, -14.82) * mm, "end": v(8.22, -14.99) * mm});
            skLineSegment(sketch, "E1320", {"start": v(8.22, -14.99) * mm, "end": v(8.22, -15.15) * mm});
            skLineSegment(sketch, "E1321", {"start": v(8.22, -15.15) * mm, "end": v(8.2, -15.32) * mm});
            skLineSegment(sketch, "E1322", {"start": v(8.2, -15.32) * mm, "end": v(7.8, -15.45) * mm});
            skLineSegment(sketch, "E1323", {"start": v(7.8, -15.45) * mm, "end": v(7.7, -15.32) * mm});
            skLineSegment(sketch, "E1324", {"start": v(7.7, -15.32) * mm, "end": v(7.6, -15.18) * mm});
            skLineSegment(sketch, "E1325", {"start": v(7.6, -15.18) * mm, "end": v(7.5, -15.05) * mm});
            skLineSegment(sketch, "E1326", {"start": v(7.5, -15.05) * mm, "end": v(7.46, -14.98) * mm});
            skLineSegment(sketch, "E1327", {"start": v(7.46, -14.98) * mm, "end": v(7.43, -14.95) * mm});
            skLineSegment(sketch, "E1328", {"start": v(7.43, -14.95) * mm, "end": v(7.41, -14.91) * mm});
            skLineSegment(sketch, "E1329", {"start": v(7.41, -14.91) * mm, "end": v(7, -15.02) * mm});
            skLineSegment(sketch, "E1330", {"start": v(7, -15.02) * mm, "end": v(6.99, -15.07) * mm});
            skLineSegment(sketch, "E1331", {"start": v(6.99, -15.07) * mm, "end": v(6.99, -15.1) * mm});
            skLineSegment(sketch, "E1332", {"start": v(6.99, -15.1) * mm, "end": v(6.98, -15.19) * mm});
            skLineSegment(sketch, "E1333", {"start": v(6.98, -15.19) * mm, "end": v(6.97, -15.35) * mm});
            skLineSegment(sketch, "E1334", {"start": v(6.97, -15.35) * mm, "end": v(6.95, -15.52) * mm});
            skLineSegment(sketch, "E1335", {"start": v(6.95, -15.52) * mm, "end": v(6.92, -15.69) * mm});
            skLineSegment(sketch, "E1336", {"start": v(6.92, -15.69) * mm, "end": v(6.51, -15.78) * mm});
            skLineSegment(sketch, "E1337", {"start": v(6.51, -15.78) * mm, "end": v(6.42, -15.64) * mm});
            skLineSegment(sketch, "E1338", {"start": v(6.42, -15.64) * mm, "end": v(6.33, -15.5) * mm});
            skLineSegment(sketch, "E1339", {"start": v(6.33, -15.5) * mm, "end": v(6.25, -15.36) * mm});
            skLineSegment(sketch, "E1340", {"start": v(6.25, -15.36) * mm, "end": v(6.2, -15.28) * mm});
            skLineSegment(sketch, "E1341", {"start": v(6.2, -15.28) * mm, "end": v(6.19, -15.25) * mm});
            skLineSegment(sketch, "E1342", {"start": v(6.19, -15.25) * mm, "end": v(6.17, -15.21) * mm});
            skLineSegment(sketch, "E1343", {"start": v(6.17, -15.21) * mm, "end": v(5.74, -15.3) * mm});
            skLineSegment(sketch, "E1344", {"start": v(5.74, -15.3) * mm, "end": v(5.73, -15.33) * mm});
            skLineSegment(sketch, "E1345", {"start": v(5.73, -15.33) * mm, "end": v(5.73, -15.37) * mm});
            skLineSegment(sketch, "E1346", {"start": v(5.73, -15.37) * mm, "end": v(5.72, -15.45) * mm});
            skLineSegment(sketch, "E1347", {"start": v(5.72, -15.45) * mm, "end": v(5.69, -15.62) * mm});
            skLineSegment(sketch, "E1348", {"start": v(5.69, -15.62) * mm, "end": v(5.65, -15.78) * mm});
            skLineSegment(sketch, "E1349", {"start": v(5.65, -15.78) * mm, "end": v(5.61, -15.95) * mm});
            skLineSegment(sketch, "E1350", {"start": v(5.61, -15.95) * mm, "end": v(5.2, -16) * mm});
            skLineSegment(sketch, "E1351", {"start": v(5.2, -16) * mm, "end": v(5.12, -15.86) * mm});
            skLineSegment(sketch, "E1352", {"start": v(5.12, -15.86) * mm, "end": v(5.04, -15.7) * mm});
            skLineSegment(sketch, "E1353", {"start": v(5.04, -15.7) * mm, "end": v(4.97, -15.56) * mm});
            skLineSegment(sketch, "E1354", {"start": v(4.97, -15.56) * mm, "end": v(4.93, -15.48) * mm});
            skLineSegment(sketch, "E1355", {"start": v(4.93, -15.48) * mm, "end": v(4.92, -15.45) * mm});
            skLineSegment(sketch, "E1356", {"start": v(4.92, -15.45) * mm, "end": v(4.9, -15.4) * mm});
            skLineSegment(sketch, "E1357", {"start": v(4.9, -15.4) * mm, "end": v(4.47, -15.45) * mm});
            skLineSegment(sketch, "E1358", {"start": v(4.47, -15.45) * mm, "end": v(4.46, -15.5) * mm});
            skLineSegment(sketch, "E1359", {"start": v(4.46, -15.5) * mm, "end": v(4.45, -15.53) * mm});
            skLineSegment(sketch, "E1360", {"start": v(4.45, -15.53) * mm, "end": v(4.43, -15.61) * mm});
            skLineSegment(sketch, "E1361", {"start": v(4.43, -15.61) * mm, "end": v(4.39, -15.77) * mm});
            skLineSegment(sketch, "E1362", {"start": v(4.39, -15.77) * mm, "end": v(4.34, -15.93) * mm});
            skLineSegment(sketch, "E1363", {"start": v(4.34, -15.93) * mm, "end": v(4.29, -16.1) * mm});
            skLineSegment(sketch, "E1364", {"start": v(4.29, -16.1) * mm, "end": v(3.87, -16.12) * mm});
            skLineSegment(sketch, "E1365", {"start": v(3.87, -16.12) * mm, "end": v(3.8, -15.97) * mm});
            skLineSegment(sketch, "E1366", {"start": v(3.8, -15.97) * mm, "end": v(3.74, -15.81) * mm});
            skLineSegment(sketch, "E1367", {"start": v(3.74, -15.81) * mm, "end": v(3.68, -15.66) * mm});
            skLineSegment(sketch, "E1368", {"start": v(3.68, -15.66) * mm, "end": v(3.65, -15.58) * mm});
            skLineSegment(sketch, "E1369", {"start": v(3.65, -15.58) * mm, "end": v(3.63, -15.54) * mm});
            skLineSegment(sketch, "E1370", {"start": v(3.63, -15.54) * mm, "end": v(3.62, -15.5) * mm});
            skLineSegment(sketch, "E1371", {"start": v(3.62, -15.5) * mm, "end": v(3.19, -15.5) * mm});
            skLineSegment(sketch, "E1372", {"start": v(3.19, -15.5) * mm, "end": v(3.17, -15.55) * mm});
            skLineSegment(sketch, "E1373", {"start": v(3.17, -15.55) * mm, "end": v(3.16, -15.59) * mm});
            skLineSegment(sketch, "E1374", {"start": v(3.16, -15.59) * mm, "end": v(3.14, -15.67) * mm});
            skLineSegment(sketch, "E1375", {"start": v(3.14, -15.67) * mm, "end": v(3.08, -15.82) * mm});
            skLineSegment(sketch, "E1376", {"start": v(3.08, -15.82) * mm, "end": v(3.02, -15.98) * mm});
            skLineSegment(sketch, "E1377", {"start": v(3.02, -15.98) * mm, "end": v(2.96, -16.14) * mm});
            skLineSegment(sketch, "E1378", {"start": v(2.96, -16.14) * mm, "end": v(2.54, -16.12) * mm});
            skLineSegment(sketch, "E1379", {"start": v(2.54, -16.12) * mm, "end": v(2.48, -15.97) * mm});
            skLineSegment(sketch, "E1380", {"start": v(2.48, -15.97) * mm, "end": v(2.43, -15.8) * mm});
            skLineSegment(sketch, "E1381", {"start": v(2.43, -15.8) * mm, "end": v(2.38, -15.65) * mm});
            skLineSegment(sketch, "E1382", {"start": v(2.38, -15.65) * mm, "end": v(2.36, -15.57) * mm});
            skLineSegment(sketch, "E1383", {"start": v(2.36, -15.57) * mm, "end": v(2.35, -15.53) * mm});
            skLineSegment(sketch, "E1384", {"start": v(2.35, -15.53) * mm, "end": v(2.34, -15.49) * mm});
            skLineSegment(sketch, "E1385", {"start": v(2.34, -15.49) * mm, "end": v(1.9, -15.46) * mm});
            skLineSegment(sketch, "E1386", {"start": v(1.9, -15.46) * mm, "end": v(1.89, -15.5) * mm});
            skLineSegment(sketch, "E1387", {"start": v(1.89, -15.5) * mm, "end": v(1.87, -15.54) * mm});
            skLineSegment(sketch, "E1388", {"start": v(1.87, -15.54) * mm, "end": v(1.84, -15.61) * mm});
            skLineSegment(sketch, "E1389", {"start": v(1.84, -15.61) * mm, "end": v(1.78, -15.76) * mm});
            skLineSegment(sketch, "E1390", {"start": v(1.78, -15.76) * mm, "end": v(1.7, -15.91) * mm});
            skLineSegment(sketch, "E1391", {"start": v(1.7, -15.91) * mm, "end": v(1.62, -16.06) * mm});
            skLineSegment(sketch, "E1392", {"start": v(1.62, -16.06) * mm, "end": v(1.2, -16.02) * mm});
            skLineSegment(sketch, "E1393", {"start": v(1.2, -16.02) * mm, "end": v(1.16, -15.86) * mm});
            skLineSegment(sketch, "E1394", {"start": v(1.16, -15.86) * mm, "end": v(1.12, -15.7) * mm});
            skLineSegment(sketch, "E1395", {"start": v(1.12, -15.7) * mm, "end": v(1.1, -15.53) * mm});
            skLineSegment(sketch, "E1396", {"start": v(1.1, -15.53) * mm, "end": v(1.08, -15.45) * mm});
            skLineSegment(sketch, "E1397", {"start": v(1.08, -15.45) * mm, "end": v(1.07, -15.4) * mm});
            skLineSegment(sketch, "E1398", {"start": v(1.07, -15.4) * mm, "end": v(1.06, -15.37) * mm});
            skLineSegment(sketch, "E1399", {"start": v(1.06, -15.37) * mm, "end": v(0.63, -15.3) * mm});
            skLineSegment(sketch, "E1400", {"start": v(0.63, -15.3) * mm, "end": v(0.61, -15.34) * mm});
            skLineSegment(sketch, "E1401", {"start": v(0.61, -15.34) * mm, "end": v(0.6, -15.38) * mm});
            skLineSegment(sketch, "E1402", {"start": v(0.6, -15.38) * mm, "end": v(0.56, -15.45) * mm});
            skLineSegment(sketch, "E1403", {"start": v(0.56, -15.45) * mm, "end": v(0.48, -15.6) * mm});
            skLineSegment(sketch, "E1404", {"start": v(0.48, -15.6) * mm, "end": v(0.4, -15.74) * mm});
            skLineSegment(sketch, "E1405", {"start": v(0.4, -15.74) * mm, "end": v(0.3, -15.88) * mm});
            skLineSegment(sketch, "E1406", {"start": v(0.3, -15.88) * mm, "end": v(-0.1, -15.8) * mm});
            skLineSegment(sketch, "E1407", {"start": v(-0.1, -15.8) * mm, "end": v(-0.14, -15.64) * mm});
            skLineSegment(sketch, "E1408", {"start": v(-0.14, -15.64) * mm, "end": v(-0.16, -15.47) * mm});
            skLineSegment(sketch, "E1409", {"start": v(-0.16, -15.47) * mm, "end": v(-0.18, -15.3) * mm});
            skLineSegment(sketch, "E1410", {"start": v(-0.18, -15.3) * mm, "end": v(-0.2, -15.23) * mm});
            skLineSegment(sketch, "E1411", {"start": v(-0.2, -15.23) * mm, "end": v(-0.2, -15.18) * mm});
            skLineSegment(sketch, "E1412", {"start": v(-0.2, -15.18) * mm, "end": v(-0.2, -15.14) * mm});
            skLineSegment(sketch, "E1413", {"start": v(-0.2, -15.14) * mm, "end": v(-0.62, -15.04) * mm});
            skLineSegment(sketch, "E1414", {"start": v(-0.62, -15.04) * mm, "end": v(-0.64, -15.08) * mm});
            skLineSegment(sketch, "E1415", {"start": v(-0.64, -15.08) * mm, "end": v(-0.67, -15.11) * mm});
            skLineSegment(sketch, "E1416", {"start": v(-0.67, -15.11) * mm, "end": v(-0.7, -15.18) * mm});
            skLineSegment(sketch, "E1417", {"start": v(-0.7, -15.18) * mm, "end": v(-0.8, -15.32) * mm});
            skLineSegment(sketch, "E1418", {"start": v(-0.8, -15.32) * mm, "end": v(-0.9, -15.46) * mm});
            skLineSegment(sketch, "E1419", {"start": v(-0.9, -15.46) * mm, "end": v(-1, -15.6) * mm});
            skLineSegment(sketch, "E1420", {"start": v(-1, -15.6) * mm, "end": v(-1.4, -15.48) * mm});
            skLineSegment(sketch, "E1421", {"start": v(-1.4, -15.48) * mm, "end": v(-1.42, -15.31) * mm});
            skLineSegment(sketch, "E1422", {"start": v(-1.42, -15.31) * mm, "end": v(-1.43, -15.15) * mm});
            skLineSegment(sketch, "E1423", {"start": v(-1.43, -15.15) * mm, "end": v(-1.44, -14.98) * mm});
            skLineSegment(sketch, "E1424", {"start": v(-1.44, -14.98) * mm, "end": v(-1.44, -14.9) * mm});
            skLineSegment(sketch, "E1425", {"start": v(-1.44, -14.9) * mm, "end": v(-1.44, -14.86) * mm});
            skLineSegment(sketch, "E1426", {"start": v(-1.44, -14.86) * mm, "end": v(-1.44, -14.82) * mm});
            skLineSegment(sketch, "E1427", {"start": v(-1.44, -14.82) * mm, "end": v(-1.85, -14.68) * mm});
            skLineSegment(sketch, "E1428", {"start": v(-1.85, -14.68) * mm, "end": v(-1.88, -14.71) * mm});
            skLineSegment(sketch, "E1429", {"start": v(-1.88, -14.71) * mm, "end": v(-1.9, -14.75) * mm});
            skLineSegment(sketch, "E1430", {"start": v(-1.9, -14.75) * mm, "end": v(-1.95, -14.81) * mm});
            skLineSegment(sketch, "E1431", {"start": v(-1.95, -14.81) * mm, "end": v(-2.05, -14.94) * mm});
            skLineSegment(sketch, "E1432", {"start": v(-2.05, -14.94) * mm, "end": v(-2.16, -15.07) * mm});
            skLineSegment(sketch, "E1433", {"start": v(-2.16, -15.07) * mm, "end": v(-2.27, -15.2) * mm});
            skLineSegment(sketch, "E1434", {"start": v(-2.27, -15.2) * mm, "end": v(-2.66, -15.05) * mm});
            skLineSegment(sketch, "E1435", {"start": v(-2.66, -15.05) * mm, "end": v(-2.67, -14.88) * mm});
            skLineSegment(sketch, "E1436", {"start": v(-2.67, -14.88) * mm, "end": v(-2.67, -14.72) * mm});
            skLineSegment(sketch, "E1437", {"start": v(-2.67, -14.72) * mm, "end": v(-2.66, -14.55) * mm});
            skLineSegment(sketch, "E1438", {"start": v(-2.66, -14.55) * mm, "end": v(-2.65, -14.47) * mm});
            skLineSegment(sketch, "E1439", {"start": v(-2.65, -14.47) * mm, "end": v(-2.65, -14.43) * mm});
            skLineSegment(sketch, "E1440", {"start": v(-2.65, -14.43) * mm, "end": v(-2.65, -14.39) * mm});
            skLineSegment(sketch, "E1441", {"start": v(-2.65, -14.39) * mm, "end": v(-3.05, -14.22) * mm});
            skLineSegment(sketch, "E1442", {"start": v(-3.05, -14.22) * mm, "end": v(-3.07, -14.25) * mm});
            skLineSegment(sketch, "E1443", {"start": v(-3.07, -14.25) * mm, "end": v(-3.1, -14.28) * mm});
            skLineSegment(sketch, "E1444", {"start": v(-3.1, -14.28) * mm, "end": v(-3.16, -14.34) * mm});
            skLineSegment(sketch, "E1445", {"start": v(-3.16, -14.34) * mm, "end": v(-3.27, -14.46) * mm});
            skLineSegment(sketch, "E1446", {"start": v(-3.27, -14.46) * mm, "end": v(-3.39, -14.58) * mm});
            skLineSegment(sketch, "E1447", {"start": v(-3.39, -14.58) * mm, "end": v(-3.5, -14.7) * mm});
            skLineSegment(sketch, "E1448", {"start": v(-3.5, -14.7) * mm, "end": v(-3.89, -14.52) * mm});
            skLineSegment(sketch, "E1449", {"start": v(-3.89, -14.52) * mm, "end": v(-3.88, -14.35) * mm});
            skLineSegment(sketch, "E1450", {"start": v(-3.88, -14.35) * mm, "end": v(-3.86, -14.19) * mm});
            skLineSegment(sketch, "E1451", {"start": v(-3.86, -14.19) * mm, "end": v(-3.84, -14.02) * mm});
            skLineSegment(sketch, "E1452", {"start": v(-3.84, -14.02) * mm, "end": v(-3.83, -13.94) * mm});
            skLineSegment(sketch, "E1453", {"start": v(-3.83, -13.94) * mm, "end": v(-3.82, -13.9) * mm});
            skLineSegment(sketch, "E1454", {"start": v(-3.82, -13.9) * mm, "end": v(-3.81, -13.86) * mm});
            skLineSegment(sketch, "E1455", {"start": v(-3.81, -13.86) * mm, "end": v(-4.2, -13.66) * mm});
            skLineSegment(sketch, "E1456", {"start": v(-4.2, -13.66) * mm, "end": v(-4.23, -13.69) * mm});
            skLineSegment(sketch, "E1457", {"start": v(-4.23, -13.69) * mm, "end": v(-4.26, -13.72) * mm});
            skLineSegment(sketch, "E1458", {"start": v(-4.26, -13.72) * mm, "end": v(-4.32, -13.77) * mm});
            skLineSegment(sketch, "E1459", {"start": v(-4.32, -13.77) * mm, "end": v(-4.44, -13.88) * mm});
            skLineSegment(sketch, "E1460", {"start": v(-4.44, -13.88) * mm, "end": v(-4.57, -14) * mm});
            skLineSegment(sketch, "E1461", {"start": v(-4.57, -14) * mm, "end": v(-4.7, -14.1) * mm});
            skLineSegment(sketch, "E1462", {"start": v(-4.7, -14.1) * mm, "end": v(-5.06, -13.9) * mm});
            skLineSegment(sketch, "E1463", {"start": v(-5.06, -13.9) * mm, "end": v(-5.04, -13.72) * mm});
            skLineSegment(sketch, "E1464", {"start": v(-5.04, -13.72) * mm, "end": v(-5, -13.56) * mm});
            skLineSegment(sketch, "E1465", {"start": v(-5, -13.56) * mm, "end": v(-4.97, -13.4) * mm});
            skLineSegment(sketch, "E1466", {"start": v(-4.97, -13.4) * mm, "end": v(-4.96, -13.32) * mm});
            skLineSegment(sketch, "E1467", {"start": v(-4.96, -13.32) * mm, "end": v(-4.95, -13.28) * mm});
            skLineSegment(sketch, "E1468", {"start": v(-4.95, -13.28) * mm, "end": v(-4.93, -13.24) * mm});
            skLineSegment(sketch, "E1469", {"start": v(-4.93, -13.24) * mm, "end": v(-5.3, -13) * mm});
            skLineSegment(sketch, "E1470", {"start": v(-5.3, -13) * mm, "end": v(-5.33, -13.03) * mm});
            skLineSegment(sketch, "E1471", {"start": v(-5.33, -13.03) * mm, "end": v(-5.37, -13.06) * mm});
            skLineSegment(sketch, "E1472", {"start": v(-5.37, -13.06) * mm, "end": v(-5.43, -13.1) * mm});
            skLineSegment(sketch, "E1473", {"start": v(-5.43, -13.1) * mm, "end": v(-5.56, -13.21) * mm});
            skLineSegment(sketch, "E1474", {"start": v(-5.56, -13.21) * mm, "end": v(-5.7, -13.3) * mm});
            skLineSegment(sketch, "E1475", {"start": v(-5.7, -13.3) * mm, "end": v(-5.84, -13.4) * mm});
            skLineSegment(sketch, "E1476", {"start": v(-5.84, -13.4) * mm, "end": v(-6.18, -13.17) * mm});
            skLineSegment(sketch, "E1477", {"start": v(-6.18, -13.17) * mm, "end": v(-6.14, -13) * mm});
            skLineSegment(sketch, "E1478", {"start": v(-6.14, -13) * mm, "end": v(-6.1, -12.84) * mm});
            skLineSegment(sketch, "E1479", {"start": v(-6.1, -12.84) * mm, "end": v(-6.05, -12.68) * mm});
            skLineSegment(sketch, "E1480", {"start": v(-6.05, -12.68) * mm, "end": v(-6.03, -12.6) * mm});
            skLineSegment(sketch, "E1481", {"start": v(-6.03, -12.6) * mm, "end": v(-6.01, -12.56) * mm});
            skLineSegment(sketch, "E1482", {"start": v(-6.01, -12.56) * mm, "end": v(-6, -12.52) * mm});
            skLineSegment(sketch, "E1483", {"start": v(-6, -12.52) * mm, "end": v(-6.35, -12.26) * mm});
            skLineSegment(sketch, "E1484", {"start": v(-6.35, -12.26) * mm, "end": v(-6.38, -12.29) * mm});
            skLineSegment(sketch, "E1485", {"start": v(-6.38, -12.29) * mm, "end": v(-6.42, -12.3) * mm});
            skLineSegment(sketch, "E1486", {"start": v(-6.42, -12.3) * mm, "end": v(-6.48, -12.36) * mm});
            skLineSegment(sketch, "E1487", {"start": v(-6.48, -12.36) * mm, "end": v(-6.62, -12.45) * mm});
            skLineSegment(sketch, "E1488", {"start": v(-6.62, -12.45) * mm, "end": v(-6.77, -12.53) * mm});
            skLineSegment(sketch, "E1489", {"start": v(-6.77, -12.53) * mm, "end": v(-6.91, -12.62) * mm});
            skLineSegment(sketch, "E1490", {"start": v(-6.91, -12.62) * mm, "end": v(-7.24, -12.35) * mm});
            skLineSegment(sketch, "E1491", {"start": v(-7.24, -12.35) * mm, "end": v(-7.19, -12.19) * mm});
            skLineSegment(sketch, "E1492", {"start": v(-7.19, -12.19) * mm, "end": v(-7.13, -12.03) * mm});
            skLineSegment(sketch, "E1493", {"start": v(-7.13, -12.03) * mm, "end": v(-7.07, -11.88) * mm});
            skLineSegment(sketch, "E1494", {"start": v(-7.07, -11.88) * mm, "end": v(-7.04, -11.8) * mm});
            skLineSegment(sketch, "E1495", {"start": v(-7.04, -11.8) * mm, "end": v(-7.02, -11.76) * mm});
            skLineSegment(sketch, "E1496", {"start": v(-7.02, -11.76) * mm, "end": v(-7, -11.73) * mm});
            skLineSegment(sketch, "E1497", {"start": v(-7, -11.73) * mm, "end": v(-7.33, -11.44) * mm});
            skLineSegment(sketch, "E1498", {"start": v(-7.33, -11.44) * mm, "end": v(-7.36, -11.46) * mm});
            skLineSegment(sketch, "E1499", {"start": v(-7.36, -11.46) * mm, "end": v(-7.4, -11.48) * mm});
            skLineSegment(sketch, "E1500", {"start": v(-7.4, -11.48) * mm, "end": v(-7.47, -11.52) * mm});
            skLineSegment(sketch, "E1501", {"start": v(-7.47, -11.52) * mm, "end": v(-7.62, -11.6) * mm});
            skLineSegment(sketch, "E1502", {"start": v(-7.62, -11.6) * mm, "end": v(-7.77, -11.67) * mm});
            skLineSegment(sketch, "E1503", {"start": v(-7.77, -11.67) * mm, "end": v(-7.92, -11.74) * mm});
            skLineSegment(sketch, "E1504", {"start": v(-7.92, -11.74) * mm, "end": v(-8.22, -11.45) * mm});
            skLineSegment(sketch, "E1505", {"start": v(-8.22, -11.45) * mm, "end": v(-8.16, -11.3) * mm});
            skLineSegment(sketch, "E1506", {"start": v(-8.16, -11.3) * mm, "end": v(-8.09, -11.14) * mm});
            skLineSegment(sketch, "E1507", {"start": v(-8.09, -11.14) * mm, "end": v(-8.01, -11) * mm});
            skLineSegment(sketch, "E1508", {"start": v(-8.01, -11) * mm, "end": v(-7.98, -10.92) * mm});
            skLineSegment(sketch, "E1509", {"start": v(-7.98, -10.92) * mm, "end": v(-7.96, -10.88) * mm});
            skLineSegment(sketch, "E1510", {"start": v(-7.96, -10.88) * mm, "end": v(-7.94, -10.85) * mm});
            skLineSegment(sketch, "E1511", {"start": v(-7.94, -10.85) * mm, "end": v(-8.24, -10.53) * mm});
            skLineSegment(sketch, "E1512", {"start": v(-8.24, -10.53) * mm, "end": v(-8.27, -10.55) * mm});
            skLineSegment(sketch, "E1513", {"start": v(-8.27, -10.55) * mm, "end": v(-8.31, -10.57) * mm});
            skLineSegment(sketch, "E1514", {"start": v(-8.31, -10.57) * mm, "end": v(-8.39, -10.6) * mm});
            skLineSegment(sketch, "E1515", {"start": v(-8.39, -10.6) * mm, "end": v(-8.54, -10.67) * mm});
            skLineSegment(sketch, "E1516", {"start": v(-8.54, -10.67) * mm, "end": v(-8.7, -10.73) * mm});
            skLineSegment(sketch, "E1517", {"start": v(-8.7, -10.73) * mm, "end": v(-8.85, -10.79) * mm});
            skLineSegment(sketch, "E1518", {"start": v(-8.85, -10.79) * mm, "end": v(-9.13, -10.47) * mm});
            skLineSegment(sketch, "E1519", {"start": v(-9.13, -10.47) * mm, "end": v(-9.05, -10.32) * mm});
            skLineSegment(sketch, "E1520", {"start": v(-9.05, -10.32) * mm, "end": v(-8.97, -10.18) * mm});
            skLineSegment(sketch, "E1521", {"start": v(-8.97, -10.18) * mm, "end": v(-8.88, -10.03) * mm});
            skLineSegment(sketch, "E1522", {"start": v(-8.88, -10.03) * mm, "end": v(-8.84, -9.96) * mm});
            skLineSegment(sketch, "E1523", {"start": v(-8.84, -9.96) * mm, "end": v(-8.82, -9.93) * mm});
            skLineSegment(sketch, "E1524", {"start": v(-8.82, -9.93) * mm, "end": v(-8.8, -9.9) * mm});
            skLineSegment(sketch, "E1525", {"start": v(-8.8, -9.9) * mm, "end": v(-9.07, -9.56) * mm});
            skLineSegment(sketch, "E1526", {"start": v(-9.07, -9.56) * mm, "end": v(-9.1, -9.57) * mm});
            skLineSegment(sketch, "E1527", {"start": v(-9.1, -9.57) * mm, "end": v(-9.14, -9.59) * mm});
            skLineSegment(sketch, "E1528", {"start": v(-9.14, -9.59) * mm, "end": v(-9.22, -9.61) * mm});
            skLineSegment(sketch, "E1529", {"start": v(-9.22, -9.61) * mm, "end": v(-9.38, -9.67) * mm});
            skLineSegment(sketch, "E1530", {"start": v(-9.38, -9.67) * mm, "end": v(-9.54, -9.72) * mm});
            skLineSegment(sketch, "E1531", {"start": v(-9.54, -9.72) * mm, "end": v(-9.7, -9.76) * mm});
            skLineSegment(sketch, "E1532", {"start": v(-9.7, -9.76) * mm, "end": v(-9.95, -9.42) * mm});
            skLineSegment(sketch, "E1533", {"start": v(-9.95, -9.42) * mm, "end": v(-9.86, -9.28) * mm});
            skLineSegment(sketch, "E1534", {"start": v(-9.86, -9.28) * mm, "end": v(-9.77, -9.14) * mm});
            skLineSegment(sketch, "E1535", {"start": v(-9.77, -9.14) * mm, "end": v(-9.67, -9) * mm});
            skLineSegment(sketch, "E1536", {"start": v(-9.67, -9) * mm, "end": v(-9.62, -8.94) * mm});
            skLineSegment(sketch, "E1537", {"start": v(-9.62, -8.94) * mm, "end": v(-9.6, -8.9) * mm});
            skLineSegment(sketch, "E1538", {"start": v(-9.6, -8.9) * mm, "end": v(-9.57, -8.88) * mm});
            skLineSegment(sketch, "E1539", {"start": v(-9.57, -8.88) * mm, "end": v(-9.82, -8.51) * mm});
            skLineSegment(sketch, "E1540", {"start": v(-9.82, -8.51) * mm, "end": v(-9.85, -8.53) * mm});
            skLineSegment(sketch, "E1541", {"start": v(-9.85, -8.53) * mm, "end": v(-9.9, -8.54) * mm});
            skLineSegment(sketch, "E1542", {"start": v(-9.9, -8.54) * mm, "end": v(-9.97, -8.56) * mm});
            skLineSegment(sketch, "E1543", {"start": v(-9.97, -8.56) * mm, "end": v(-10.13, -8.6) * mm});
            skLineSegment(sketch, "E1544", {"start": v(-10.13, -8.6) * mm, "end": v(-10.3, -8.63) * mm});
            skLineSegment(sketch, "E1545", {"start": v(-10.3, -8.63) * mm, "end": v(-10.47, -8.66) * mm});
            skLineSegment(sketch, "E1546", {"start": v(-10.47, -8.66) * mm, "end": v(-10.69, -8.3) * mm});
            skLineSegment(sketch, "E1547", {"start": v(-10.69, -8.3) * mm, "end": v(-10.58, -8.17) * mm});
            skLineSegment(sketch, "E1548", {"start": v(-10.58, -8.17) * mm, "end": v(-10.48, -8.04) * mm});
            skLineSegment(sketch, "E1549", {"start": v(-10.48, -8.04) * mm, "end": v(-10.37, -7.92) * mm});
            skLineSegment(sketch, "E1550", {"start": v(-10.37, -7.92) * mm, "end": v(-10.32, -7.85) * mm});
            skLineSegment(sketch, "E1551", {"start": v(-10.32, -7.85) * mm, "end": v(-10.29, -7.82) * mm});
            skLineSegment(sketch, "E1552", {"start": v(-10.29, -7.82) * mm, "end": v(-10.26, -7.8) * mm});
            skLineSegment(sketch, "E1553", {"start": v(-10.26, -7.8) * mm, "end": v(-10.47, -7.42) * mm});
            skLineSegment(sketch, "E1554", {"start": v(-10.47, -7.42) * mm, "end": v(-10.51, -7.42) * mm});
            skLineSegment(sketch, "E1555", {"start": v(-10.51, -7.42) * mm, "end": v(-10.55, -7.43) * mm});
            skLineSegment(sketch, "E1556", {"start": v(-10.55, -7.43) * mm, "end": v(-10.64, -7.45) * mm});
            skLineSegment(sketch, "E1557", {"start": v(-10.64, -7.45) * mm, "end": v(-10.8, -7.47) * mm});
            skLineSegment(sketch, "E1558", {"start": v(-10.8, -7.47) * mm, "end": v(-10.97, -7.5) * mm});
            skLineSegment(sketch, "E1559", {"start": v(-10.97, -7.5) * mm, "end": v(-11.13, -7.51) * mm});
            skLineSegment(sketch, "E1560", {"start": v(-11.13, -7.51) * mm, "end": v(-11.32, -7.14) * mm});
            skLineSegment(sketch, "E1561", {"start": v(-11.32, -7.14) * mm, "end": v(-11.21, -7.01) * mm});
            skLineSegment(sketch, "E1562", {"start": v(-11.21, -7.01) * mm, "end": v(-11.1, -6.9) * mm});
            skLineSegment(sketch, "E1563", {"start": v(-11.1, -6.9) * mm, "end": v(-10.98, -6.77) * mm});
            skLineSegment(sketch, "E1564", {"start": v(-10.98, -6.77) * mm, "end": v(-10.92, -6.72) * mm});
            skLineSegment(sketch, "E1565", {"start": v(-10.92, -6.72) * mm, "end": v(-10.89, -6.69) * mm});
            skLineSegment(sketch, "E1566", {"start": v(-10.89, -6.69) * mm, "end": v(-10.86, -6.66) * mm});
            skLineSegment(sketch, "E1567", {"start": v(-10.86, -6.66) * mm, "end": v(-11.04, -6.27) * mm});
            skLineSegment(sketch, "E1568", {"start": v(-11.04, -6.27) * mm, "end": v(-11.08, -6.27) * mm});
            skLineSegment(sketch, "E1569", {"start": v(-11.08, -6.27) * mm, "end": v(-11.12, -6.27) * mm});
            skLineSegment(sketch, "E1570", {"start": v(-11.12, -6.27) * mm, "end": v(-11.2, -6.28) * mm});
            skLineSegment(sketch, "E1571", {"start": v(-11.2, -6.28) * mm, "end": v(-11.37, -6.3) * mm});
            skLineSegment(sketch, "E1572", {"start": v(-11.37, -6.3) * mm, "end": v(-11.54, -6.3) * mm});
            skLineSegment(sketch, "E1573", {"start": v(-11.54, -6.3) * mm, "end": v(-11.7, -6.3) * mm});
            skLineSegment(sketch, "E1574", {"start": v(-11.7, -6.3) * mm, "end": v(-11.86, -5.92) * mm});
            skLineSegment(sketch, "E1575", {"start": v(-11.86, -5.92) * mm, "end": v(-11.74, -5.8) * mm});
            skLineSegment(sketch, "E1576", {"start": v(-11.74, -5.8) * mm, "end": v(-11.62, -5.7) * mm});
            skLineSegment(sketch, "E1577", {"start": v(-11.62, -5.7) * mm, "end": v(-11.5, -5.58) * mm});
            skLineSegment(sketch, "E1578", {"start": v(-11.5, -5.58) * mm, "end": v(-11.43, -5.53) * mm});
            skLineSegment(sketch, "E1579", {"start": v(-11.43, -5.53) * mm, "end": v(-11.4, -5.5) * mm});
            skLineSegment(sketch, "E1580", {"start": v(-11.4, -5.5) * mm, "end": v(-11.36, -5.48) * mm});
            skLineSegment(sketch, "E1581", {"start": v(-11.36, -5.48) * mm, "end": v(-11.5, -5.07) * mm});
            skLineSegment(sketch, "E1582", {"start": v(-11.5, -5.07) * mm, "end": v(-11.55, -5.07) * mm});
            skLineSegment(sketch, "E1583", {"start": v(-11.55, -5.07) * mm, "end": v(-11.6, -5.08) * mm});
            skLineSegment(sketch, "E1584", {"start": v(-11.6, -5.08) * mm, "end": v(-11.67, -5.08) * mm});
            skLineSegment(sketch, "E1585", {"start": v(-11.67, -5.08) * mm, "end": v(-11.84, -5.08) * mm});
            skLineSegment(sketch, "E1586", {"start": v(-11.84, -5.08) * mm, "end": v(-12, -5.07) * mm});
            skLineSegment(sketch, "E1587", {"start": v(-12, -5.07) * mm, "end": v(-12.18, -5.06) * mm});
            skLineSegment(sketch, "E1588", {"start": v(-12.18, -5.06) * mm, "end": v(-12.3, -4.66) * mm});
            skLineSegment(sketch, "E1589", {"start": v(-12.3, -4.66) * mm, "end": v(-12.17, -4.55) * mm});
            skLineSegment(sketch, "E1590", {"start": v(-12.17, -4.55) * mm, "end": v(-12.04, -4.45) * mm});
            skLineSegment(sketch, "E1591", {"start": v(-12.04, -4.45) * mm, "end": v(-11.9, -4.36) * mm});
            skLineSegment(sketch, "E1592", {"start": v(-11.9, -4.36) * mm, "end": v(-11.83, -4.3) * mm});
            skLineSegment(sketch, "E1593", {"start": v(-11.83, -4.3) * mm, "end": v(-11.8, -4.29) * mm});
            skLineSegment(sketch, "E1594", {"start": v(-11.8, -4.29) * mm, "end": v(-11.76, -4.26) * mm});
            skLineSegment(sketch, "E1595", {"start": v(-11.76, -4.26) * mm, "end": v(-11.88, -3.84) * mm});
            skLineSegment(sketch, "E1596", {"start": v(-11.88, -3.84) * mm, "end": v(-11.92, -3.84) * mm});
            skLineSegment(sketch, "E1597", {"start": v(-11.92, -3.84) * mm, "end": v(-11.96, -3.84) * mm});
            skLineSegment(sketch, "E1598", {"start": v(-11.96, -3.84) * mm, "end": v(-12.04, -3.84) * mm});
            skLineSegment(sketch, "E1599", {"start": v(-12.04, -3.84) * mm, "end": v(-12.2, -3.82) * mm});
            skLineSegment(sketch, "E1600", {"start": v(-12.2, -3.82) * mm, "end": v(-12.37, -3.8) * mm});
            skLineSegment(sketch, "E1601", {"start": v(-12.37, -3.8) * mm, "end": v(-12.54, -3.78) * mm});
            skLineSegment(sketch, "E1602", {"start": v(-12.54, -3.78) * mm, "end": v(-12.63, -3.37) * mm});
            skLineSegment(sketch, "E1603", {"start": v(-12.63, -3.37) * mm, "end": v(-12.5, -3.27) * mm});
            skLineSegment(sketch, "E1604", {"start": v(-12.5, -3.27) * mm, "end": v(-12.35, -3.18) * mm});
            skLineSegment(sketch, "E1605", {"start": v(-12.35, -3.18) * mm, "end": v(-12.2, -3.1) * mm});
            skLineSegment(sketch, "E1606", {"start": v(-12.2, -3.1) * mm, "end": v(-12.14, -3.06) * mm});
            skLineSegment(sketch, "E1607", {"start": v(-12.14, -3.06) * mm, "end": v(-12.1, -3.04) * mm});
            skLineSegment(sketch, "E1608", {"start": v(-12.1, -3.04) * mm, "end": v(-12.07, -3.02) * mm});
            skLineSegment(sketch, "E1609", {"start": v(-12.07, -3.02) * mm, "end": v(-12.14, -2.6) * mm});
            skLineSegment(sketch, "E1610", {"start": v(-12.14, -2.6) * mm, "end": v(-12.18, -2.59) * mm});
            skLineSegment(sketch, "E1611", {"start": v(-12.18, -2.59) * mm, "end": v(-12.23, -2.58) * mm});
            skLineSegment(sketch, "E1612", {"start": v(-12.23, -2.58) * mm, "end": v(-12.3, -2.57) * mm});
            skLineSegment(sketch, "E1613", {"start": v(-12.3, -2.57) * mm, "end": v(-12.47, -2.54) * mm});
            skLineSegment(sketch, "E1614", {"start": v(-12.47, -2.54) * mm, "end": v(-12.63, -2.5) * mm});
            skLineSegment(sketch, "E1615", {"start": v(-12.63, -2.5) * mm, "end": v(-12.8, -2.47) * mm});
            skLineSegment(sketch, "E1616", {"start": v(-12.8, -2.47) * mm, "end": v(-12.86, -2.05) * mm});
            skLineSegment(sketch, "E1617", {"start": v(-12.86, -2.05) * mm, "end": v(-12.71, -1.97) * mm});
            skLineSegment(sketch, "E1618", {"start": v(-12.71, -1.97) * mm, "end": v(-12.56, -1.9) * mm});
            skLineSegment(sketch, "E1619", {"start": v(-12.56, -1.9) * mm, "end": v(-12.41, -1.82) * mm});
            skLineSegment(sketch, "E1620", {"start": v(-12.41, -1.82) * mm, "end": v(-12.34, -1.79) * mm});
            skLineSegment(sketch, "E1621", {"start": v(-12.34, -1.79) * mm, "end": v(-12.3, -1.77) * mm});
            skLineSegment(sketch, "E1622", {"start": v(-12.3, -1.77) * mm, "end": v(-12.26, -1.75) * mm});
            skLineSegment(sketch, "E1623", {"start": v(-12.26, -1.75) * mm, "end": v(-12.3, -1.32) * mm});
            skLineSegment(sketch, "E1624", {"start": v(-12.3, -1.32) * mm, "end": v(-12.35, -1.31) * mm});
            skLineSegment(sketch, "E1625", {"start": v(-12.35, -1.31) * mm, "end": v(-12.39, -1.3) * mm});
            skLineSegment(sketch, "E1626", {"start": v(-12.39, -1.3) * mm, "end": v(-12.47, -1.28) * mm});
            skLineSegment(sketch, "E1627", {"start": v(-12.47, -1.28) * mm, "end": v(-12.63, -1.24) * mm});
            skLineSegment(sketch, "E1628", {"start": v(-12.63, -1.24) * mm, "end": v(-12.79, -1.2) * mm});
            skLineSegment(sketch, "E1629", {"start": v(-12.79, -1.2) * mm, "end": v(-12.95, -1.14) * mm});
            skLineSegment(sketch, "E1630", {"start": v(-12.95, -1.14) * mm, "end": v(-12.97, -0.72) * mm});
            skLineSegment(sketch, "E1631", {"start": v(-12.97, -0.72) * mm, "end": v(-12.82, -0.65) * mm});
            skLineSegment(sketch, "E1632", {"start": v(-12.82, -0.65) * mm, "end": v(-12.66, -0.59) * mm});
            skLineSegment(sketch, "E1633", {"start": v(-12.66, -0.59) * mm, "end": v(-12.5, -0.53) * mm});
            skLineSegment(sketch, "E1634", {"start": v(-12.5, -0.53) * mm, "end": v(-12.43, -0.5) * mm});
            skLineSegment(sketch, "E1635", {"start": v(-12.43, -0.5) * mm, "end": v(-12.4, -0.49) * mm});
            skLineSegment(sketch, "E1636", {"start": v(-12.4, -0.49) * mm, "end": v(-12.35, -0.47) * mm});
            skLineSegment(sketch, "E1637", {"start": v(-12.35, -0.47) * mm, "end": v(-12.36, -0.04) * mm});
            skLineSegment(sketch, "E1638", {"start": v(-2.23, 0) * mm, "end": v(8.53, 0) * mm, "construction": true});
            skLineSegment(sketch, "E1639", {"start": v(3.15, -5.38) * mm, "end": v(3.15, 5.38) * mm, "construction": true});
            skCircle(sketch, "E1640", {"center": v(3.15, 0) * mm, "radius": 5.05 * mm});
            skSolve(sketch);
        }
        {
            var Q0;
            Q0=makeQuery(id+"F0.imprint","IMPRINT",FACE,{"disambiguationData":[TD([[makeQuery(id+"F0.imprint","IMPRINT",EDGE,{"derivedFrom":sQuery(id+"F0.wireOp",EDGE,"E574")}),-1.0]])]});
            var Q1;
            Q1=makeQuery(id+"F0.imprint","IMPRINT",FACE,{"disambiguationData":[TD([[makeQuery(id+"F0.imprint","IMPRINT",EDGE,{"derivedFrom":sQuery(id+"F0.wireOp",EDGE,"E0")}),-1.0]])]});
            extrude(context, id + "F1", {"entities" : qUnion([Q0, Q1]), "oppositeDirection" : true, "depth" : 4.5 * mm, "offsetDistance" : 25 * mm});
        }
        {
            var Q0;
            Q0=makeQuery(id+"F1.opExtrude","CAP_FACE",FACE,{"disambiguationData":[OSD([sQuery(id+"F0.wireOp",EDGE,"E574"),sQuery(id+"F0.wireOp",EDGE,"E575"),sQuery(id+"F0.wireOp",EDGE,"E576"),sQuery(id+"F0.wireOp",EDGE,"E577"),sQuery(id+"F0.wireOp",EDGE,"E578"),sQuery(id+"F0.wireOp",EDGE,"E579"),sQuery(id+"F0.wireOp",EDGE,"E580"),sQuery(id+"F0.wireOp",EDGE,"E581"),sQuery(id+"F0.wireOp",EDGE,"E582"),sQuery(id+"F0.wireOp",EDGE,"E583"),sQuery(id+"F0.wireOp",EDGE,"E584"),sQuery(id+"F0.wireOp",EDGE,"E585"),sQuery(id+"F0.wireOp",EDGE,"E586"),sQuery(id+"F0.wireOp",EDGE,"E587"),sQuery(id+"F0.wireOp",EDGE,"E588"),sQuery(id+"F0.wireOp",EDGE,"E589"),sQuery(id+"F0.wireOp",EDGE,"E590"),sQuery(id+"F0.wireOp",EDGE,"E591"),sQuery(id+"F0.wireOp",EDGE,"E592"),sQuery(id+"F0.wireOp",EDGE,"E593"),sQuery(id+"F0.wireOp",EDGE,"E594"),sQuery(id+"F0.wireOp",EDGE,"E595"),sQuery(id+"F0.wireOp",EDGE,"E596"),sQuery(id+"F0.wireOp",EDGE,"E597"),sQuery(id+"F0.wireOp",EDGE,"E598"),sQuery(id+"F0.wireOp",EDGE,"E599"),sQuery(id+"F0.wireOp",EDGE,"E600"),sQuery(id+"F0.wireOp",EDGE,"E601"),sQuery(id+"F0.wireOp",EDGE,"E602"),sQuery(id+"F0.wireOp",EDGE,"E603"),sQuery(id+"F0.wireOp",EDGE,"E604"),sQuery(id+"F0.wireOp",EDGE,"E605"),sQuery(id+"F0.wireOp",EDGE,"E606"),sQuery(id+"F0.wireOp",EDGE,"E607"),sQuery(id+"F0.wireOp",EDGE,"E608"),sQuery(id+"F0.wireOp",EDGE,"E609"),sQuery(id+"F0.wireOp",EDGE,"E610"),sQuery(id+"F0.wireOp",EDGE,"E611"),sQuery(id+"F0.wireOp",EDGE,"E612"),sQuery(id+"F0.wireOp",EDGE,"E613"),sQuery(id+"F0.wireOp",EDGE,"E614"),sQuery(id+"F0.wireOp",EDGE,"E615"),sQuery(id+"F0.wireOp",EDGE,"E616"),sQuery(id+"F0.wireOp",EDGE,"E617"),sQuery(id+"F0.wireOp",EDGE,"E618"),sQuery(id+"F0.wireOp",EDGE,"E619"),sQuery(id+"F0.wireOp",EDGE,"E620"),sQuery(id+"F0.wireOp",EDGE,"E621"),sQuery(id+"F0.wireOp",EDGE,"E622"),sQuery(id+"F0.wireOp",EDGE,"E623"),sQuery(id+"F0.wireOp",EDGE,"E624"),sQuery(id+"F0.wireOp",EDGE,"E625"),sQuery(id+"F0.wireOp",EDGE,"E626"),sQuery(id+"F0.wireOp",EDGE,"E627"),sQuery(id+"F0.wireOp",EDGE,"E628"),sQuery(id+"F0.wireOp",EDGE,"E629"),sQuery(id+"F0.wireOp",EDGE,"E630"),sQuery(id+"F0.wireOp",EDGE,"E631"),sQuery(id+"F0.wireOp",EDGE,"E632"),sQuery(id+"F0.wireOp",EDGE,"E633"),sQuery(id+"F0.wireOp",EDGE,"E634"),sQuery(id+"F0.wireOp",EDGE,"E635"),sQuery(id+"F0.wireOp",EDGE,"E636"),sQuery(id+"F0.wireOp",EDGE,"E637"),sQuery(id+"F0.wireOp",EDGE,"E638"),sQuery(id+"F0.wireOp",EDGE,"E639"),sQuery(id+"F0.wireOp",EDGE,"E640"),sQuery(id+"F0.wireOp",EDGE,"E641"),sQuery(id+"F0.wireOp",EDGE,"E642"),sQuery(id+"F0.wireOp",EDGE,"E643"),sQuery(id+"F0.wireOp",EDGE,"E644"),sQuery(id+"F0.wireOp",EDGE,"E645"),sQuery(id+"F0.wireOp",EDGE,"E646"),sQuery(id+"F0.wireOp",EDGE,"E647"),sQuery(id+"F0.wireOp",EDGE,"E648"),sQuery(id+"F0.wireOp",EDGE,"E649"),sQuery(id+"F0.wireOp",EDGE,"E650"),sQuery(id+"F0.wireOp",EDGE,"E651"),sQuery(id+"F0.wireOp",EDGE,"E652"),sQuery(id+"F0.wireOp",EDGE,"E653"),sQuery(id+"F0.wireOp",EDGE,"E654"),sQuery(id+"F0.wireOp",EDGE,"E655"),sQuery(id+"F0.wireOp",EDGE,"E656"),sQuery(id+"F0.wireOp",EDGE,"E657"),sQuery(id+"F0.wireOp",EDGE,"E658"),sQuery(id+"F0.wireOp",EDGE,"E659"),sQuery(id+"F0.wireOp",EDGE,"E660"),sQuery(id+"F0.wireOp",EDGE,"E661"),sQuery(id+"F0.wireOp",EDGE,"E662"),sQuery(id+"F0.wireOp",EDGE,"E663"),sQuery(id+"F0.wireOp",EDGE,"E664"),sQuery(id+"F0.wireOp",EDGE,"E665"),sQuery(id+"F0.wireOp",EDGE,"E666"),sQuery(id+"F0.wireOp",EDGE,"E667"),sQuery(id+"F0.wireOp",EDGE,"E668"),sQuery(id+"F0.wireOp",EDGE,"E669"),sQuery(id+"F0.wireOp",EDGE,"E670"),sQuery(id+"F0.wireOp",EDGE,"E671"),sQuery(id+"F0.wireOp",EDGE,"E672"),sQuery(id+"F0.wireOp",EDGE,"E673"),sQuery(id+"F0.wireOp",EDGE,"E674"),sQuery(id+"F0.wireOp",EDGE,"E675"),sQuery(id+"F0.wireOp",EDGE,"E676"),sQuery(id+"F0.wireOp",EDGE,"E677"),sQuery(id+"F0.wireOp",EDGE,"E678"),sQuery(id+"F0.wireOp",EDGE,"E679"),sQuery(id+"F0.wireOp",EDGE,"E680"),sQuery(id+"F0.wireOp",EDGE,"E681"),sQuery(id+"F0.wireOp",EDGE,"E682"),sQuery(id+"F0.wireOp",EDGE,"E683"),sQuery(id+"F0.wireOp",EDGE,"E684"),sQuery(id+"F0.wireOp",EDGE,"E685"),sQuery(id+"F0.wireOp",EDGE,"E686"),sQuery(id+"F0.wireOp",EDGE,"E687"),sQuery(id+"F0.wireOp",EDGE,"E688"),sQuery(id+"F0.wireOp",EDGE,"E689"),sQuery(id+"F0.wireOp",EDGE,"E690"),sQuery(id+"F0.wireOp",EDGE,"E691"),sQuery(id+"F0.wireOp",EDGE,"E692"),sQuery(id+"F0.wireOp",EDGE,"E693"),sQuery(id+"F0.wireOp",EDGE,"E694"),sQuery(id+"F0.wireOp",EDGE,"E695"),sQuery(id+"F0.wireOp",EDGE,"E696"),sQuery(id+"F0.wireOp",EDGE,"E697"),sQuery(id+"F0.wireOp",EDGE,"E698"),sQuery(id+"F0.wireOp",EDGE,"E699"),sQuery(id+"F0.wireOp",EDGE,"E700"),sQuery(id+"F0.wireOp",EDGE,"E701"),sQuery(id+"F0.wireOp",EDGE,"E702"),sQuery(id+"F0.wireOp",EDGE,"E703"),sQuery(id+"F0.wireOp",EDGE,"E704"),sQuery(id+"F0.wireOp",EDGE,"E705"),sQuery(id+"F0.wireOp",EDGE,"E706"),sQuery(id+"F0.wireOp",EDGE,"E707"),sQuery(id+"F0.wireOp",EDGE,"E708"),sQuery(id+"F0.wireOp",EDGE,"E709"),sQuery(id+"F0.wireOp",EDGE,"E710"),sQuery(id+"F0.wireOp",EDGE,"E711"),sQuery(id+"F0.wireOp",EDGE,"E712"),sQuery(id+"F0.wireOp",EDGE,"E713"),sQuery(id+"F0.wireOp",EDGE,"E714"),sQuery(id+"F0.wireOp",EDGE,"E715"),sQuery(id+"F0.wireOp",EDGE,"E716"),sQuery(id+"F0.wireOp",EDGE,"E717"),sQuery(id+"F0.wireOp",EDGE,"E718"),sQuery(id+"F0.wireOp",EDGE,"E719"),sQuery(id+"F0.wireOp",EDGE,"E720"),sQuery(id+"F0.wireOp",EDGE,"E721"),sQuery(id+"F0.wireOp",EDGE,"E722"),sQuery(id+"F0.wireOp",EDGE,"E723"),sQuery(id+"F0.wireOp",EDGE,"E724"),sQuery(id+"F0.wireOp",EDGE,"E725"),sQuery(id+"F0.wireOp",EDGE,"E726"),sQuery(id+"F0.wireOp",EDGE,"E727"),sQuery(id+"F0.wireOp",EDGE,"E728"),sQuery(id+"F0.wireOp",EDGE,"E729"),sQuery(id+"F0.wireOp",EDGE,"E730"),sQuery(id+"F0.wireOp",EDGE,"E731"),sQuery(id+"F0.wireOp",EDGE,"E732"),sQuery(id+"F0.wireOp",EDGE,"E733"),sQuery(id+"F0.wireOp",EDGE,"E734"),sQuery(id+"F0.wireOp",EDGE,"E735"),sQuery(id+"F0.wireOp",EDGE,"E736"),sQuery(id+"F0.wireOp",EDGE,"E737"),sQuery(id+"F0.wireOp",EDGE,"E738"),sQuery(id+"F0.wireOp",EDGE,"E739"),sQuery(id+"F0.wireOp",EDGE,"E740"),sQuery(id+"F0.wireOp",EDGE,"E741"),sQuery(id+"F0.wireOp",EDGE,"E742"),sQuery(id+"F0.wireOp",EDGE,"E743"),sQuery(id+"F0.wireOp",EDGE,"E744"),sQuery(id+"F0.wireOp",EDGE,"E745"),sQuery(id+"F0.wireOp",EDGE,"E746"),sQuery(id+"F0.wireOp",EDGE,"E747"),sQuery(id+"F0.wireOp",EDGE,"E748"),sQuery(id+"F0.wireOp",EDGE,"E749"),sQuery(id+"F0.wireOp",EDGE,"E750"),sQuery(id+"F0.wireOp",EDGE,"E751"),sQuery(id+"F0.wireOp",EDGE,"E752"),sQuery(id+"F0.wireOp",EDGE,"E753"),sQuery(id+"F0.wireOp",EDGE,"E754"),sQuery(id+"F0.wireOp",EDGE,"E755"),sQuery(id+"F0.wireOp",EDGE,"E756"),sQuery(id+"F0.wireOp",EDGE,"E757"),sQuery(id+"F0.wireOp",EDGE,"E758"),sQuery(id+"F0.wireOp",EDGE,"E759"),sQuery(id+"F0.wireOp",EDGE,"E760"),sQuery(id+"F0.wireOp",EDGE,"E761"),sQuery(id+"F0.wireOp",EDGE,"E762"),sQuery(id+"F0.wireOp",EDGE,"E763"),sQuery(id+"F0.wireOp",EDGE,"E764"),sQuery(id+"F0.wireOp",EDGE,"E765"),sQuery(id+"F0.wireOp",EDGE,"E766"),sQuery(id+"F0.wireOp",EDGE,"E767"),sQuery(id+"F0.wireOp",EDGE,"E768"),sQuery(id+"F0.wireOp",EDGE,"E769"),sQuery(id+"F0.wireOp",EDGE,"E770"),sQuery(id+"F0.wireOp",EDGE,"E771"),sQuery(id+"F0.wireOp",EDGE,"E772"),sQuery(id+"F0.wireOp",EDGE,"E773"),sQuery(id+"F0.wireOp",EDGE,"E774"),sQuery(id+"F0.wireOp",EDGE,"E775"),sQuery(id+"F0.wireOp",EDGE,"E776"),sQuery(id+"F0.wireOp",EDGE,"E777"),sQuery(id+"F0.wireOp",EDGE,"E778"),sQuery(id+"F0.wireOp",EDGE,"E779"),sQuery(id+"F0.wireOp",EDGE,"E780"),sQuery(id+"F0.wireOp",EDGE,"E781"),sQuery(id+"F0.wireOp",EDGE,"E782"),sQuery(id+"F0.wireOp",EDGE,"E783"),sQuery(id+"F0.wireOp",EDGE,"E784"),sQuery(id+"F0.wireOp",EDGE,"E785"),sQuery(id+"F0.wireOp",EDGE,"E786"),sQuery(id+"F0.wireOp",EDGE,"E787"),sQuery(id+"F0.wireOp",EDGE,"E788"),sQuery(id+"F0.wireOp",EDGE,"E789"),sQuery(id+"F0.wireOp",EDGE,"E790"),sQuery(id+"F0.wireOp",EDGE,"E791"),sQuery(id+"F0.wireOp",EDGE,"E792"),sQuery(id+"F0.wireOp",EDGE,"E793"),sQuery(id+"F0.wireOp",EDGE,"E794"),sQuery(id+"F0.wireOp",EDGE,"E795"),sQuery(id+"F0.wireOp",EDGE,"E796"),sQuery(id+"F0.wireOp",EDGE,"E797"),sQuery(id+"F0.wireOp",EDGE,"E798"),sQuery(id+"F0.wireOp",EDGE,"E799"),sQuery(id+"F0.wireOp",EDGE,"E800"),sQuery(id+"F0.wireOp",EDGE,"E801"),sQuery(id+"F0.wireOp",EDGE,"E802"),sQuery(id+"F0.wireOp",EDGE,"E803"),sQuery(id+"F0.wireOp",EDGE,"E804"),sQuery(id+"F0.wireOp",EDGE,"E805"),sQuery(id+"F0.wireOp",EDGE,"E806"),sQuery(id+"F0.wireOp",EDGE,"E807"),sQuery(id+"F0.wireOp",EDGE,"E808"),sQuery(id+"F0.wireOp",EDGE,"E809"),sQuery(id+"F0.wireOp",EDGE,"E810"),sQuery(id+"F0.wireOp",EDGE,"E811"),sQuery(id+"F0.wireOp",EDGE,"E812"),sQuery(id+"F0.wireOp",EDGE,"E813"),sQuery(id+"F0.wireOp",EDGE,"E814"),sQuery(id+"F0.wireOp",EDGE,"E815"),sQuery(id+"F0.wireOp",EDGE,"E816"),sQuery(id+"F0.wireOp",EDGE,"E817"),sQuery(id+"F0.wireOp",EDGE,"E818"),sQuery(id+"F0.wireOp",EDGE,"E819"),sQuery(id+"F0.wireOp",EDGE,"E820"),sQuery(id+"F0.wireOp",EDGE,"E821"),sQuery(id+"F0.wireOp",EDGE,"E822"),sQuery(id+"F0.wireOp",EDGE,"E823"),sQuery(id+"F0.wireOp",EDGE,"E824"),sQuery(id+"F0.wireOp",EDGE,"E825"),sQuery(id+"F0.wireOp",EDGE,"E826"),sQuery(id+"F0.wireOp",EDGE,"E827"),sQuery(id+"F0.wireOp",EDGE,"E828"),sQuery(id+"F0.wireOp",EDGE,"E829"),sQuery(id+"F0.wireOp",EDGE,"E830"),sQuery(id+"F0.wireOp",EDGE,"E831"),sQuery(id+"F0.wireOp",EDGE,"E832"),sQuery(id+"F0.wireOp",EDGE,"E833"),sQuery(id+"F0.wireOp",EDGE,"E834"),sQuery(id+"F0.wireOp",EDGE,"E835"),sQuery(id+"F0.wireOp",EDGE,"E836"),sQuery(id+"F0.wireOp",EDGE,"E837"),sQuery(id+"F0.wireOp",EDGE,"E838"),sQuery(id+"F0.wireOp",EDGE,"E839"),sQuery(id+"F0.wireOp",EDGE,"E840"),sQuery(id+"F0.wireOp",EDGE,"E841"),sQuery(id+"F0.wireOp",EDGE,"E842"),sQuery(id+"F0.wireOp",EDGE,"E843"),sQuery(id+"F0.wireOp",EDGE,"E844"),sQuery(id+"F0.wireOp",EDGE,"E845"),sQuery(id+"F0.wireOp",EDGE,"E846"),sQuery(id+"F0.wireOp",EDGE,"E847"),sQuery(id+"F0.wireOp",EDGE,"E848"),sQuery(id+"F0.wireOp",EDGE,"E849"),sQuery(id+"F0.wireOp",EDGE,"E850"),sQuery(id+"F0.wireOp",EDGE,"E851"),sQuery(id+"F0.wireOp",EDGE,"E852"),sQuery(id+"F0.wireOp",EDGE,"E853"),sQuery(id+"F0.wireOp",EDGE,"E854"),sQuery(id+"F0.wireOp",EDGE,"E855"),sQuery(id+"F0.wireOp",EDGE,"E856"),sQuery(id+"F0.wireOp",EDGE,"E857"),sQuery(id+"F0.wireOp",EDGE,"E858"),sQuery(id+"F0.wireOp",EDGE,"E859"),sQuery(id+"F0.wireOp",EDGE,"E860"),sQuery(id+"F0.wireOp",EDGE,"E861"),sQuery(id+"F0.wireOp",EDGE,"E862"),sQuery(id+"F0.wireOp",EDGE,"E863"),sQuery(id+"F0.wireOp",EDGE,"E864"),sQuery(id+"F0.wireOp",EDGE,"E865"),sQuery(id+"F0.wireOp",EDGE,"E866"),sQuery(id+"F0.wireOp",EDGE,"E867"),sQuery(id+"F0.wireOp",EDGE,"E868"),sQuery(id+"F0.wireOp",EDGE,"E869"),sQuery(id+"F0.wireOp",EDGE,"E870"),sQuery(id+"F0.wireOp",EDGE,"E871"),sQuery(id+"F0.wireOp",EDGE,"E872"),sQuery(id+"F0.wireOp",EDGE,"E873"),sQuery(id+"F0.wireOp",EDGE,"E874"),sQuery(id+"F0.wireOp",EDGE,"E875"),sQuery(id+"F0.wireOp",EDGE,"E876"),sQuery(id+"F0.wireOp",EDGE,"E877"),sQuery(id+"F0.wireOp",EDGE,"E878"),sQuery(id+"F0.wireOp",EDGE,"E879"),sQuery(id+"F0.wireOp",EDGE,"E880"),sQuery(id+"F0.wireOp",EDGE,"E881"),sQuery(id+"F0.wireOp",EDGE,"E882"),sQuery(id+"F0.wireOp",EDGE,"E883"),sQuery(id+"F0.wireOp",EDGE,"E884"),sQuery(id+"F0.wireOp",EDGE,"E885"),sQuery(id+"F0.wireOp",EDGE,"E886"),sQuery(id+"F0.wireOp",EDGE,"E887"),sQuery(id+"F0.wireOp",EDGE,"E888"),sQuery(id+"F0.wireOp",EDGE,"E889"),sQuery(id+"F0.wireOp",EDGE,"E890"),sQuery(id+"F0.wireOp",EDGE,"E891"),sQuery(id+"F0.wireOp",EDGE,"E892"),sQuery(id+"F0.wireOp",EDGE,"E893"),sQuery(id+"F0.wireOp",EDGE,"E894"),sQuery(id+"F0.wireOp",EDGE,"E895"),sQuery(id+"F0.wireOp",EDGE,"E896"),sQuery(id+"F0.wireOp",EDGE,"E897"),sQuery(id+"F0.wireOp",EDGE,"E898"),sQuery(id+"F0.wireOp",EDGE,"E899"),sQuery(id+"F0.wireOp",EDGE,"E900"),sQuery(id+"F0.wireOp",EDGE,"E901"),sQuery(id+"F0.wireOp",EDGE,"E902"),sQuery(id+"F0.wireOp",EDGE,"E903"),sQuery(id+"F0.wireOp",EDGE,"E904"),sQuery(id+"F0.wireOp",EDGE,"E905"),sQuery(id+"F0.wireOp",EDGE,"E906"),sQuery(id+"F0.wireOp",EDGE,"E907"),sQuery(id+"F0.wireOp",EDGE,"E908"),sQuery(id+"F0.wireOp",EDGE,"E909"),sQuery(id+"F0.wireOp",EDGE,"E910"),sQuery(id+"F0.wireOp",EDGE,"E911"),sQuery(id+"F0.wireOp",EDGE,"E912"),sQuery(id+"F0.wireOp",EDGE,"E913"),sQuery(id+"F0.wireOp",EDGE,"E914"),sQuery(id+"F0.wireOp",EDGE,"E915"),sQuery(id+"F0.wireOp",EDGE,"E916"),sQuery(id+"F0.wireOp",EDGE,"E917"),sQuery(id+"F0.wireOp",EDGE,"E918"),sQuery(id+"F0.wireOp",EDGE,"E919"),sQuery(id+"F0.wireOp",EDGE,"E920"),sQuery(id+"F0.wireOp",EDGE,"E921"),sQuery(id+"F0.wireOp",EDGE,"E922"),sQuery(id+"F0.wireOp",EDGE,"E923"),sQuery(id+"F0.wireOp",EDGE,"E924"),sQuery(id+"F0.wireOp",EDGE,"E925"),sQuery(id+"F0.wireOp",EDGE,"E926"),sQuery(id+"F0.wireOp",EDGE,"E927"),sQuery(id+"F0.wireOp",EDGE,"E928"),sQuery(id+"F0.wireOp",EDGE,"E929"),sQuery(id+"F0.wireOp",EDGE,"E930"),sQuery(id+"F0.wireOp",EDGE,"E931"),sQuery(id+"F0.wireOp",EDGE,"E932"),sQuery(id+"F0.wireOp",EDGE,"E933"),sQuery(id+"F0.wireOp",EDGE,"E934"),sQuery(id+"F0.wireOp",EDGE,"E935"),sQuery(id+"F0.wireOp",EDGE,"E936"),sQuery(id+"F0.wireOp",EDGE,"E937"),sQuery(id+"F0.wireOp",EDGE,"E938"),sQuery(id+"F0.wireOp",EDGE,"E939"),sQuery(id+"F0.wireOp",EDGE,"E940"),sQuery(id+"F0.wireOp",EDGE,"E941"),sQuery(id+"F0.wireOp",EDGE,"E942"),sQuery(id+"F0.wireOp",EDGE,"E943"),sQuery(id+"F0.wireOp",EDGE,"E944"),sQuery(id+"F0.wireOp",EDGE,"E945"),sQuery(id+"F0.wireOp",EDGE,"E946"),sQuery(id+"F0.wireOp",EDGE,"E947"),sQuery(id+"F0.wireOp",EDGE,"E948"),sQuery(id+"F0.wireOp",EDGE,"E949"),sQuery(id+"F0.wireOp",EDGE,"E950"),sQuery(id+"F0.wireOp",EDGE,"E951"),sQuery(id+"F0.wireOp",EDGE,"E952"),sQuery(id+"F0.wireOp",EDGE,"E953"),sQuery(id+"F0.wireOp",EDGE,"E954"),sQuery(id+"F0.wireOp",EDGE,"E955"),sQuery(id+"F0.wireOp",EDGE,"E956"),sQuery(id+"F0.wireOp",EDGE,"E957"),sQuery(id+"F0.wireOp",EDGE,"E958"),sQuery(id+"F0.wireOp",EDGE,"E959"),sQuery(id+"F0.wireOp",EDGE,"E960"),sQuery(id+"F0.wireOp",EDGE,"E961"),sQuery(id+"F0.wireOp",EDGE,"E962"),sQuery(id+"F0.wireOp",EDGE,"E963"),sQuery(id+"F0.wireOp",EDGE,"E964"),sQuery(id+"F0.wireOp",EDGE,"E965"),sQuery(id+"F0.wireOp",EDGE,"E966"),sQuery(id+"F0.wireOp",EDGE,"E967"),sQuery(id+"F0.wireOp",EDGE,"E968"),sQuery(id+"F0.wireOp",EDGE,"E969"),sQuery(id+"F0.wireOp",EDGE,"E970"),sQuery(id+"F0.wireOp",EDGE,"E971"),sQuery(id+"F0.wireOp",EDGE,"E972"),sQuery(id+"F0.wireOp",EDGE,"E973"),sQuery(id+"F0.wireOp",EDGE,"E974"),sQuery(id+"F0.wireOp",EDGE,"E975"),sQuery(id+"F0.wireOp",EDGE,"E976"),sQuery(id+"F0.wireOp",EDGE,"E977"),sQuery(id+"F0.wireOp",EDGE,"E978"),sQuery(id+"F0.wireOp",EDGE,"E979"),sQuery(id+"F0.wireOp",EDGE,"E980"),sQuery(id+"F0.wireOp",EDGE,"E981"),sQuery(id+"F0.wireOp",EDGE,"E982"),sQuery(id+"F0.wireOp",EDGE,"E983"),sQuery(id+"F0.wireOp",EDGE,"E984"),sQuery(id+"F0.wireOp",EDGE,"E985"),sQuery(id+"F0.wireOp",EDGE,"E986"),sQuery(id+"F0.wireOp",EDGE,"E987"),sQuery(id+"F0.wireOp",EDGE,"E988"),sQuery(id+"F0.wireOp",EDGE,"E989"),sQuery(id+"F0.wireOp",EDGE,"E990"),sQuery(id+"F0.wireOp",EDGE,"E991"),sQuery(id+"F0.wireOp",EDGE,"E992"),sQuery(id+"F0.wireOp",EDGE,"E993"),sQuery(id+"F0.wireOp",EDGE,"E994"),sQuery(id+"F0.wireOp",EDGE,"E995"),sQuery(id+"F0.wireOp",EDGE,"E996"),sQuery(id+"F0.wireOp",EDGE,"E997"),sQuery(id+"F0.wireOp",EDGE,"E998"),sQuery(id+"F0.wireOp",EDGE,"E999"),sQuery(id+"F0.wireOp",EDGE,"E1000"),sQuery(id+"F0.wireOp",EDGE,"E1001"),sQuery(id+"F0.wireOp",EDGE,"E1002"),sQuery(id+"F0.wireOp",EDGE,"E1003"),sQuery(id+"F0.wireOp",EDGE,"E1004"),sQuery(id+"F0.wireOp",EDGE,"E1005"),sQuery(id+"F0.wireOp",EDGE,"E1006"),sQuery(id+"F0.wireOp",EDGE,"E1007"),sQuery(id+"F0.wireOp",EDGE,"E1008"),sQuery(id+"F0.wireOp",EDGE,"E1009"),sQuery(id+"F0.wireOp",EDGE,"E1010"),sQuery(id+"F0.wireOp",EDGE,"E1011"),sQuery(id+"F0.wireOp",EDGE,"E1012"),sQuery(id+"F0.wireOp",EDGE,"E1013"),sQuery(id+"F0.wireOp",EDGE,"E1014"),sQuery(id+"F0.wireOp",EDGE,"E1015"),sQuery(id+"F0.wireOp",EDGE,"E1016"),sQuery(id+"F0.wireOp",EDGE,"E1017"),sQuery(id+"F0.wireOp",EDGE,"E1018"),sQuery(id+"F0.wireOp",EDGE,"E1019"),sQuery(id+"F0.wireOp",EDGE,"E1020"),sQuery(id+"F0.wireOp",EDGE,"E1021"),sQuery(id+"F0.wireOp",EDGE,"E1022"),sQuery(id+"F0.wireOp",EDGE,"E1023"),sQuery(id+"F0.wireOp",EDGE,"E1024"),sQuery(id+"F0.wireOp",EDGE,"E1025"),sQuery(id+"F0.wireOp",EDGE,"E1026"),sQuery(id+"F0.wireOp",EDGE,"E1027"),sQuery(id+"F0.wireOp",EDGE,"E1028"),sQuery(id+"F0.wireOp",EDGE,"E1029"),sQuery(id+"F0.wireOp",EDGE,"E1030"),sQuery(id+"F0.wireOp",EDGE,"E1031"),sQuery(id+"F0.wireOp",EDGE,"E1032"),sQuery(id+"F0.wireOp",EDGE,"E1033"),sQuery(id+"F0.wireOp",EDGE,"E1034"),sQuery(id+"F0.wireOp",EDGE,"E1035"),sQuery(id+"F0.wireOp",EDGE,"E1036"),sQuery(id+"F0.wireOp",EDGE,"E1037"),sQuery(id+"F0.wireOp",EDGE,"E1038"),sQuery(id+"F0.wireOp",EDGE,"E1039"),sQuery(id+"F0.wireOp",EDGE,"E1040"),sQuery(id+"F0.wireOp",EDGE,"E1041"),sQuery(id+"F0.wireOp",EDGE,"E1042"),sQuery(id+"F0.wireOp",EDGE,"E1043"),sQuery(id+"F0.wireOp",EDGE,"E1044"),sQuery(id+"F0.wireOp",EDGE,"E1045"),sQuery(id+"F0.wireOp",EDGE,"E1046"),sQuery(id+"F0.wireOp",EDGE,"E1047"),sQuery(id+"F0.wireOp",EDGE,"E1048"),sQuery(id+"F0.wireOp",EDGE,"E1049"),sQuery(id+"F0.wireOp",EDGE,"E1050"),sQuery(id+"F0.wireOp",EDGE,"E1051"),sQuery(id+"F0.wireOp",EDGE,"E1052"),sQuery(id+"F0.wireOp",EDGE,"E1053"),sQuery(id+"F0.wireOp",EDGE,"E1054"),sQuery(id+"F0.wireOp",EDGE,"E1055"),sQuery(id+"F0.wireOp",EDGE,"E1056"),sQuery(id+"F0.wireOp",EDGE,"E1057"),sQuery(id+"F0.wireOp",EDGE,"E1058"),sQuery(id+"F0.wireOp",EDGE,"E1059"),sQuery(id+"F0.wireOp",EDGE,"E1060"),sQuery(id+"F0.wireOp",EDGE,"E1061"),sQuery(id+"F0.wireOp",EDGE,"E1062"),sQuery(id+"F0.wireOp",EDGE,"E1063"),sQuery(id+"F0.wireOp",EDGE,"E1064"),sQuery(id+"F0.wireOp",EDGE,"E1065"),sQuery(id+"F0.wireOp",EDGE,"E1066"),sQuery(id+"F0.wireOp",EDGE,"E1067"),sQuery(id+"F0.wireOp",EDGE,"E1068"),sQuery(id+"F0.wireOp",EDGE,"E1069"),sQuery(id+"F0.wireOp",EDGE,"E1070"),sQuery(id+"F0.wireOp",EDGE,"E1071"),sQuery(id+"F0.wireOp",EDGE,"E1072"),sQuery(id+"F0.wireOp",EDGE,"E1073"),sQuery(id+"F0.wireOp",EDGE,"E1074"),sQuery(id+"F0.wireOp",EDGE,"E1075"),sQuery(id+"F0.wireOp",EDGE,"E1076"),sQuery(id+"F0.wireOp",EDGE,"E1077"),sQuery(id+"F0.wireOp",EDGE,"E1078"),sQuery(id+"F0.wireOp",EDGE,"E1079"),sQuery(id+"F0.wireOp",EDGE,"E1080"),sQuery(id+"F0.wireOp",EDGE,"E1081"),sQuery(id+"F0.wireOp",EDGE,"E1082"),sQuery(id+"F0.wireOp",EDGE,"E1083"),sQuery(id+"F0.wireOp",EDGE,"E1084"),sQuery(id+"F0.wireOp",EDGE,"E1085"),sQuery(id+"F0.wireOp",EDGE,"E1086"),sQuery(id+"F0.wireOp",EDGE,"E1087"),sQuery(id+"F0.wireOp",EDGE,"E1088"),sQuery(id+"F0.wireOp",EDGE,"E1089"),sQuery(id+"F0.wireOp",EDGE,"E1090"),sQuery(id+"F0.wireOp",EDGE,"E1091"),sQuery(id+"F0.wireOp",EDGE,"E1092"),sQuery(id+"F0.wireOp",EDGE,"E1093"),sQuery(id+"F0.wireOp",EDGE,"E1094"),sQuery(id+"F0.wireOp",EDGE,"E1095"),sQuery(id+"F0.wireOp",EDGE,"E1096"),sQuery(id+"F0.wireOp",EDGE,"E1097"),sQuery(id+"F0.wireOp",EDGE,"E1098"),sQuery(id+"F0.wireOp",EDGE,"E1099"),sQuery(id+"F0.wireOp",EDGE,"E1100"),sQuery(id+"F0.wireOp",EDGE,"E1101"),sQuery(id+"F0.wireOp",EDGE,"E1102"),sQuery(id+"F0.wireOp",EDGE,"E1103"),sQuery(id+"F0.wireOp",EDGE,"E1104"),sQuery(id+"F0.wireOp",EDGE,"E1105"),sQuery(id+"F0.wireOp",EDGE,"E1106"),sQuery(id+"F0.wireOp",EDGE,"E1107"),sQuery(id+"F0.wireOp",EDGE,"E1108"),sQuery(id+"F0.wireOp",EDGE,"E1109"),sQuery(id+"F0.wireOp",EDGE,"E1110"),sQuery(id+"F0.wireOp",EDGE,"E1111"),sQuery(id+"F0.wireOp",EDGE,"E1112"),sQuery(id+"F0.wireOp",EDGE,"E1113"),sQuery(id+"F0.wireOp",EDGE,"E1114"),sQuery(id+"F0.wireOp",EDGE,"E1115"),sQuery(id+"F0.wireOp",EDGE,"E1116"),sQuery(id+"F0.wireOp",EDGE,"E1117"),sQuery(id+"F0.wireOp",EDGE,"E1118"),sQuery(id+"F0.wireOp",EDGE,"E1119"),sQuery(id+"F0.wireOp",EDGE,"E1120"),sQuery(id+"F0.wireOp",EDGE,"E1121"),sQuery(id+"F0.wireOp",EDGE,"E1122"),sQuery(id+"F0.wireOp",EDGE,"E1123"),sQuery(id+"F0.wireOp",EDGE,"E1124"),sQuery(id+"F0.wireOp",EDGE,"E1125"),sQuery(id+"F0.wireOp",EDGE,"E1126"),sQuery(id+"F0.wireOp",EDGE,"E1127"),sQuery(id+"F0.wireOp",EDGE,"E1128"),sQuery(id+"F0.wireOp",EDGE,"E1129"),sQuery(id+"F0.wireOp",EDGE,"E1130"),sQuery(id+"F0.wireOp",EDGE,"E1131"),sQuery(id+"F0.wireOp",EDGE,"E1132"),sQuery(id+"F0.wireOp",EDGE,"E1133"),sQuery(id+"F0.wireOp",EDGE,"E1134"),sQuery(id+"F0.wireOp",EDGE,"E1135"),sQuery(id+"F0.wireOp",EDGE,"E1136"),sQuery(id+"F0.wireOp",EDGE,"E1137"),sQuery(id+"F0.wireOp",EDGE,"E1138"),sQuery(id+"F0.wireOp",EDGE,"E1139"),sQuery(id+"F0.wireOp",EDGE,"E1140"),sQuery(id+"F0.wireOp",EDGE,"E1141"),sQuery(id+"F0.wireOp",EDGE,"E1142"),sQuery(id+"F0.wireOp",EDGE,"E1143"),sQuery(id+"F0.wireOp",EDGE,"E1144"),sQuery(id+"F0.wireOp",EDGE,"E1145"),sQuery(id+"F0.wireOp",EDGE,"E1146"),sQuery(id+"F0.wireOp",EDGE,"E1147"),sQuery(id+"F0.wireOp",EDGE,"E1148"),sQuery(id+"F0.wireOp",EDGE,"E1149"),sQuery(id+"F0.wireOp",EDGE,"E1150"),sQuery(id+"F0.wireOp",EDGE,"E1151"),sQuery(id+"F0.wireOp",EDGE,"E1152"),sQuery(id+"F0.wireOp",EDGE,"E1153"),sQuery(id+"F0.wireOp",EDGE,"E1154"),sQuery(id+"F0.wireOp",EDGE,"E1155"),sQuery(id+"F0.wireOp",EDGE,"E1156"),sQuery(id+"F0.wireOp",EDGE,"E1157"),sQuery(id+"F0.wireOp",EDGE,"E1158"),sQuery(id+"F0.wireOp",EDGE,"E1159"),sQuery(id+"F0.wireOp",EDGE,"E1160"),sQuery(id+"F0.wireOp",EDGE,"E1161"),sQuery(id+"F0.wireOp",EDGE,"E1162"),sQuery(id+"F0.wireOp",EDGE,"E1163"),sQuery(id+"F0.wireOp",EDGE,"E1164"),sQuery(id+"F0.wireOp",EDGE,"E1165"),sQuery(id+"F0.wireOp",EDGE,"E1166"),sQuery(id+"F0.wireOp",EDGE,"E1167"),sQuery(id+"F0.wireOp",EDGE,"E1168"),sQuery(id+"F0.wireOp",EDGE,"E1169"),sQuery(id+"F0.wireOp",EDGE,"E1170"),sQuery(id+"F0.wireOp",EDGE,"E1171"),sQuery(id+"F0.wireOp",EDGE,"E1172"),sQuery(id+"F0.wireOp",EDGE,"E1173"),sQuery(id+"F0.wireOp",EDGE,"E1174"),sQuery(id+"F0.wireOp",EDGE,"E1175"),sQuery(id+"F0.wireOp",EDGE,"E1176"),sQuery(id+"F0.wireOp",EDGE,"E1177"),sQuery(id+"F0.wireOp",EDGE,"E1178"),sQuery(id+"F0.wireOp",EDGE,"E1179"),sQuery(id+"F0.wireOp",EDGE,"E1180"),sQuery(id+"F0.wireOp",EDGE,"E1181"),sQuery(id+"F0.wireOp",EDGE,"E1182"),sQuery(id+"F0.wireOp",EDGE,"E1183"),sQuery(id+"F0.wireOp",EDGE,"E1184"),sQuery(id+"F0.wireOp",EDGE,"E1185"),sQuery(id+"F0.wireOp",EDGE,"E1186"),sQuery(id+"F0.wireOp",EDGE,"E1187"),sQuery(id+"F0.wireOp",EDGE,"E1188"),sQuery(id+"F0.wireOp",EDGE,"E1189"),sQuery(id+"F0.wireOp",EDGE,"E1190"),sQuery(id+"F0.wireOp",EDGE,"E1191"),sQuery(id+"F0.wireOp",EDGE,"E1192"),sQuery(id+"F0.wireOp",EDGE,"E1193"),sQuery(id+"F0.wireOp",EDGE,"E1194"),sQuery(id+"F0.wireOp",EDGE,"E1195"),sQuery(id+"F0.wireOp",EDGE,"E1196"),sQuery(id+"F0.wireOp",EDGE,"E1197"),sQuery(id+"F0.wireOp",EDGE,"E1198"),sQuery(id+"F0.wireOp",EDGE,"E1199"),sQuery(id+"F0.wireOp",EDGE,"E1200"),sQuery(id+"F0.wireOp",EDGE,"E1201"),sQuery(id+"F0.wireOp",EDGE,"E1202"),sQuery(id+"F0.wireOp",EDGE,"E1203"),sQuery(id+"F0.wireOp",EDGE,"E1204"),sQuery(id+"F0.wireOp",EDGE,"E1205"),sQuery(id+"F0.wireOp",EDGE,"E1206"),sQuery(id+"F0.wireOp",EDGE,"E1207"),sQuery(id+"F0.wireOp",EDGE,"E1208"),sQuery(id+"F0.wireOp",EDGE,"E1209"),sQuery(id+"F0.wireOp",EDGE,"E1210"),sQuery(id+"F0.wireOp",EDGE,"E1211"),sQuery(id+"F0.wireOp",EDGE,"E1212"),sQuery(id+"F0.wireOp",EDGE,"E1213"),sQuery(id+"F0.wireOp",EDGE,"E1214"),sQuery(id+"F0.wireOp",EDGE,"E1215"),sQuery(id+"F0.wireOp",EDGE,"E1216"),sQuery(id+"F0.wireOp",EDGE,"E1217"),sQuery(id+"F0.wireOp",EDGE,"E1218"),sQuery(id+"F0.wireOp",EDGE,"E1219"),sQuery(id+"F0.wireOp",EDGE,"E1220"),sQuery(id+"F0.wireOp",EDGE,"E1221"),sQuery(id+"F0.wireOp",EDGE,"E1222"),sQuery(id+"F0.wireOp",EDGE,"E1223"),sQuery(id+"F0.wireOp",EDGE,"E1224"),sQuery(id+"F0.wireOp",EDGE,"E1225"),sQuery(id+"F0.wireOp",EDGE,"E1226"),sQuery(id+"F0.wireOp",EDGE,"E1227"),sQuery(id+"F0.wireOp",EDGE,"E1228"),sQuery(id+"F0.wireOp",EDGE,"E1229"),sQuery(id+"F0.wireOp",EDGE,"E1230"),sQuery(id+"F0.wireOp",EDGE,"E1231"),sQuery(id+"F0.wireOp",EDGE,"E1232"),sQuery(id+"F0.wireOp",EDGE,"E1233"),sQuery(id+"F0.wireOp",EDGE,"E1234"),sQuery(id+"F0.wireOp",EDGE,"E1235"),sQuery(id+"F0.wireOp",EDGE,"E1236"),sQuery(id+"F0.wireOp",EDGE,"E1237"),sQuery(id+"F0.wireOp",EDGE,"E1238"),sQuery(id+"F0.wireOp",EDGE,"E1239"),sQuery(id+"F0.wireOp",EDGE,"E1240"),sQuery(id+"F0.wireOp",EDGE,"E1241"),sQuery(id+"F0.wireOp",EDGE,"E1242"),sQuery(id+"F0.wireOp",EDGE,"E1243"),sQuery(id+"F0.wireOp",EDGE,"E1244"),sQuery(id+"F0.wireOp",EDGE,"E1245"),sQuery(id+"F0.wireOp",EDGE,"E1246"),sQuery(id+"F0.wireOp",EDGE,"E1247"),sQuery(id+"F0.wireOp",EDGE,"E1248"),sQuery(id+"F0.wireOp",EDGE,"E1249"),sQuery(id+"F0.wireOp",EDGE,"E1250"),sQuery(id+"F0.wireOp",EDGE,"E1251"),sQuery(id+"F0.wireOp",EDGE,"E1252"),sQuery(id+"F0.wireOp",EDGE,"E1253"),sQuery(id+"F0.wireOp",EDGE,"E1254"),sQuery(id+"F0.wireOp",EDGE,"E1255"),sQuery(id+"F0.wireOp",EDGE,"E1256"),sQuery(id+"F0.wireOp",EDGE,"E1257"),sQuery(id+"F0.wireOp",EDGE,"E1258"),sQuery(id+"F0.wireOp",EDGE,"E1259"),sQuery(id+"F0.wireOp",EDGE,"E1260"),sQuery(id+"F0.wireOp",EDGE,"E1261"),sQuery(id+"F0.wireOp",EDGE,"E1262"),sQuery(id+"F0.wireOp",EDGE,"E1263"),sQuery(id+"F0.wireOp",EDGE,"E1264"),sQuery(id+"F0.wireOp",EDGE,"E1265"),sQuery(id+"F0.wireOp",EDGE,"E1266"),sQuery(id+"F0.wireOp",EDGE,"E1267"),sQuery(id+"F0.wireOp",EDGE,"E1268"),sQuery(id+"F0.wireOp",EDGE,"E1269"),sQuery(id+"F0.wireOp",EDGE,"E1270"),sQuery(id+"F0.wireOp",EDGE,"E1271"),sQuery(id+"F0.wireOp",EDGE,"E1272"),sQuery(id+"F0.wireOp",EDGE,"E1273"),sQuery(id+"F0.wireOp",EDGE,"E1274"),sQuery(id+"F0.wireOp",EDGE,"E1275"),sQuery(id+"F0.wireOp",EDGE,"E1276"),sQuery(id+"F0.wireOp",EDGE,"E1277"),sQuery(id+"F0.wireOp",EDGE,"E1278"),sQuery(id+"F0.wireOp",EDGE,"E1279"),sQuery(id+"F0.wireOp",EDGE,"E1280"),sQuery(id+"F0.wireOp",EDGE,"E1281"),sQuery(id+"F0.wireOp",EDGE,"E1282"),sQuery(id+"F0.wireOp",EDGE,"E1283"),sQuery(id+"F0.wireOp",EDGE,"E1284"),sQuery(id+"F0.wireOp",EDGE,"E1285"),sQuery(id+"F0.wireOp",EDGE,"E1286"),sQuery(id+"F0.wireOp",EDGE,"E1287"),sQuery(id+"F0.wireOp",EDGE,"E1288"),sQuery(id+"F0.wireOp",EDGE,"E1289"),sQuery(id+"F0.wireOp",EDGE,"E1290"),sQuery(id+"F0.wireOp",EDGE,"E1291"),sQuery(id+"F0.wireOp",EDGE,"E1292"),sQuery(id+"F0.wireOp",EDGE,"E1293"),sQuery(id+"F0.wireOp",EDGE,"E1294"),sQuery(id+"F0.wireOp",EDGE,"E1295"),sQuery(id+"F0.wireOp",EDGE,"E1296"),sQuery(id+"F0.wireOp",EDGE,"E1297"),sQuery(id+"F0.wireOp",EDGE,"E1298"),sQuery(id+"F0.wireOp",EDGE,"E1299"),sQuery(id+"F0.wireOp",EDGE,"E1300"),sQuery(id+"F0.wireOp",EDGE,"E1301"),sQuery(id+"F0.wireOp",EDGE,"E1302"),sQuery(id+"F0.wireOp",EDGE,"E1303"),sQuery(id+"F0.wireOp",EDGE,"E1304"),sQuery(id+"F0.wireOp",EDGE,"E1305"),sQuery(id+"F0.wireOp",EDGE,"E1306"),sQuery(id+"F0.wireOp",EDGE,"E1307"),sQuery(id+"F0.wireOp",EDGE,"E1308"),sQuery(id+"F0.wireOp",EDGE,"E1309"),sQuery(id+"F0.wireOp",EDGE,"E1310"),sQuery(id+"F0.wireOp",EDGE,"E1311"),sQuery(id+"F0.wireOp",EDGE,"E1312"),sQuery(id+"F0.wireOp",EDGE,"E1313"),sQuery(id+"F0.wireOp",EDGE,"E1314"),sQuery(id+"F0.wireOp",EDGE,"E1315"),sQuery(id+"F0.wireOp",EDGE,"E1316"),sQuery(id+"F0.wireOp",EDGE,"E1317"),sQuery(id+"F0.wireOp",EDGE,"E1318"),sQuery(id+"F0.wireOp",EDGE,"E1319"),sQuery(id+"F0.wireOp",EDGE,"E1320"),sQuery(id+"F0.wireOp",EDGE,"E1321"),sQuery(id+"F0.wireOp",EDGE,"E1322"),sQuery(id+"F0.wireOp",EDGE,"E1323"),sQuery(id+"F0.wireOp",EDGE,"E1324"),sQuery(id+"F0.wireOp",EDGE,"E1325"),sQuery(id+"F0.wireOp",EDGE,"E1326"),sQuery(id+"F0.wireOp",EDGE,"E1327"),sQuery(id+"F0.wireOp",EDGE,"E1328"),sQuery(id+"F0.wireOp",EDGE,"E1329"),sQuery(id+"F0.wireOp",EDGE,"E1330"),sQuery(id+"F0.wireOp",EDGE,"E1331"),sQuery(id+"F0.wireOp",EDGE,"E1332"),sQuery(id+"F0.wireOp",EDGE,"E1333"),sQuery(id+"F0.wireOp",EDGE,"E1334"),sQuery(id+"F0.wireOp",EDGE,"E1335"),sQuery(id+"F0.wireOp",EDGE,"E1336"),sQuery(id+"F0.wireOp",EDGE,"E1337"),sQuery(id+"F0.wireOp",EDGE,"E1338"),sQuery(id+"F0.wireOp",EDGE,"E1339"),sQuery(id+"F0.wireOp",EDGE,"E1340"),sQuery(id+"F0.wireOp",EDGE,"E1341"),sQuery(id+"F0.wireOp",EDGE,"E1342"),sQuery(id+"F0.wireOp",EDGE,"E1343"),sQuery(id+"F0.wireOp",EDGE,"E1344"),sQuery(id+"F0.wireOp",EDGE,"E1345"),sQuery(id+"F0.wireOp",EDGE,"E1346"),sQuery(id+"F0.wireOp",EDGE,"E1347"),sQuery(id+"F0.wireOp",EDGE,"E1348"),sQuery(id+"F0.wireOp",EDGE,"E1349"),sQuery(id+"F0.wireOp",EDGE,"E1350"),sQuery(id+"F0.wireOp",EDGE,"E1351"),sQuery(id+"F0.wireOp",EDGE,"E1352"),sQuery(id+"F0.wireOp",EDGE,"E1353"),sQuery(id+"F0.wireOp",EDGE,"E1354"),sQuery(id+"F0.wireOp",EDGE,"E1355"),sQuery(id+"F0.wireOp",EDGE,"E1356"),sQuery(id+"F0.wireOp",EDGE,"E1357"),sQuery(id+"F0.wireOp",EDGE,"E1358"),sQuery(id+"F0.wireOp",EDGE,"E1359"),sQuery(id+"F0.wireOp",EDGE,"E1360"),sQuery(id+"F0.wireOp",EDGE,"E1361"),sQuery(id+"F0.wireOp",EDGE,"E1362"),sQuery(id+"F0.wireOp",EDGE,"E1363"),sQuery(id+"F0.wireOp",EDGE,"E1364"),sQuery(id+"F0.wireOp",EDGE,"E1365"),sQuery(id+"F0.wireOp",EDGE,"E1366"),sQuery(id+"F0.wireOp",EDGE,"E1367"),sQuery(id+"F0.wireOp",EDGE,"E1368"),sQuery(id+"F0.wireOp",EDGE,"E1369"),sQuery(id+"F0.wireOp",EDGE,"E1370"),sQuery(id+"F0.wireOp",EDGE,"E1371"),sQuery(id+"F0.wireOp",EDGE,"E1372"),sQuery(id+"F0.wireOp",EDGE,"E1373"),sQuery(id+"F0.wireOp",EDGE,"E1374"),sQuery(id+"F0.wireOp",EDGE,"E1375"),sQuery(id+"F0.wireOp",EDGE,"E1376"),sQuery(id+"F0.wireOp",EDGE,"E1377"),sQuery(id+"F0.wireOp",EDGE,"E1378"),sQuery(id+"F0.wireOp",EDGE,"E1379"),sQuery(id+"F0.wireOp",EDGE,"E1380"),sQuery(id+"F0.wireOp",EDGE,"E1381"),sQuery(id+"F0.wireOp",EDGE,"E1382"),sQuery(id+"F0.wireOp",EDGE,"E1383"),sQuery(id+"F0.wireOp",EDGE,"E1384"),sQuery(id+"F0.wireOp",EDGE,"E1385"),sQuery(id+"F0.wireOp",EDGE,"E1386"),sQuery(id+"F0.wireOp",EDGE,"E1387"),sQuery(id+"F0.wireOp",EDGE,"E1388"),sQuery(id+"F0.wireOp",EDGE,"E1389"),sQuery(id+"F0.wireOp",EDGE,"E1390"),sQuery(id+"F0.wireOp",EDGE,"E1391"),sQuery(id+"F0.wireOp",EDGE,"E1392"),sQuery(id+"F0.wireOp",EDGE,"E1393"),sQuery(id+"F0.wireOp",EDGE,"E1394"),sQuery(id+"F0.wireOp",EDGE,"E1395"),sQuery(id+"F0.wireOp",EDGE,"E1396"),sQuery(id+"F0.wireOp",EDGE,"E1397"),sQuery(id+"F0.wireOp",EDGE,"E1398"),sQuery(id+"F0.wireOp",EDGE,"E1399"),sQuery(id+"F0.wireOp",EDGE,"E1400"),sQuery(id+"F0.wireOp",EDGE,"E1401"),sQuery(id+"F0.wireOp",EDGE,"E1402"),sQuery(id+"F0.wireOp",EDGE,"E1403"),sQuery(id+"F0.wireOp",EDGE,"E1404"),sQuery(id+"F0.wireOp",EDGE,"E1405"),sQuery(id+"F0.wireOp",EDGE,"E1406"),sQuery(id+"F0.wireOp",EDGE,"E1407"),sQuery(id+"F0.wireOp",EDGE,"E1408"),sQuery(id+"F0.wireOp",EDGE,"E1409"),sQuery(id+"F0.wireOp",EDGE,"E1410"),sQuery(id+"F0.wireOp",EDGE,"E1411"),sQuery(id+"F0.wireOp",EDGE,"E1412"),sQuery(id+"F0.wireOp",EDGE,"E1413"),sQuery(id+"F0.wireOp",EDGE,"E1414"),sQuery(id+"F0.wireOp",EDGE,"E1415"),sQuery(id+"F0.wireOp",EDGE,"E1416"),sQuery(id+"F0.wireOp",EDGE,"E1417"),sQuery(id+"F0.wireOp",EDGE,"E1418"),sQuery(id+"F0.wireOp",EDGE,"E1419"),sQuery(id+"F0.wireOp",EDGE,"E1420"),sQuery(id+"F0.wireOp",EDGE,"E1421"),sQuery(id+"F0.wireOp",EDGE,"E1422"),sQuery(id+"F0.wireOp",EDGE,"E1423"),sQuery(id+"F0.wireOp",EDGE,"E1424"),sQuery(id+"F0.wireOp",EDGE,"E1425"),sQuery(id+"F0.wireOp",EDGE,"E1426"),sQuery(id+"F0.wireOp",EDGE,"E1427"),sQuery(id+"F0.wireOp",EDGE,"E1428"),sQuery(id+"F0.wireOp",EDGE,"E1429"),sQuery(id+"F0.wireOp",EDGE,"E1430"),sQuery(id+"F0.wireOp",EDGE,"E1431"),sQuery(id+"F0.wireOp",EDGE,"E1432"),sQuery(id+"F0.wireOp",EDGE,"E1433"),sQuery(id+"F0.wireOp",EDGE,"E1434"),sQuery(id+"F0.wireOp",EDGE,"E1435"),sQuery(id+"F0.wireOp",EDGE,"E1436"),sQuery(id+"F0.wireOp",EDGE,"E1437"),sQuery(id+"F0.wireOp",EDGE,"E1438"),sQuery(id+"F0.wireOp",EDGE,"E1439"),sQuery(id+"F0.wireOp",EDGE,"E1440"),sQuery(id+"F0.wireOp",EDGE,"E1441"),sQuery(id+"F0.wireOp",EDGE,"E1442"),sQuery(id+"F0.wireOp",EDGE,"E1443"),sQuery(id+"F0.wireOp",EDGE,"E1444"),sQuery(id+"F0.wireOp",EDGE,"E1445"),sQuery(id+"F0.wireOp",EDGE,"E1446"),sQuery(id+"F0.wireOp",EDGE,"E1447"),sQuery(id+"F0.wireOp",EDGE,"E1448"),sQuery(id+"F0.wireOp",EDGE,"E1449"),sQuery(id+"F0.wireOp",EDGE,"E1450"),sQuery(id+"F0.wireOp",EDGE,"E1451"),sQuery(id+"F0.wireOp",EDGE,"E1452"),sQuery(id+"F0.wireOp",EDGE,"E1453"),sQuery(id+"F0.wireOp",EDGE,"E1454"),sQuery(id+"F0.wireOp",EDGE,"E1455"),sQuery(id+"F0.wireOp",EDGE,"E1456"),sQuery(id+"F0.wireOp",EDGE,"E1457"),sQuery(id+"F0.wireOp",EDGE,"E1458"),sQuery(id+"F0.wireOp",EDGE,"E1459"),sQuery(id+"F0.wireOp",EDGE,"E1460"),sQuery(id+"F0.wireOp",EDGE,"E1461"),sQuery(id+"F0.wireOp",EDGE,"E1462"),sQuery(id+"F0.wireOp",EDGE,"E1463"),sQuery(id+"F0.wireOp",EDGE,"E1464"),sQuery(id+"F0.wireOp",EDGE,"E1465"),sQuery(id+"F0.wireOp",EDGE,"E1466"),sQuery(id+"F0.wireOp",EDGE,"E1467"),sQuery(id+"F0.wireOp",EDGE,"E1468"),sQuery(id+"F0.wireOp",EDGE,"E1469"),sQuery(id+"F0.wireOp",EDGE,"E1470"),sQuery(id+"F0.wireOp",EDGE,"E1471"),sQuery(id+"F0.wireOp",EDGE,"E1472"),sQuery(id+"F0.wireOp",EDGE,"E1473"),sQuery(id+"F0.wireOp",EDGE,"E1474"),sQuery(id+"F0.wireOp",EDGE,"E1475"),sQuery(id+"F0.wireOp",EDGE,"E1476"),sQuery(id+"F0.wireOp",EDGE,"E1477"),sQuery(id+"F0.wireOp",EDGE,"E1478"),sQuery(id+"F0.wireOp",EDGE,"E1479"),sQuery(id+"F0.wireOp",EDGE,"E1480"),sQuery(id+"F0.wireOp",EDGE,"E1481"),sQuery(id+"F0.wireOp",EDGE,"E1482"),sQuery(id+"F0.wireOp",EDGE,"E1483"),sQuery(id+"F0.wireOp",EDGE,"E1484"),sQuery(id+"F0.wireOp",EDGE,"E1485"),sQuery(id+"F0.wireOp",EDGE,"E1486"),sQuery(id+"F0.wireOp",EDGE,"E1487"),sQuery(id+"F0.wireOp",EDGE,"E1488"),sQuery(id+"F0.wireOp",EDGE,"E1489"),sQuery(id+"F0.wireOp",EDGE,"E1490"),sQuery(id+"F0.wireOp",EDGE,"E1491"),sQuery(id+"F0.wireOp",EDGE,"E1492"),sQuery(id+"F0.wireOp",EDGE,"E1493"),sQuery(id+"F0.wireOp",EDGE,"E1494"),sQuery(id+"F0.wireOp",EDGE,"E1495"),sQuery(id+"F0.wireOp",EDGE,"E1496"),sQuery(id+"F0.wireOp",EDGE,"E1497"),sQuery(id+"F0.wireOp",EDGE,"E1498"),sQuery(id+"F0.wireOp",EDGE,"E1499"),sQuery(id+"F0.wireOp",EDGE,"E1500"),sQuery(id+"F0.wireOp",EDGE,"E1501"),sQuery(id+"F0.wireOp",EDGE,"E1502"),sQuery(id+"F0.wireOp",EDGE,"E1503"),sQuery(id+"F0.wireOp",EDGE,"E1504"),sQuery(id+"F0.wireOp",EDGE,"E1505"),sQuery(id+"F0.wireOp",EDGE,"E1506"),sQuery(id+"F0.wireOp",EDGE,"E1507"),sQuery(id+"F0.wireOp",EDGE,"E1508"),sQuery(id+"F0.wireOp",EDGE,"E1509"),sQuery(id+"F0.wireOp",EDGE,"E1510"),sQuery(id+"F0.wireOp",EDGE,"E1511"),sQuery(id+"F0.wireOp",EDGE,"E1512"),sQuery(id+"F0.wireOp",EDGE,"E1513"),sQuery(id+"F0.wireOp",EDGE,"E1514"),sQuery(id+"F0.wireOp",EDGE,"E1515"),sQuery(id+"F0.wireOp",EDGE,"E1516"),sQuery(id+"F0.wireOp",EDGE,"E1517"),sQuery(id+"F0.wireOp",EDGE,"E1518"),sQuery(id+"F0.wireOp",EDGE,"E1519"),sQuery(id+"F0.wireOp",EDGE,"E1520"),sQuery(id+"F0.wireOp",EDGE,"E1521"),sQuery(id+"F0.wireOp",EDGE,"E1522"),sQuery(id+"F0.wireOp",EDGE,"E1523"),sQuery(id+"F0.wireOp",EDGE,"E1524"),sQuery(id+"F0.wireOp",EDGE,"E1525"),sQuery(id+"F0.wireOp",EDGE,"E1526"),sQuery(id+"F0.wireOp",EDGE,"E1527"),sQuery(id+"F0.wireOp",EDGE,"E1528"),sQuery(id+"F0.wireOp",EDGE,"E1529"),sQuery(id+"F0.wireOp",EDGE,"E1530"),sQuery(id+"F0.wireOp",EDGE,"E1531"),sQuery(id+"F0.wireOp",EDGE,"E1532"),sQuery(id+"F0.wireOp",EDGE,"E1533"),sQuery(id+"F0.wireOp",EDGE,"E1534"),sQuery(id+"F0.wireOp",EDGE,"E1535"),sQuery(id+"F0.wireOp",EDGE,"E1536"),sQuery(id+"F0.wireOp",EDGE,"E1537"),sQuery(id+"F0.wireOp",EDGE,"E1538"),sQuery(id+"F0.wireOp",EDGE,"E1539"),sQuery(id+"F0.wireOp",EDGE,"E1540"),sQuery(id+"F0.wireOp",EDGE,"E1541"),sQuery(id+"F0.wireOp",EDGE,"E1542"),sQuery(id+"F0.wireOp",EDGE,"E1543"),sQuery(id+"F0.wireOp",EDGE,"E1544"),sQuery(id+"F0.wireOp",EDGE,"E1545"),sQuery(id+"F0.wireOp",EDGE,"E1546"),sQuery(id+"F0.wireOp",EDGE,"E1547"),sQuery(id+"F0.wireOp",EDGE,"E1548"),sQuery(id+"F0.wireOp",EDGE,"E1549"),sQuery(id+"F0.wireOp",EDGE,"E1550"),sQuery(id+"F0.wireOp",EDGE,"E1551"),sQuery(id+"F0.wireOp",EDGE,"E1552"),sQuery(id+"F0.wireOp",EDGE,"E1553"),sQuery(id+"F0.wireOp",EDGE,"E1554"),sQuery(id+"F0.wireOp",EDGE,"E1555"),sQuery(id+"F0.wireOp",EDGE,"E1556"),sQuery(id+"F0.wireOp",EDGE,"E1557"),sQuery(id+"F0.wireOp",EDGE,"E1558"),sQuery(id+"F0.wireOp",EDGE,"E1559"),sQuery(id+"F0.wireOp",EDGE,"E1560"),sQuery(id+"F0.wireOp",EDGE,"E1561"),sQuery(id+"F0.wireOp",EDGE,"E1562"),sQuery(id+"F0.wireOp",EDGE,"E1563"),sQuery(id+"F0.wireOp",EDGE,"E1564"),sQuery(id+"F0.wireOp",EDGE,"E1565"),sQuery(id+"F0.wireOp",EDGE,"E1566"),sQuery(id+"F0.wireOp",EDGE,"E1567"),sQuery(id+"F0.wireOp",EDGE,"E1568"),sQuery(id+"F0.wireOp",EDGE,"E1569"),sQuery(id+"F0.wireOp",EDGE,"E1570"),sQuery(id+"F0.wireOp",EDGE,"E1571"),sQuery(id+"F0.wireOp",EDGE,"E1572"),sQuery(id+"F0.wireOp",EDGE,"E1573"),sQuery(id+"F0.wireOp",EDGE,"E1574"),sQuery(id+"F0.wireOp",EDGE,"E1575"),sQuery(id+"F0.wireOp",EDGE,"E1576"),sQuery(id+"F0.wireOp",EDGE,"E1577"),sQuery(id+"F0.wireOp",EDGE,"E1578"),sQuery(id+"F0.wireOp",EDGE,"E1579"),sQuery(id+"F0.wireOp",EDGE,"E1580"),sQuery(id+"F0.wireOp",EDGE,"E1581"),sQuery(id+"F0.wireOp",EDGE,"E1582"),sQuery(id+"F0.wireOp",EDGE,"E1583"),sQuery(id+"F0.wireOp",EDGE,"E1584"),sQuery(id+"F0.wireOp",EDGE,"E1585"),sQuery(id+"F0.wireOp",EDGE,"E1586"),sQuery(id+"F0.wireOp",EDGE,"E1587"),sQuery(id+"F0.wireOp",EDGE,"E1588"),sQuery(id+"F0.wireOp",EDGE,"E1589"),sQuery(id+"F0.wireOp",EDGE,"E1590"),sQuery(id+"F0.wireOp",EDGE,"E1591"),sQuery(id+"F0.wireOp",EDGE,"E1592"),sQuery(id+"F0.wireOp",EDGE,"E1593"),sQuery(id+"F0.wireOp",EDGE,"E1594"),sQuery(id+"F0.wireOp",EDGE,"E1595"),sQuery(id+"F0.wireOp",EDGE,"E1596"),sQuery(id+"F0.wireOp",EDGE,"E1597"),sQuery(id+"F0.wireOp",EDGE,"E1598"),sQuery(id+"F0.wireOp",EDGE,"E1599"),sQuery(id+"F0.wireOp",EDGE,"E1600"),sQuery(id+"F0.wireOp",EDGE,"E1601"),sQuery(id+"F0.wireOp",EDGE,"E1602"),sQuery(id+"F0.wireOp",EDGE,"E1603"),sQuery(id+"F0.wireOp",EDGE,"E1604"),sQuery(id+"F0.wireOp",EDGE,"E1605"),sQuery(id+"F0.wireOp",EDGE,"E1606"),sQuery(id+"F0.wireOp",EDGE,"E1607"),sQuery(id+"F0.wireOp",EDGE,"E1608"),sQuery(id+"F0.wireOp",EDGE,"E1609"),sQuery(id+"F0.wireOp",EDGE,"E1610"),sQuery(id+"F0.wireOp",EDGE,"E1611"),sQuery(id+"F0.wireOp",EDGE,"E1612"),sQuery(id+"F0.wireOp",EDGE,"E1613"),sQuery(id+"F0.wireOp",EDGE,"E1614"),sQuery(id+"F0.wireOp",EDGE,"E1615"),sQuery(id+"F0.wireOp",EDGE,"E1616"),sQuery(id+"F0.wireOp",EDGE,"E1617"),sQuery(id+"F0.wireOp",EDGE,"E1618"),sQuery(id+"F0.wireOp",EDGE,"E1619"),sQuery(id+"F0.wireOp",EDGE,"E1620"),sQuery(id+"F0.wireOp",EDGE,"E1621"),sQuery(id+"F0.wireOp",EDGE,"E1622"),sQuery(id+"F0.wireOp",EDGE,"E1623"),sQuery(id+"F0.wireOp",EDGE,"E1624"),sQuery(id+"F0.wireOp",EDGE,"E1625"),sQuery(id+"F0.wireOp",EDGE,"E1626"),sQuery(id+"F0.wireOp",EDGE,"E1627"),sQuery(id+"F0.wireOp",EDGE,"E1628"),sQuery(id+"F0.wireOp",EDGE,"E1629"),sQuery(id+"F0.wireOp",EDGE,"E1630"),sQuery(id+"F0.wireOp",EDGE,"E1631"),sQuery(id+"F0.wireOp",EDGE,"E1632"),sQuery(id+"F0.wireOp",EDGE,"E1633"),sQuery(id+"F0.wireOp",EDGE,"E1634"),sQuery(id+"F0.wireOp",EDGE,"E1635"),sQuery(id+"F0.wireOp",EDGE,"E1636"),sQuery(id+"F0.wireOp",EDGE,"E1637"),sQuery(id+"F0.wireOp",EDGE,"E1640")])],"isStart":true});
            var sketch = newSketch(context, id + "F2", { "sketchPlane" : qUnion([Q0])});
            skCircle(sketch, "E1641.0", {"center": v(3.15, 0) * mm, "radius": 5.05 * mm});
            skLineSegment(sketch, "E1642", {"start": v(3.15, 0) * mm, "end": v(3.15, 7.45) * mm});
            skCircle(sketch, "E1643", {"center": v(3.15, 7.45) * mm, "radius": 1.05 * mm});
            skSolve(sketch);
        }
        {
            var Q0;
            Q0=makeQuery(id+"F2.imprint","IMPRINT",FACE,{"disambiguationData":[TD([[makeQuery(id+"F2.imprint","IMPRINT",EDGE,{"derivedFrom":sQuery(id+"F2.wireOp",EDGE,"E1643")}),1.0]])]});
            var Q1;
            Q1=makeQuery(id+"F1.opExtrude","CAP_FACE",FACE,{"disambiguationData":[OSD([sQuery(id+"F0.wireOp",EDGE,"E574"),sQuery(id+"F0.wireOp",EDGE,"E575"),sQuery(id+"F0.wireOp",EDGE,"E576"),sQuery(id+"F0.wireOp",EDGE,"E577"),sQuery(id+"F0.wireOp",EDGE,"E578"),sQuery(id+"F0.wireOp",EDGE,"E579"),sQuery(id+"F0.wireOp",EDGE,"E580"),sQuery(id+"F0.wireOp",EDGE,"E581"),sQuery(id+"F0.wireOp",EDGE,"E582"),sQuery(id+"F0.wireOp",EDGE,"E583"),sQuery(id+"F0.wireOp",EDGE,"E584"),sQuery(id+"F0.wireOp",EDGE,"E585"),sQuery(id+"F0.wireOp",EDGE,"E586"),sQuery(id+"F0.wireOp",EDGE,"E587"),sQuery(id+"F0.wireOp",EDGE,"E588"),sQuery(id+"F0.wireOp",EDGE,"E589"),sQuery(id+"F0.wireOp",EDGE,"E590"),sQuery(id+"F0.wireOp",EDGE,"E591"),sQuery(id+"F0.wireOp",EDGE,"E592"),sQuery(id+"F0.wireOp",EDGE,"E593"),sQuery(id+"F0.wireOp",EDGE,"E594"),sQuery(id+"F0.wireOp",EDGE,"E595"),sQuery(id+"F0.wireOp",EDGE,"E596"),sQuery(id+"F0.wireOp",EDGE,"E597"),sQuery(id+"F0.wireOp",EDGE,"E598"),sQuery(id+"F0.wireOp",EDGE,"E599"),sQuery(id+"F0.wireOp",EDGE,"E600"),sQuery(id+"F0.wireOp",EDGE,"E601"),sQuery(id+"F0.wireOp",EDGE,"E602"),sQuery(id+"F0.wireOp",EDGE,"E603"),sQuery(id+"F0.wireOp",EDGE,"E604"),sQuery(id+"F0.wireOp",EDGE,"E605"),sQuery(id+"F0.wireOp",EDGE,"E606"),sQuery(id+"F0.wireOp",EDGE,"E607"),sQuery(id+"F0.wireOp",EDGE,"E608"),sQuery(id+"F0.wireOp",EDGE,"E609"),sQuery(id+"F0.wireOp",EDGE,"E610"),sQuery(id+"F0.wireOp",EDGE,"E611"),sQuery(id+"F0.wireOp",EDGE,"E612"),sQuery(id+"F0.wireOp",EDGE,"E613"),sQuery(id+"F0.wireOp",EDGE,"E614"),sQuery(id+"F0.wireOp",EDGE,"E615"),sQuery(id+"F0.wireOp",EDGE,"E616"),sQuery(id+"F0.wireOp",EDGE,"E617"),sQuery(id+"F0.wireOp",EDGE,"E618"),sQuery(id+"F0.wireOp",EDGE,"E619"),sQuery(id+"F0.wireOp",EDGE,"E620"),sQuery(id+"F0.wireOp",EDGE,"E621"),sQuery(id+"F0.wireOp",EDGE,"E622"),sQuery(id+"F0.wireOp",EDGE,"E623"),sQuery(id+"F0.wireOp",EDGE,"E624"),sQuery(id+"F0.wireOp",EDGE,"E625"),sQuery(id+"F0.wireOp",EDGE,"E626"),sQuery(id+"F0.wireOp",EDGE,"E627"),sQuery(id+"F0.wireOp",EDGE,"E628"),sQuery(id+"F0.wireOp",EDGE,"E629"),sQuery(id+"F0.wireOp",EDGE,"E630"),sQuery(id+"F0.wireOp",EDGE,"E631"),sQuery(id+"F0.wireOp",EDGE,"E632"),sQuery(id+"F0.wireOp",EDGE,"E633"),sQuery(id+"F0.wireOp",EDGE,"E634"),sQuery(id+"F0.wireOp",EDGE,"E635"),sQuery(id+"F0.wireOp",EDGE,"E636"),sQuery(id+"F0.wireOp",EDGE,"E637"),sQuery(id+"F0.wireOp",EDGE,"E638"),sQuery(id+"F0.wireOp",EDGE,"E639"),sQuery(id+"F0.wireOp",EDGE,"E640"),sQuery(id+"F0.wireOp",EDGE,"E641"),sQuery(id+"F0.wireOp",EDGE,"E642"),sQuery(id+"F0.wireOp",EDGE,"E643"),sQuery(id+"F0.wireOp",EDGE,"E644"),sQuery(id+"F0.wireOp",EDGE,"E645"),sQuery(id+"F0.wireOp",EDGE,"E646"),sQuery(id+"F0.wireOp",EDGE,"E647"),sQuery(id+"F0.wireOp",EDGE,"E648"),sQuery(id+"F0.wireOp",EDGE,"E649"),sQuery(id+"F0.wireOp",EDGE,"E650"),sQuery(id+"F0.wireOp",EDGE,"E651"),sQuery(id+"F0.wireOp",EDGE,"E652"),sQuery(id+"F0.wireOp",EDGE,"E653"),sQuery(id+"F0.wireOp",EDGE,"E654"),sQuery(id+"F0.wireOp",EDGE,"E655"),sQuery(id+"F0.wireOp",EDGE,"E656"),sQuery(id+"F0.wireOp",EDGE,"E657"),sQuery(id+"F0.wireOp",EDGE,"E658"),sQuery(id+"F0.wireOp",EDGE,"E659"),sQuery(id+"F0.wireOp",EDGE,"E660"),sQuery(id+"F0.wireOp",EDGE,"E661"),sQuery(id+"F0.wireOp",EDGE,"E662"),sQuery(id+"F0.wireOp",EDGE,"E663"),sQuery(id+"F0.wireOp",EDGE,"E664"),sQuery(id+"F0.wireOp",EDGE,"E665"),sQuery(id+"F0.wireOp",EDGE,"E666"),sQuery(id+"F0.wireOp",EDGE,"E667"),sQuery(id+"F0.wireOp",EDGE,"E668"),sQuery(id+"F0.wireOp",EDGE,"E669"),sQuery(id+"F0.wireOp",EDGE,"E670"),sQuery(id+"F0.wireOp",EDGE,"E671"),sQuery(id+"F0.wireOp",EDGE,"E672"),sQuery(id+"F0.wireOp",EDGE,"E673"),sQuery(id+"F0.wireOp",EDGE,"E674"),sQuery(id+"F0.wireOp",EDGE,"E675"),sQuery(id+"F0.wireOp",EDGE,"E676"),sQuery(id+"F0.wireOp",EDGE,"E677"),sQuery(id+"F0.wireOp",EDGE,"E678"),sQuery(id+"F0.wireOp",EDGE,"E679"),sQuery(id+"F0.wireOp",EDGE,"E680"),sQuery(id+"F0.wireOp",EDGE,"E681"),sQuery(id+"F0.wireOp",EDGE,"E682"),sQuery(id+"F0.wireOp",EDGE,"E683"),sQuery(id+"F0.wireOp",EDGE,"E684"),sQuery(id+"F0.wireOp",EDGE,"E685"),sQuery(id+"F0.wireOp",EDGE,"E686"),sQuery(id+"F0.wireOp",EDGE,"E687"),sQuery(id+"F0.wireOp",EDGE,"E688"),sQuery(id+"F0.wireOp",EDGE,"E689"),sQuery(id+"F0.wireOp",EDGE,"E690"),sQuery(id+"F0.wireOp",EDGE,"E691"),sQuery(id+"F0.wireOp",EDGE,"E692"),sQuery(id+"F0.wireOp",EDGE,"E693"),sQuery(id+"F0.wireOp",EDGE,"E694"),sQuery(id+"F0.wireOp",EDGE,"E695"),sQuery(id+"F0.wireOp",EDGE,"E696"),sQuery(id+"F0.wireOp",EDGE,"E697"),sQuery(id+"F0.wireOp",EDGE,"E698"),sQuery(id+"F0.wireOp",EDGE,"E699"),sQuery(id+"F0.wireOp",EDGE,"E700"),sQuery(id+"F0.wireOp",EDGE,"E701"),sQuery(id+"F0.wireOp",EDGE,"E702"),sQuery(id+"F0.wireOp",EDGE,"E703"),sQuery(id+"F0.wireOp",EDGE,"E704"),sQuery(id+"F0.wireOp",EDGE,"E705"),sQuery(id+"F0.wireOp",EDGE,"E706"),sQuery(id+"F0.wireOp",EDGE,"E707"),sQuery(id+"F0.wireOp",EDGE,"E708"),sQuery(id+"F0.wireOp",EDGE,"E709"),sQuery(id+"F0.wireOp",EDGE,"E710"),sQuery(id+"F0.wireOp",EDGE,"E711"),sQuery(id+"F0.wireOp",EDGE,"E712"),sQuery(id+"F0.wireOp",EDGE,"E713"),sQuery(id+"F0.wireOp",EDGE,"E714"),sQuery(id+"F0.wireOp",EDGE,"E715"),sQuery(id+"F0.wireOp",EDGE,"E716"),sQuery(id+"F0.wireOp",EDGE,"E717"),sQuery(id+"F0.wireOp",EDGE,"E718"),sQuery(id+"F0.wireOp",EDGE,"E719"),sQuery(id+"F0.wireOp",EDGE,"E720"),sQuery(id+"F0.wireOp",EDGE,"E721"),sQuery(id+"F0.wireOp",EDGE,"E722"),sQuery(id+"F0.wireOp",EDGE,"E723"),sQuery(id+"F0.wireOp",EDGE,"E724"),sQuery(id+"F0.wireOp",EDGE,"E725"),sQuery(id+"F0.wireOp",EDGE,"E726"),sQuery(id+"F0.wireOp",EDGE,"E727"),sQuery(id+"F0.wireOp",EDGE,"E728"),sQuery(id+"F0.wireOp",EDGE,"E729"),sQuery(id+"F0.wireOp",EDGE,"E730"),sQuery(id+"F0.wireOp",EDGE,"E731"),sQuery(id+"F0.wireOp",EDGE,"E732"),sQuery(id+"F0.wireOp",EDGE,"E733"),sQuery(id+"F0.wireOp",EDGE,"E734"),sQuery(id+"F0.wireOp",EDGE,"E735"),sQuery(id+"F0.wireOp",EDGE,"E736"),sQuery(id+"F0.wireOp",EDGE,"E737"),sQuery(id+"F0.wireOp",EDGE,"E738"),sQuery(id+"F0.wireOp",EDGE,"E739"),sQuery(id+"F0.wireOp",EDGE,"E740"),sQuery(id+"F0.wireOp",EDGE,"E741"),sQuery(id+"F0.wireOp",EDGE,"E742"),sQuery(id+"F0.wireOp",EDGE,"E743"),sQuery(id+"F0.wireOp",EDGE,"E744"),sQuery(id+"F0.wireOp",EDGE,"E745"),sQuery(id+"F0.wireOp",EDGE,"E746"),sQuery(id+"F0.wireOp",EDGE,"E747"),sQuery(id+"F0.wireOp",EDGE,"E748"),sQuery(id+"F0.wireOp",EDGE,"E749"),sQuery(id+"F0.wireOp",EDGE,"E750"),sQuery(id+"F0.wireOp",EDGE,"E751"),sQuery(id+"F0.wireOp",EDGE,"E752"),sQuery(id+"F0.wireOp",EDGE,"E753"),sQuery(id+"F0.wireOp",EDGE,"E754"),sQuery(id+"F0.wireOp",EDGE,"E755"),sQuery(id+"F0.wireOp",EDGE,"E756"),sQuery(id+"F0.wireOp",EDGE,"E757"),sQuery(id+"F0.wireOp",EDGE,"E758"),sQuery(id+"F0.wireOp",EDGE,"E759"),sQuery(id+"F0.wireOp",EDGE,"E760"),sQuery(id+"F0.wireOp",EDGE,"E761"),sQuery(id+"F0.wireOp",EDGE,"E762"),sQuery(id+"F0.wireOp",EDGE,"E763"),sQuery(id+"F0.wireOp",EDGE,"E764"),sQuery(id+"F0.wireOp",EDGE,"E765"),sQuery(id+"F0.wireOp",EDGE,"E766"),sQuery(id+"F0.wireOp",EDGE,"E767"),sQuery(id+"F0.wireOp",EDGE,"E768"),sQuery(id+"F0.wireOp",EDGE,"E769"),sQuery(id+"F0.wireOp",EDGE,"E770"),sQuery(id+"F0.wireOp",EDGE,"E771"),sQuery(id+"F0.wireOp",EDGE,"E772"),sQuery(id+"F0.wireOp",EDGE,"E773"),sQuery(id+"F0.wireOp",EDGE,"E774"),sQuery(id+"F0.wireOp",EDGE,"E775"),sQuery(id+"F0.wireOp",EDGE,"E776"),sQuery(id+"F0.wireOp",EDGE,"E777"),sQuery(id+"F0.wireOp",EDGE,"E778"),sQuery(id+"F0.wireOp",EDGE,"E779"),sQuery(id+"F0.wireOp",EDGE,"E780"),sQuery(id+"F0.wireOp",EDGE,"E781"),sQuery(id+"F0.wireOp",EDGE,"E782"),sQuery(id+"F0.wireOp",EDGE,"E783"),sQuery(id+"F0.wireOp",EDGE,"E784"),sQuery(id+"F0.wireOp",EDGE,"E785"),sQuery(id+"F0.wireOp",EDGE,"E786"),sQuery(id+"F0.wireOp",EDGE,"E787"),sQuery(id+"F0.wireOp",EDGE,"E788"),sQuery(id+"F0.wireOp",EDGE,"E789"),sQuery(id+"F0.wireOp",EDGE,"E790"),sQuery(id+"F0.wireOp",EDGE,"E791"),sQuery(id+"F0.wireOp",EDGE,"E792"),sQuery(id+"F0.wireOp",EDGE,"E793"),sQuery(id+"F0.wireOp",EDGE,"E794"),sQuery(id+"F0.wireOp",EDGE,"E795"),sQuery(id+"F0.wireOp",EDGE,"E796"),sQuery(id+"F0.wireOp",EDGE,"E797"),sQuery(id+"F0.wireOp",EDGE,"E798"),sQuery(id+"F0.wireOp",EDGE,"E799"),sQuery(id+"F0.wireOp",EDGE,"E800"),sQuery(id+"F0.wireOp",EDGE,"E801"),sQuery(id+"F0.wireOp",EDGE,"E802"),sQuery(id+"F0.wireOp",EDGE,"E803"),sQuery(id+"F0.wireOp",EDGE,"E804"),sQuery(id+"F0.wireOp",EDGE,"E805"),sQuery(id+"F0.wireOp",EDGE,"E806"),sQuery(id+"F0.wireOp",EDGE,"E807"),sQuery(id+"F0.wireOp",EDGE,"E808"),sQuery(id+"F0.wireOp",EDGE,"E809"),sQuery(id+"F0.wireOp",EDGE,"E810"),sQuery(id+"F0.wireOp",EDGE,"E811"),sQuery(id+"F0.wireOp",EDGE,"E812"),sQuery(id+"F0.wireOp",EDGE,"E813"),sQuery(id+"F0.wireOp",EDGE,"E814"),sQuery(id+"F0.wireOp",EDGE,"E815"),sQuery(id+"F0.wireOp",EDGE,"E816"),sQuery(id+"F0.wireOp",EDGE,"E817"),sQuery(id+"F0.wireOp",EDGE,"E818"),sQuery(id+"F0.wireOp",EDGE,"E819"),sQuery(id+"F0.wireOp",EDGE,"E820"),sQuery(id+"F0.wireOp",EDGE,"E821"),sQuery(id+"F0.wireOp",EDGE,"E822"),sQuery(id+"F0.wireOp",EDGE,"E823"),sQuery(id+"F0.wireOp",EDGE,"E824"),sQuery(id+"F0.wireOp",EDGE,"E825"),sQuery(id+"F0.wireOp",EDGE,"E826"),sQuery(id+"F0.wireOp",EDGE,"E827"),sQuery(id+"F0.wireOp",EDGE,"E828"),sQuery(id+"F0.wireOp",EDGE,"E829"),sQuery(id+"F0.wireOp",EDGE,"E830"),sQuery(id+"F0.wireOp",EDGE,"E831"),sQuery(id+"F0.wireOp",EDGE,"E832"),sQuery(id+"F0.wireOp",EDGE,"E833"),sQuery(id+"F0.wireOp",EDGE,"E834"),sQuery(id+"F0.wireOp",EDGE,"E835"),sQuery(id+"F0.wireOp",EDGE,"E836"),sQuery(id+"F0.wireOp",EDGE,"E837"),sQuery(id+"F0.wireOp",EDGE,"E838"),sQuery(id+"F0.wireOp",EDGE,"E839"),sQuery(id+"F0.wireOp",EDGE,"E840"),sQuery(id+"F0.wireOp",EDGE,"E841"),sQuery(id+"F0.wireOp",EDGE,"E842"),sQuery(id+"F0.wireOp",EDGE,"E843"),sQuery(id+"F0.wireOp",EDGE,"E844"),sQuery(id+"F0.wireOp",EDGE,"E845"),sQuery(id+"F0.wireOp",EDGE,"E846"),sQuery(id+"F0.wireOp",EDGE,"E847"),sQuery(id+"F0.wireOp",EDGE,"E848"),sQuery(id+"F0.wireOp",EDGE,"E849"),sQuery(id+"F0.wireOp",EDGE,"E850"),sQuery(id+"F0.wireOp",EDGE,"E851"),sQuery(id+"F0.wireOp",EDGE,"E852"),sQuery(id+"F0.wireOp",EDGE,"E853"),sQuery(id+"F0.wireOp",EDGE,"E854"),sQuery(id+"F0.wireOp",EDGE,"E855"),sQuery(id+"F0.wireOp",EDGE,"E856"),sQuery(id+"F0.wireOp",EDGE,"E857"),sQuery(id+"F0.wireOp",EDGE,"E858"),sQuery(id+"F0.wireOp",EDGE,"E859"),sQuery(id+"F0.wireOp",EDGE,"E860"),sQuery(id+"F0.wireOp",EDGE,"E861"),sQuery(id+"F0.wireOp",EDGE,"E862"),sQuery(id+"F0.wireOp",EDGE,"E863"),sQuery(id+"F0.wireOp",EDGE,"E864"),sQuery(id+"F0.wireOp",EDGE,"E865"),sQuery(id+"F0.wireOp",EDGE,"E866"),sQuery(id+"F0.wireOp",EDGE,"E867"),sQuery(id+"F0.wireOp",EDGE,"E868"),sQuery(id+"F0.wireOp",EDGE,"E869"),sQuery(id+"F0.wireOp",EDGE,"E870"),sQuery(id+"F0.wireOp",EDGE,"E871"),sQuery(id+"F0.wireOp",EDGE,"E872"),sQuery(id+"F0.wireOp",EDGE,"E873"),sQuery(id+"F0.wireOp",EDGE,"E874"),sQuery(id+"F0.wireOp",EDGE,"E875"),sQuery(id+"F0.wireOp",EDGE,"E876"),sQuery(id+"F0.wireOp",EDGE,"E877"),sQuery(id+"F0.wireOp",EDGE,"E878"),sQuery(id+"F0.wireOp",EDGE,"E879"),sQuery(id+"F0.wireOp",EDGE,"E880"),sQuery(id+"F0.wireOp",EDGE,"E881"),sQuery(id+"F0.wireOp",EDGE,"E882"),sQuery(id+"F0.wireOp",EDGE,"E883"),sQuery(id+"F0.wireOp",EDGE,"E884"),sQuery(id+"F0.wireOp",EDGE,"E885"),sQuery(id+"F0.wireOp",EDGE,"E886"),sQuery(id+"F0.wireOp",EDGE,"E887"),sQuery(id+"F0.wireOp",EDGE,"E888"),sQuery(id+"F0.wireOp",EDGE,"E889"),sQuery(id+"F0.wireOp",EDGE,"E890"),sQuery(id+"F0.wireOp",EDGE,"E891"),sQuery(id+"F0.wireOp",EDGE,"E892"),sQuery(id+"F0.wireOp",EDGE,"E893"),sQuery(id+"F0.wireOp",EDGE,"E894"),sQuery(id+"F0.wireOp",EDGE,"E895"),sQuery(id+"F0.wireOp",EDGE,"E896"),sQuery(id+"F0.wireOp",EDGE,"E897"),sQuery(id+"F0.wireOp",EDGE,"E898"),sQuery(id+"F0.wireOp",EDGE,"E899"),sQuery(id+"F0.wireOp",EDGE,"E900"),sQuery(id+"F0.wireOp",EDGE,"E901"),sQuery(id+"F0.wireOp",EDGE,"E902"),sQuery(id+"F0.wireOp",EDGE,"E903"),sQuery(id+"F0.wireOp",EDGE,"E904"),sQuery(id+"F0.wireOp",EDGE,"E905"),sQuery(id+"F0.wireOp",EDGE,"E906"),sQuery(id+"F0.wireOp",EDGE,"E907"),sQuery(id+"F0.wireOp",EDGE,"E908"),sQuery(id+"F0.wireOp",EDGE,"E909"),sQuery(id+"F0.wireOp",EDGE,"E910"),sQuery(id+"F0.wireOp",EDGE,"E911"),sQuery(id+"F0.wireOp",EDGE,"E912"),sQuery(id+"F0.wireOp",EDGE,"E913"),sQuery(id+"F0.wireOp",EDGE,"E914"),sQuery(id+"F0.wireOp",EDGE,"E915"),sQuery(id+"F0.wireOp",EDGE,"E916"),sQuery(id+"F0.wireOp",EDGE,"E917"),sQuery(id+"F0.wireOp",EDGE,"E918"),sQuery(id+"F0.wireOp",EDGE,"E919"),sQuery(id+"F0.wireOp",EDGE,"E920"),sQuery(id+"F0.wireOp",EDGE,"E921"),sQuery(id+"F0.wireOp",EDGE,"E922"),sQuery(id+"F0.wireOp",EDGE,"E923"),sQuery(id+"F0.wireOp",EDGE,"E924"),sQuery(id+"F0.wireOp",EDGE,"E925"),sQuery(id+"F0.wireOp",EDGE,"E926"),sQuery(id+"F0.wireOp",EDGE,"E927"),sQuery(id+"F0.wireOp",EDGE,"E928"),sQuery(id+"F0.wireOp",EDGE,"E929"),sQuery(id+"F0.wireOp",EDGE,"E930"),sQuery(id+"F0.wireOp",EDGE,"E931"),sQuery(id+"F0.wireOp",EDGE,"E932"),sQuery(id+"F0.wireOp",EDGE,"E933"),sQuery(id+"F0.wireOp",EDGE,"E934"),sQuery(id+"F0.wireOp",EDGE,"E935"),sQuery(id+"F0.wireOp",EDGE,"E936"),sQuery(id+"F0.wireOp",EDGE,"E937"),sQuery(id+"F0.wireOp",EDGE,"E938"),sQuery(id+"F0.wireOp",EDGE,"E939"),sQuery(id+"F0.wireOp",EDGE,"E940"),sQuery(id+"F0.wireOp",EDGE,"E941"),sQuery(id+"F0.wireOp",EDGE,"E942"),sQuery(id+"F0.wireOp",EDGE,"E943"),sQuery(id+"F0.wireOp",EDGE,"E944"),sQuery(id+"F0.wireOp",EDGE,"E945"),sQuery(id+"F0.wireOp",EDGE,"E946"),sQuery(id+"F0.wireOp",EDGE,"E947"),sQuery(id+"F0.wireOp",EDGE,"E948"),sQuery(id+"F0.wireOp",EDGE,"E949"),sQuery(id+"F0.wireOp",EDGE,"E950"),sQuery(id+"F0.wireOp",EDGE,"E951"),sQuery(id+"F0.wireOp",EDGE,"E952"),sQuery(id+"F0.wireOp",EDGE,"E953"),sQuery(id+"F0.wireOp",EDGE,"E954"),sQuery(id+"F0.wireOp",EDGE,"E955"),sQuery(id+"F0.wireOp",EDGE,"E956"),sQuery(id+"F0.wireOp",EDGE,"E957"),sQuery(id+"F0.wireOp",EDGE,"E958"),sQuery(id+"F0.wireOp",EDGE,"E959"),sQuery(id+"F0.wireOp",EDGE,"E960"),sQuery(id+"F0.wireOp",EDGE,"E961"),sQuery(id+"F0.wireOp",EDGE,"E962"),sQuery(id+"F0.wireOp",EDGE,"E963"),sQuery(id+"F0.wireOp",EDGE,"E964"),sQuery(id+"F0.wireOp",EDGE,"E965"),sQuery(id+"F0.wireOp",EDGE,"E966"),sQuery(id+"F0.wireOp",EDGE,"E967"),sQuery(id+"F0.wireOp",EDGE,"E968"),sQuery(id+"F0.wireOp",EDGE,"E969"),sQuery(id+"F0.wireOp",EDGE,"E970"),sQuery(id+"F0.wireOp",EDGE,"E971"),sQuery(id+"F0.wireOp",EDGE,"E972"),sQuery(id+"F0.wireOp",EDGE,"E973"),sQuery(id+"F0.wireOp",EDGE,"E974"),sQuery(id+"F0.wireOp",EDGE,"E975"),sQuery(id+"F0.wireOp",EDGE,"E976"),sQuery(id+"F0.wireOp",EDGE,"E977"),sQuery(id+"F0.wireOp",EDGE,"E978"),sQuery(id+"F0.wireOp",EDGE,"E979"),sQuery(id+"F0.wireOp",EDGE,"E980"),sQuery(id+"F0.wireOp",EDGE,"E981"),sQuery(id+"F0.wireOp",EDGE,"E982"),sQuery(id+"F0.wireOp",EDGE,"E983"),sQuery(id+"F0.wireOp",EDGE,"E984"),sQuery(id+"F0.wireOp",EDGE,"E985"),sQuery(id+"F0.wireOp",EDGE,"E986"),sQuery(id+"F0.wireOp",EDGE,"E987"),sQuery(id+"F0.wireOp",EDGE,"E988"),sQuery(id+"F0.wireOp",EDGE,"E989"),sQuery(id+"F0.wireOp",EDGE,"E990"),sQuery(id+"F0.wireOp",EDGE,"E991"),sQuery(id+"F0.wireOp",EDGE,"E992"),sQuery(id+"F0.wireOp",EDGE,"E993"),sQuery(id+"F0.wireOp",EDGE,"E994"),sQuery(id+"F0.wireOp",EDGE,"E995"),sQuery(id+"F0.wireOp",EDGE,"E996"),sQuery(id+"F0.wireOp",EDGE,"E997"),sQuery(id+"F0.wireOp",EDGE,"E998"),sQuery(id+"F0.wireOp",EDGE,"E999"),sQuery(id+"F0.wireOp",EDGE,"E1000"),sQuery(id+"F0.wireOp",EDGE,"E1001"),sQuery(id+"F0.wireOp",EDGE,"E1002"),sQuery(id+"F0.wireOp",EDGE,"E1003"),sQuery(id+"F0.wireOp",EDGE,"E1004"),sQuery(id+"F0.wireOp",EDGE,"E1005"),sQuery(id+"F0.wireOp",EDGE,"E1006"),sQuery(id+"F0.wireOp",EDGE,"E1007"),sQuery(id+"F0.wireOp",EDGE,"E1008"),sQuery(id+"F0.wireOp",EDGE,"E1009"),sQuery(id+"F0.wireOp",EDGE,"E1010"),sQuery(id+"F0.wireOp",EDGE,"E1011"),sQuery(id+"F0.wireOp",EDGE,"E1012"),sQuery(id+"F0.wireOp",EDGE,"E1013"),sQuery(id+"F0.wireOp",EDGE,"E1014"),sQuery(id+"F0.wireOp",EDGE,"E1015"),sQuery(id+"F0.wireOp",EDGE,"E1016"),sQuery(id+"F0.wireOp",EDGE,"E1017"),sQuery(id+"F0.wireOp",EDGE,"E1018"),sQuery(id+"F0.wireOp",EDGE,"E1019"),sQuery(id+"F0.wireOp",EDGE,"E1020"),sQuery(id+"F0.wireOp",EDGE,"E1021"),sQuery(id+"F0.wireOp",EDGE,"E1022"),sQuery(id+"F0.wireOp",EDGE,"E1023"),sQuery(id+"F0.wireOp",EDGE,"E1024"),sQuery(id+"F0.wireOp",EDGE,"E1025"),sQuery(id+"F0.wireOp",EDGE,"E1026"),sQuery(id+"F0.wireOp",EDGE,"E1027"),sQuery(id+"F0.wireOp",EDGE,"E1028"),sQuery(id+"F0.wireOp",EDGE,"E1029"),sQuery(id+"F0.wireOp",EDGE,"E1030"),sQuery(id+"F0.wireOp",EDGE,"E1031"),sQuery(id+"F0.wireOp",EDGE,"E1032"),sQuery(id+"F0.wireOp",EDGE,"E1033"),sQuery(id+"F0.wireOp",EDGE,"E1034"),sQuery(id+"F0.wireOp",EDGE,"E1035"),sQuery(id+"F0.wireOp",EDGE,"E1036"),sQuery(id+"F0.wireOp",EDGE,"E1037"),sQuery(id+"F0.wireOp",EDGE,"E1038"),sQuery(id+"F0.wireOp",EDGE,"E1039"),sQuery(id+"F0.wireOp",EDGE,"E1040"),sQuery(id+"F0.wireOp",EDGE,"E1041"),sQuery(id+"F0.wireOp",EDGE,"E1042"),sQuery(id+"F0.wireOp",EDGE,"E1043"),sQuery(id+"F0.wireOp",EDGE,"E1044"),sQuery(id+"F0.wireOp",EDGE,"E1045"),sQuery(id+"F0.wireOp",EDGE,"E1046"),sQuery(id+"F0.wireOp",EDGE,"E1047"),sQuery(id+"F0.wireOp",EDGE,"E1048"),sQuery(id+"F0.wireOp",EDGE,"E1049"),sQuery(id+"F0.wireOp",EDGE,"E1050"),sQuery(id+"F0.wireOp",EDGE,"E1051"),sQuery(id+"F0.wireOp",EDGE,"E1052"),sQuery(id+"F0.wireOp",EDGE,"E1053"),sQuery(id+"F0.wireOp",EDGE,"E1054"),sQuery(id+"F0.wireOp",EDGE,"E1055"),sQuery(id+"F0.wireOp",EDGE,"E1056"),sQuery(id+"F0.wireOp",EDGE,"E1057"),sQuery(id+"F0.wireOp",EDGE,"E1058"),sQuery(id+"F0.wireOp",EDGE,"E1059"),sQuery(id+"F0.wireOp",EDGE,"E1060"),sQuery(id+"F0.wireOp",EDGE,"E1061"),sQuery(id+"F0.wireOp",EDGE,"E1062"),sQuery(id+"F0.wireOp",EDGE,"E1063"),sQuery(id+"F0.wireOp",EDGE,"E1064"),sQuery(id+"F0.wireOp",EDGE,"E1065"),sQuery(id+"F0.wireOp",EDGE,"E1066"),sQuery(id+"F0.wireOp",EDGE,"E1067"),sQuery(id+"F0.wireOp",EDGE,"E1068"),sQuery(id+"F0.wireOp",EDGE,"E1069"),sQuery(id+"F0.wireOp",EDGE,"E1070"),sQuery(id+"F0.wireOp",EDGE,"E1071"),sQuery(id+"F0.wireOp",EDGE,"E1072"),sQuery(id+"F0.wireOp",EDGE,"E1073"),sQuery(id+"F0.wireOp",EDGE,"E1074"),sQuery(id+"F0.wireOp",EDGE,"E1075"),sQuery(id+"F0.wireOp",EDGE,"E1076"),sQuery(id+"F0.wireOp",EDGE,"E1077"),sQuery(id+"F0.wireOp",EDGE,"E1078"),sQuery(id+"F0.wireOp",EDGE,"E1079"),sQuery(id+"F0.wireOp",EDGE,"E1080"),sQuery(id+"F0.wireOp",EDGE,"E1081"),sQuery(id+"F0.wireOp",EDGE,"E1082"),sQuery(id+"F0.wireOp",EDGE,"E1083"),sQuery(id+"F0.wireOp",EDGE,"E1084"),sQuery(id+"F0.wireOp",EDGE,"E1085"),sQuery(id+"F0.wireOp",EDGE,"E1086"),sQuery(id+"F0.wireOp",EDGE,"E1087"),sQuery(id+"F0.wireOp",EDGE,"E1088"),sQuery(id+"F0.wireOp",EDGE,"E1089"),sQuery(id+"F0.wireOp",EDGE,"E1090"),sQuery(id+"F0.wireOp",EDGE,"E1091"),sQuery(id+"F0.wireOp",EDGE,"E1092"),sQuery(id+"F0.wireOp",EDGE,"E1093"),sQuery(id+"F0.wireOp",EDGE,"E1094"),sQuery(id+"F0.wireOp",EDGE,"E1095"),sQuery(id+"F0.wireOp",EDGE,"E1096"),sQuery(id+"F0.wireOp",EDGE,"E1097"),sQuery(id+"F0.wireOp",EDGE,"E1098"),sQuery(id+"F0.wireOp",EDGE,"E1099"),sQuery(id+"F0.wireOp",EDGE,"E1100"),sQuery(id+"F0.wireOp",EDGE,"E1101"),sQuery(id+"F0.wireOp",EDGE,"E1102"),sQuery(id+"F0.wireOp",EDGE,"E1103"),sQuery(id+"F0.wireOp",EDGE,"E1104"),sQuery(id+"F0.wireOp",EDGE,"E1105"),sQuery(id+"F0.wireOp",EDGE,"E1106"),sQuery(id+"F0.wireOp",EDGE,"E1107"),sQuery(id+"F0.wireOp",EDGE,"E1108"),sQuery(id+"F0.wireOp",EDGE,"E1109"),sQuery(id+"F0.wireOp",EDGE,"E1110"),sQuery(id+"F0.wireOp",EDGE,"E1111"),sQuery(id+"F0.wireOp",EDGE,"E1112"),sQuery(id+"F0.wireOp",EDGE,"E1113"),sQuery(id+"F0.wireOp",EDGE,"E1114"),sQuery(id+"F0.wireOp",EDGE,"E1115"),sQuery(id+"F0.wireOp",EDGE,"E1116"),sQuery(id+"F0.wireOp",EDGE,"E1117"),sQuery(id+"F0.wireOp",EDGE,"E1118"),sQuery(id+"F0.wireOp",EDGE,"E1119"),sQuery(id+"F0.wireOp",EDGE,"E1120"),sQuery(id+"F0.wireOp",EDGE,"E1121"),sQuery(id+"F0.wireOp",EDGE,"E1122"),sQuery(id+"F0.wireOp",EDGE,"E1123"),sQuery(id+"F0.wireOp",EDGE,"E1124"),sQuery(id+"F0.wireOp",EDGE,"E1125"),sQuery(id+"F0.wireOp",EDGE,"E1126"),sQuery(id+"F0.wireOp",EDGE,"E1127"),sQuery(id+"F0.wireOp",EDGE,"E1128"),sQuery(id+"F0.wireOp",EDGE,"E1129"),sQuery(id+"F0.wireOp",EDGE,"E1130"),sQuery(id+"F0.wireOp",EDGE,"E1131"),sQuery(id+"F0.wireOp",EDGE,"E1132"),sQuery(id+"F0.wireOp",EDGE,"E1133"),sQuery(id+"F0.wireOp",EDGE,"E1134"),sQuery(id+"F0.wireOp",EDGE,"E1135"),sQuery(id+"F0.wireOp",EDGE,"E1136"),sQuery(id+"F0.wireOp",EDGE,"E1137"),sQuery(id+"F0.wireOp",EDGE,"E1138"),sQuery(id+"F0.wireOp",EDGE,"E1139"),sQuery(id+"F0.wireOp",EDGE,"E1140"),sQuery(id+"F0.wireOp",EDGE,"E1141"),sQuery(id+"F0.wireOp",EDGE,"E1142"),sQuery(id+"F0.wireOp",EDGE,"E1143"),sQuery(id+"F0.wireOp",EDGE,"E1144"),sQuery(id+"F0.wireOp",EDGE,"E1145"),sQuery(id+"F0.wireOp",EDGE,"E1146"),sQuery(id+"F0.wireOp",EDGE,"E1147"),sQuery(id+"F0.wireOp",EDGE,"E1148"),sQuery(id+"F0.wireOp",EDGE,"E1149"),sQuery(id+"F0.wireOp",EDGE,"E1150"),sQuery(id+"F0.wireOp",EDGE,"E1151"),sQuery(id+"F0.wireOp",EDGE,"E1152"),sQuery(id+"F0.wireOp",EDGE,"E1153"),sQuery(id+"F0.wireOp",EDGE,"E1154"),sQuery(id+"F0.wireOp",EDGE,"E1155"),sQuery(id+"F0.wireOp",EDGE,"E1156"),sQuery(id+"F0.wireOp",EDGE,"E1157"),sQuery(id+"F0.wireOp",EDGE,"E1158"),sQuery(id+"F0.wireOp",EDGE,"E1159"),sQuery(id+"F0.wireOp",EDGE,"E1160"),sQuery(id+"F0.wireOp",EDGE,"E1161"),sQuery(id+"F0.wireOp",EDGE,"E1162"),sQuery(id+"F0.wireOp",EDGE,"E1163"),sQuery(id+"F0.wireOp",EDGE,"E1164"),sQuery(id+"F0.wireOp",EDGE,"E1165"),sQuery(id+"F0.wireOp",EDGE,"E1166"),sQuery(id+"F0.wireOp",EDGE,"E1167"),sQuery(id+"F0.wireOp",EDGE,"E1168"),sQuery(id+"F0.wireOp",EDGE,"E1169"),sQuery(id+"F0.wireOp",EDGE,"E1170"),sQuery(id+"F0.wireOp",EDGE,"E1171"),sQuery(id+"F0.wireOp",EDGE,"E1172"),sQuery(id+"F0.wireOp",EDGE,"E1173"),sQuery(id+"F0.wireOp",EDGE,"E1174"),sQuery(id+"F0.wireOp",EDGE,"E1175"),sQuery(id+"F0.wireOp",EDGE,"E1176"),sQuery(id+"F0.wireOp",EDGE,"E1177"),sQuery(id+"F0.wireOp",EDGE,"E1178"),sQuery(id+"F0.wireOp",EDGE,"E1179"),sQuery(id+"F0.wireOp",EDGE,"E1180"),sQuery(id+"F0.wireOp",EDGE,"E1181"),sQuery(id+"F0.wireOp",EDGE,"E1182"),sQuery(id+"F0.wireOp",EDGE,"E1183"),sQuery(id+"F0.wireOp",EDGE,"E1184"),sQuery(id+"F0.wireOp",EDGE,"E1185"),sQuery(id+"F0.wireOp",EDGE,"E1186"),sQuery(id+"F0.wireOp",EDGE,"E1187"),sQuery(id+"F0.wireOp",EDGE,"E1188"),sQuery(id+"F0.wireOp",EDGE,"E1189"),sQuery(id+"F0.wireOp",EDGE,"E1190"),sQuery(id+"F0.wireOp",EDGE,"E1191"),sQuery(id+"F0.wireOp",EDGE,"E1192"),sQuery(id+"F0.wireOp",EDGE,"E1193"),sQuery(id+"F0.wireOp",EDGE,"E1194"),sQuery(id+"F0.wireOp",EDGE,"E1195"),sQuery(id+"F0.wireOp",EDGE,"E1196"),sQuery(id+"F0.wireOp",EDGE,"E1197"),sQuery(id+"F0.wireOp",EDGE,"E1198"),sQuery(id+"F0.wireOp",EDGE,"E1199"),sQuery(id+"F0.wireOp",EDGE,"E1200"),sQuery(id+"F0.wireOp",EDGE,"E1201"),sQuery(id+"F0.wireOp",EDGE,"E1202"),sQuery(id+"F0.wireOp",EDGE,"E1203"),sQuery(id+"F0.wireOp",EDGE,"E1204"),sQuery(id+"F0.wireOp",EDGE,"E1205"),sQuery(id+"F0.wireOp",EDGE,"E1206"),sQuery(id+"F0.wireOp",EDGE,"E1207"),sQuery(id+"F0.wireOp",EDGE,"E1208"),sQuery(id+"F0.wireOp",EDGE,"E1209"),sQuery(id+"F0.wireOp",EDGE,"E1210"),sQuery(id+"F0.wireOp",EDGE,"E1211"),sQuery(id+"F0.wireOp",EDGE,"E1212"),sQuery(id+"F0.wireOp",EDGE,"E1213"),sQuery(id+"F0.wireOp",EDGE,"E1214"),sQuery(id+"F0.wireOp",EDGE,"E1215"),sQuery(id+"F0.wireOp",EDGE,"E1216"),sQuery(id+"F0.wireOp",EDGE,"E1217"),sQuery(id+"F0.wireOp",EDGE,"E1218"),sQuery(id+"F0.wireOp",EDGE,"E1219"),sQuery(id+"F0.wireOp",EDGE,"E1220"),sQuery(id+"F0.wireOp",EDGE,"E1221"),sQuery(id+"F0.wireOp",EDGE,"E1222"),sQuery(id+"F0.wireOp",EDGE,"E1223"),sQuery(id+"F0.wireOp",EDGE,"E1224"),sQuery(id+"F0.wireOp",EDGE,"E1225"),sQuery(id+"F0.wireOp",EDGE,"E1226"),sQuery(id+"F0.wireOp",EDGE,"E1227"),sQuery(id+"F0.wireOp",EDGE,"E1228"),sQuery(id+"F0.wireOp",EDGE,"E1229"),sQuery(id+"F0.wireOp",EDGE,"E1230"),sQuery(id+"F0.wireOp",EDGE,"E1231"),sQuery(id+"F0.wireOp",EDGE,"E1232"),sQuery(id+"F0.wireOp",EDGE,"E1233"),sQuery(id+"F0.wireOp",EDGE,"E1234"),sQuery(id+"F0.wireOp",EDGE,"E1235"),sQuery(id+"F0.wireOp",EDGE,"E1236"),sQuery(id+"F0.wireOp",EDGE,"E1237"),sQuery(id+"F0.wireOp",EDGE,"E1238"),sQuery(id+"F0.wireOp",EDGE,"E1239"),sQuery(id+"F0.wireOp",EDGE,"E1240"),sQuery(id+"F0.wireOp",EDGE,"E1241"),sQuery(id+"F0.wireOp",EDGE,"E1242"),sQuery(id+"F0.wireOp",EDGE,"E1243"),sQuery(id+"F0.wireOp",EDGE,"E1244"),sQuery(id+"F0.wireOp",EDGE,"E1245"),sQuery(id+"F0.wireOp",EDGE,"E1246"),sQuery(id+"F0.wireOp",EDGE,"E1247"),sQuery(id+"F0.wireOp",EDGE,"E1248"),sQuery(id+"F0.wireOp",EDGE,"E1249"),sQuery(id+"F0.wireOp",EDGE,"E1250"),sQuery(id+"F0.wireOp",EDGE,"E1251"),sQuery(id+"F0.wireOp",EDGE,"E1252"),sQuery(id+"F0.wireOp",EDGE,"E1253"),sQuery(id+"F0.wireOp",EDGE,"E1254"),sQuery(id+"F0.wireOp",EDGE,"E1255"),sQuery(id+"F0.wireOp",EDGE,"E1256"),sQuery(id+"F0.wireOp",EDGE,"E1257"),sQuery(id+"F0.wireOp",EDGE,"E1258"),sQuery(id+"F0.wireOp",EDGE,"E1259"),sQuery(id+"F0.wireOp",EDGE,"E1260"),sQuery(id+"F0.wireOp",EDGE,"E1261"),sQuery(id+"F0.wireOp",EDGE,"E1262"),sQuery(id+"F0.wireOp",EDGE,"E1263"),sQuery(id+"F0.wireOp",EDGE,"E1264"),sQuery(id+"F0.wireOp",EDGE,"E1265"),sQuery(id+"F0.wireOp",EDGE,"E1266"),sQuery(id+"F0.wireOp",EDGE,"E1267"),sQuery(id+"F0.wireOp",EDGE,"E1268"),sQuery(id+"F0.wireOp",EDGE,"E1269"),sQuery(id+"F0.wireOp",EDGE,"E1270"),sQuery(id+"F0.wireOp",EDGE,"E1271"),sQuery(id+"F0.wireOp",EDGE,"E1272"),sQuery(id+"F0.wireOp",EDGE,"E1273"),sQuery(id+"F0.wireOp",EDGE,"E1274"),sQuery(id+"F0.wireOp",EDGE,"E1275"),sQuery(id+"F0.wireOp",EDGE,"E1276"),sQuery(id+"F0.wireOp",EDGE,"E1277"),sQuery(id+"F0.wireOp",EDGE,"E1278"),sQuery(id+"F0.wireOp",EDGE,"E1279"),sQuery(id+"F0.wireOp",EDGE,"E1280"),sQuery(id+"F0.wireOp",EDGE,"E1281"),sQuery(id+"F0.wireOp",EDGE,"E1282"),sQuery(id+"F0.wireOp",EDGE,"E1283"),sQuery(id+"F0.wireOp",EDGE,"E1284"),sQuery(id+"F0.wireOp",EDGE,"E1285"),sQuery(id+"F0.wireOp",EDGE,"E1286"),sQuery(id+"F0.wireOp",EDGE,"E1287"),sQuery(id+"F0.wireOp",EDGE,"E1288"),sQuery(id+"F0.wireOp",EDGE,"E1289"),sQuery(id+"F0.wireOp",EDGE,"E1290"),sQuery(id+"F0.wireOp",EDGE,"E1291"),sQuery(id+"F0.wireOp",EDGE,"E1292"),sQuery(id+"F0.wireOp",EDGE,"E1293"),sQuery(id+"F0.wireOp",EDGE,"E1294"),sQuery(id+"F0.wireOp",EDGE,"E1295"),sQuery(id+"F0.wireOp",EDGE,"E1296"),sQuery(id+"F0.wireOp",EDGE,"E1297"),sQuery(id+"F0.wireOp",EDGE,"E1298"),sQuery(id+"F0.wireOp",EDGE,"E1299"),sQuery(id+"F0.wireOp",EDGE,"E1300"),sQuery(id+"F0.wireOp",EDGE,"E1301"),sQuery(id+"F0.wireOp",EDGE,"E1302"),sQuery(id+"F0.wireOp",EDGE,"E1303"),sQuery(id+"F0.wireOp",EDGE,"E1304"),sQuery(id+"F0.wireOp",EDGE,"E1305"),sQuery(id+"F0.wireOp",EDGE,"E1306"),sQuery(id+"F0.wireOp",EDGE,"E1307"),sQuery(id+"F0.wireOp",EDGE,"E1308"),sQuery(id+"F0.wireOp",EDGE,"E1309"),sQuery(id+"F0.wireOp",EDGE,"E1310"),sQuery(id+"F0.wireOp",EDGE,"E1311"),sQuery(id+"F0.wireOp",EDGE,"E1312"),sQuery(id+"F0.wireOp",EDGE,"E1313"),sQuery(id+"F0.wireOp",EDGE,"E1314"),sQuery(id+"F0.wireOp",EDGE,"E1315"),sQuery(id+"F0.wireOp",EDGE,"E1316"),sQuery(id+"F0.wireOp",EDGE,"E1317"),sQuery(id+"F0.wireOp",EDGE,"E1318"),sQuery(id+"F0.wireOp",EDGE,"E1319"),sQuery(id+"F0.wireOp",EDGE,"E1320"),sQuery(id+"F0.wireOp",EDGE,"E1321"),sQuery(id+"F0.wireOp",EDGE,"E1322"),sQuery(id+"F0.wireOp",EDGE,"E1323"),sQuery(id+"F0.wireOp",EDGE,"E1324"),sQuery(id+"F0.wireOp",EDGE,"E1325"),sQuery(id+"F0.wireOp",EDGE,"E1326"),sQuery(id+"F0.wireOp",EDGE,"E1327"),sQuery(id+"F0.wireOp",EDGE,"E1328"),sQuery(id+"F0.wireOp",EDGE,"E1329"),sQuery(id+"F0.wireOp",EDGE,"E1330"),sQuery(id+"F0.wireOp",EDGE,"E1331"),sQuery(id+"F0.wireOp",EDGE,"E1332"),sQuery(id+"F0.wireOp",EDGE,"E1333"),sQuery(id+"F0.wireOp",EDGE,"E1334"),sQuery(id+"F0.wireOp",EDGE,"E1335"),sQuery(id+"F0.wireOp",EDGE,"E1336"),sQuery(id+"F0.wireOp",EDGE,"E1337"),sQuery(id+"F0.wireOp",EDGE,"E1338"),sQuery(id+"F0.wireOp",EDGE,"E1339"),sQuery(id+"F0.wireOp",EDGE,"E1340"),sQuery(id+"F0.wireOp",EDGE,"E1341"),sQuery(id+"F0.wireOp",EDGE,"E1342"),sQuery(id+"F0.wireOp",EDGE,"E1343"),sQuery(id+"F0.wireOp",EDGE,"E1344"),sQuery(id+"F0.wireOp",EDGE,"E1345"),sQuery(id+"F0.wireOp",EDGE,"E1346"),sQuery(id+"F0.wireOp",EDGE,"E1347"),sQuery(id+"F0.wireOp",EDGE,"E1348"),sQuery(id+"F0.wireOp",EDGE,"E1349"),sQuery(id+"F0.wireOp",EDGE,"E1350"),sQuery(id+"F0.wireOp",EDGE,"E1351"),sQuery(id+"F0.wireOp",EDGE,"E1352"),sQuery(id+"F0.wireOp",EDGE,"E1353"),sQuery(id+"F0.wireOp",EDGE,"E1354"),sQuery(id+"F0.wireOp",EDGE,"E1355"),sQuery(id+"F0.wireOp",EDGE,"E1356"),sQuery(id+"F0.wireOp",EDGE,"E1357"),sQuery(id+"F0.wireOp",EDGE,"E1358"),sQuery(id+"F0.wireOp",EDGE,"E1359"),sQuery(id+"F0.wireOp",EDGE,"E1360"),sQuery(id+"F0.wireOp",EDGE,"E1361"),sQuery(id+"F0.wireOp",EDGE,"E1362"),sQuery(id+"F0.wireOp",EDGE,"E1363"),sQuery(id+"F0.wireOp",EDGE,"E1364"),sQuery(id+"F0.wireOp",EDGE,"E1365"),sQuery(id+"F0.wireOp",EDGE,"E1366"),sQuery(id+"F0.wireOp",EDGE,"E1367"),sQuery(id+"F0.wireOp",EDGE,"E1368"),sQuery(id+"F0.wireOp",EDGE,"E1369"),sQuery(id+"F0.wireOp",EDGE,"E1370"),sQuery(id+"F0.wireOp",EDGE,"E1371"),sQuery(id+"F0.wireOp",EDGE,"E1372"),sQuery(id+"F0.wireOp",EDGE,"E1373"),sQuery(id+"F0.wireOp",EDGE,"E1374"),sQuery(id+"F0.wireOp",EDGE,"E1375"),sQuery(id+"F0.wireOp",EDGE,"E1376"),sQuery(id+"F0.wireOp",EDGE,"E1377"),sQuery(id+"F0.wireOp",EDGE,"E1378"),sQuery(id+"F0.wireOp",EDGE,"E1379"),sQuery(id+"F0.wireOp",EDGE,"E1380"),sQuery(id+"F0.wireOp",EDGE,"E1381"),sQuery(id+"F0.wireOp",EDGE,"E1382"),sQuery(id+"F0.wireOp",EDGE,"E1383"),sQuery(id+"F0.wireOp",EDGE,"E1384"),sQuery(id+"F0.wireOp",EDGE,"E1385"),sQuery(id+"F0.wireOp",EDGE,"E1386"),sQuery(id+"F0.wireOp",EDGE,"E1387"),sQuery(id+"F0.wireOp",EDGE,"E1388"),sQuery(id+"F0.wireOp",EDGE,"E1389"),sQuery(id+"F0.wireOp",EDGE,"E1390"),sQuery(id+"F0.wireOp",EDGE,"E1391"),sQuery(id+"F0.wireOp",EDGE,"E1392"),sQuery(id+"F0.wireOp",EDGE,"E1393"),sQuery(id+"F0.wireOp",EDGE,"E1394"),sQuery(id+"F0.wireOp",EDGE,"E1395"),sQuery(id+"F0.wireOp",EDGE,"E1396"),sQuery(id+"F0.wireOp",EDGE,"E1397"),sQuery(id+"F0.wireOp",EDGE,"E1398"),sQuery(id+"F0.wireOp",EDGE,"E1399"),sQuery(id+"F0.wireOp",EDGE,"E1400"),sQuery(id+"F0.wireOp",EDGE,"E1401"),sQuery(id+"F0.wireOp",EDGE,"E1402"),sQuery(id+"F0.wireOp",EDGE,"E1403"),sQuery(id+"F0.wireOp",EDGE,"E1404"),sQuery(id+"F0.wireOp",EDGE,"E1405"),sQuery(id+"F0.wireOp",EDGE,"E1406"),sQuery(id+"F0.wireOp",EDGE,"E1407"),sQuery(id+"F0.wireOp",EDGE,"E1408"),sQuery(id+"F0.wireOp",EDGE,"E1409"),sQuery(id+"F0.wireOp",EDGE,"E1410"),sQuery(id+"F0.wireOp",EDGE,"E1411"),sQuery(id+"F0.wireOp",EDGE,"E1412"),sQuery(id+"F0.wireOp",EDGE,"E1413"),sQuery(id+"F0.wireOp",EDGE,"E1414"),sQuery(id+"F0.wireOp",EDGE,"E1415"),sQuery(id+"F0.wireOp",EDGE,"E1416"),sQuery(id+"F0.wireOp",EDGE,"E1417"),sQuery(id+"F0.wireOp",EDGE,"E1418"),sQuery(id+"F0.wireOp",EDGE,"E1419"),sQuery(id+"F0.wireOp",EDGE,"E1420"),sQuery(id+"F0.wireOp",EDGE,"E1421"),sQuery(id+"F0.wireOp",EDGE,"E1422"),sQuery(id+"F0.wireOp",EDGE,"E1423"),sQuery(id+"F0.wireOp",EDGE,"E1424"),sQuery(id+"F0.wireOp",EDGE,"E1425"),sQuery(id+"F0.wireOp",EDGE,"E1426"),sQuery(id+"F0.wireOp",EDGE,"E1427"),sQuery(id+"F0.wireOp",EDGE,"E1428"),sQuery(id+"F0.wireOp",EDGE,"E1429"),sQuery(id+"F0.wireOp",EDGE,"E1430"),sQuery(id+"F0.wireOp",EDGE,"E1431"),sQuery(id+"F0.wireOp",EDGE,"E1432"),sQuery(id+"F0.wireOp",EDGE,"E1433"),sQuery(id+"F0.wireOp",EDGE,"E1434"),sQuery(id+"F0.wireOp",EDGE,"E1435"),sQuery(id+"F0.wireOp",EDGE,"E1436"),sQuery(id+"F0.wireOp",EDGE,"E1437"),sQuery(id+"F0.wireOp",EDGE,"E1438"),sQuery(id+"F0.wireOp",EDGE,"E1439"),sQuery(id+"F0.wireOp",EDGE,"E1440"),sQuery(id+"F0.wireOp",EDGE,"E1441"),sQuery(id+"F0.wireOp",EDGE,"E1442"),sQuery(id+"F0.wireOp",EDGE,"E1443"),sQuery(id+"F0.wireOp",EDGE,"E1444"),sQuery(id+"F0.wireOp",EDGE,"E1445"),sQuery(id+"F0.wireOp",EDGE,"E1446"),sQuery(id+"F0.wireOp",EDGE,"E1447"),sQuery(id+"F0.wireOp",EDGE,"E1448"),sQuery(id+"F0.wireOp",EDGE,"E1449"),sQuery(id+"F0.wireOp",EDGE,"E1450"),sQuery(id+"F0.wireOp",EDGE,"E1451"),sQuery(id+"F0.wireOp",EDGE,"E1452"),sQuery(id+"F0.wireOp",EDGE,"E1453"),sQuery(id+"F0.wireOp",EDGE,"E1454"),sQuery(id+"F0.wireOp",EDGE,"E1455"),sQuery(id+"F0.wireOp",EDGE,"E1456"),sQuery(id+"F0.wireOp",EDGE,"E1457"),sQuery(id+"F0.wireOp",EDGE,"E1458"),sQuery(id+"F0.wireOp",EDGE,"E1459"),sQuery(id+"F0.wireOp",EDGE,"E1460"),sQuery(id+"F0.wireOp",EDGE,"E1461"),sQuery(id+"F0.wireOp",EDGE,"E1462"),sQuery(id+"F0.wireOp",EDGE,"E1463"),sQuery(id+"F0.wireOp",EDGE,"E1464"),sQuery(id+"F0.wireOp",EDGE,"E1465"),sQuery(id+"F0.wireOp",EDGE,"E1466"),sQuery(id+"F0.wireOp",EDGE,"E1467"),sQuery(id+"F0.wireOp",EDGE,"E1468"),sQuery(id+"F0.wireOp",EDGE,"E1469"),sQuery(id+"F0.wireOp",EDGE,"E1470"),sQuery(id+"F0.wireOp",EDGE,"E1471"),sQuery(id+"F0.wireOp",EDGE,"E1472"),sQuery(id+"F0.wireOp",EDGE,"E1473"),sQuery(id+"F0.wireOp",EDGE,"E1474"),sQuery(id+"F0.wireOp",EDGE,"E1475"),sQuery(id+"F0.wireOp",EDGE,"E1476"),sQuery(id+"F0.wireOp",EDGE,"E1477"),sQuery(id+"F0.wireOp",EDGE,"E1478"),sQuery(id+"F0.wireOp",EDGE,"E1479"),sQuery(id+"F0.wireOp",EDGE,"E1480"),sQuery(id+"F0.wireOp",EDGE,"E1481"),sQuery(id+"F0.wireOp",EDGE,"E1482"),sQuery(id+"F0.wireOp",EDGE,"E1483"),sQuery(id+"F0.wireOp",EDGE,"E1484"),sQuery(id+"F0.wireOp",EDGE,"E1485"),sQuery(id+"F0.wireOp",EDGE,"E1486"),sQuery(id+"F0.wireOp",EDGE,"E1487"),sQuery(id+"F0.wireOp",EDGE,"E1488"),sQuery(id+"F0.wireOp",EDGE,"E1489"),sQuery(id+"F0.wireOp",EDGE,"E1490"),sQuery(id+"F0.wireOp",EDGE,"E1491"),sQuery(id+"F0.wireOp",EDGE,"E1492"),sQuery(id+"F0.wireOp",EDGE,"E1493"),sQuery(id+"F0.wireOp",EDGE,"E1494"),sQuery(id+"F0.wireOp",EDGE,"E1495"),sQuery(id+"F0.wireOp",EDGE,"E1496"),sQuery(id+"F0.wireOp",EDGE,"E1497"),sQuery(id+"F0.wireOp",EDGE,"E1498"),sQuery(id+"F0.wireOp",EDGE,"E1499"),sQuery(id+"F0.wireOp",EDGE,"E1500"),sQuery(id+"F0.wireOp",EDGE,"E1501"),sQuery(id+"F0.wireOp",EDGE,"E1502"),sQuery(id+"F0.wireOp",EDGE,"E1503"),sQuery(id+"F0.wireOp",EDGE,"E1504"),sQuery(id+"F0.wireOp",EDGE,"E1505"),sQuery(id+"F0.wireOp",EDGE,"E1506"),sQuery(id+"F0.wireOp",EDGE,"E1507"),sQuery(id+"F0.wireOp",EDGE,"E1508"),sQuery(id+"F0.wireOp",EDGE,"E1509"),sQuery(id+"F0.wireOp",EDGE,"E1510"),sQuery(id+"F0.wireOp",EDGE,"E1511"),sQuery(id+"F0.wireOp",EDGE,"E1512"),sQuery(id+"F0.wireOp",EDGE,"E1513"),sQuery(id+"F0.wireOp",EDGE,"E1514"),sQuery(id+"F0.wireOp",EDGE,"E1515"),sQuery(id+"F0.wireOp",EDGE,"E1516"),sQuery(id+"F0.wireOp",EDGE,"E1517"),sQuery(id+"F0.wireOp",EDGE,"E1518"),sQuery(id+"F0.wireOp",EDGE,"E1519"),sQuery(id+"F0.wireOp",EDGE,"E1520"),sQuery(id+"F0.wireOp",EDGE,"E1521"),sQuery(id+"F0.wireOp",EDGE,"E1522"),sQuery(id+"F0.wireOp",EDGE,"E1523"),sQuery(id+"F0.wireOp",EDGE,"E1524"),sQuery(id+"F0.wireOp",EDGE,"E1525"),sQuery(id+"F0.wireOp",EDGE,"E1526"),sQuery(id+"F0.wireOp",EDGE,"E1527"),sQuery(id+"F0.wireOp",EDGE,"E1528"),sQuery(id+"F0.wireOp",EDGE,"E1529"),sQuery(id+"F0.wireOp",EDGE,"E1530"),sQuery(id+"F0.wireOp",EDGE,"E1531"),sQuery(id+"F0.wireOp",EDGE,"E1532"),sQuery(id+"F0.wireOp",EDGE,"E1533"),sQuery(id+"F0.wireOp",EDGE,"E1534"),sQuery(id+"F0.wireOp",EDGE,"E1535"),sQuery(id+"F0.wireOp",EDGE,"E1536"),sQuery(id+"F0.wireOp",EDGE,"E1537"),sQuery(id+"F0.wireOp",EDGE,"E1538"),sQuery(id+"F0.wireOp",EDGE,"E1539"),sQuery(id+"F0.wireOp",EDGE,"E1540"),sQuery(id+"F0.wireOp",EDGE,"E1541"),sQuery(id+"F0.wireOp",EDGE,"E1542"),sQuery(id+"F0.wireOp",EDGE,"E1543"),sQuery(id+"F0.wireOp",EDGE,"E1544"),sQuery(id+"F0.wireOp",EDGE,"E1545"),sQuery(id+"F0.wireOp",EDGE,"E1546"),sQuery(id+"F0.wireOp",EDGE,"E1547"),sQuery(id+"F0.wireOp",EDGE,"E1548"),sQuery(id+"F0.wireOp",EDGE,"E1549"),sQuery(id+"F0.wireOp",EDGE,"E1550"),sQuery(id+"F0.wireOp",EDGE,"E1551"),sQuery(id+"F0.wireOp",EDGE,"E1552"),sQuery(id+"F0.wireOp",EDGE,"E1553"),sQuery(id+"F0.wireOp",EDGE,"E1554"),sQuery(id+"F0.wireOp",EDGE,"E1555"),sQuery(id+"F0.wireOp",EDGE,"E1556"),sQuery(id+"F0.wireOp",EDGE,"E1557"),sQuery(id+"F0.wireOp",EDGE,"E1558"),sQuery(id+"F0.wireOp",EDGE,"E1559"),sQuery(id+"F0.wireOp",EDGE,"E1560"),sQuery(id+"F0.wireOp",EDGE,"E1561"),sQuery(id+"F0.wireOp",EDGE,"E1562"),sQuery(id+"F0.wireOp",EDGE,"E1563"),sQuery(id+"F0.wireOp",EDGE,"E1564"),sQuery(id+"F0.wireOp",EDGE,"E1565"),sQuery(id+"F0.wireOp",EDGE,"E1566"),sQuery(id+"F0.wireOp",EDGE,"E1567"),sQuery(id+"F0.wireOp",EDGE,"E1568"),sQuery(id+"F0.wireOp",EDGE,"E1569"),sQuery(id+"F0.wireOp",EDGE,"E1570"),sQuery(id+"F0.wireOp",EDGE,"E1571"),sQuery(id+"F0.wireOp",EDGE,"E1572"),sQuery(id+"F0.wireOp",EDGE,"E1573"),sQuery(id+"F0.wireOp",EDGE,"E1574"),sQuery(id+"F0.wireOp",EDGE,"E1575"),sQuery(id+"F0.wireOp",EDGE,"E1576"),sQuery(id+"F0.wireOp",EDGE,"E1577"),sQuery(id+"F0.wireOp",EDGE,"E1578"),sQuery(id+"F0.wireOp",EDGE,"E1579"),sQuery(id+"F0.wireOp",EDGE,"E1580"),sQuery(id+"F0.wireOp",EDGE,"E1581"),sQuery(id+"F0.wireOp",EDGE,"E1582"),sQuery(id+"F0.wireOp",EDGE,"E1583"),sQuery(id+"F0.wireOp",EDGE,"E1584"),sQuery(id+"F0.wireOp",EDGE,"E1585"),sQuery(id+"F0.wireOp",EDGE,"E1586"),sQuery(id+"F0.wireOp",EDGE,"E1587"),sQuery(id+"F0.wireOp",EDGE,"E1588"),sQuery(id+"F0.wireOp",EDGE,"E1589"),sQuery(id+"F0.wireOp",EDGE,"E1590"),sQuery(id+"F0.wireOp",EDGE,"E1591"),sQuery(id+"F0.wireOp",EDGE,"E1592"),sQuery(id+"F0.wireOp",EDGE,"E1593"),sQuery(id+"F0.wireOp",EDGE,"E1594"),sQuery(id+"F0.wireOp",EDGE,"E1595"),sQuery(id+"F0.wireOp",EDGE,"E1596"),sQuery(id+"F0.wireOp",EDGE,"E1597"),sQuery(id+"F0.wireOp",EDGE,"E1598"),sQuery(id+"F0.wireOp",EDGE,"E1599"),sQuery(id+"F0.wireOp",EDGE,"E1600"),sQuery(id+"F0.wireOp",EDGE,"E1601"),sQuery(id+"F0.wireOp",EDGE,"E1602"),sQuery(id+"F0.wireOp",EDGE,"E1603"),sQuery(id+"F0.wireOp",EDGE,"E1604"),sQuery(id+"F0.wireOp",EDGE,"E1605"),sQuery(id+"F0.wireOp",EDGE,"E1606"),sQuery(id+"F0.wireOp",EDGE,"E1607"),sQuery(id+"F0.wireOp",EDGE,"E1608"),sQuery(id+"F0.wireOp",EDGE,"E1609"),sQuery(id+"F0.wireOp",EDGE,"E1610"),sQuery(id+"F0.wireOp",EDGE,"E1611"),sQuery(id+"F0.wireOp",EDGE,"E1612"),sQuery(id+"F0.wireOp",EDGE,"E1613"),sQuery(id+"F0.wireOp",EDGE,"E1614"),sQuery(id+"F0.wireOp",EDGE,"E1615"),sQuery(id+"F0.wireOp",EDGE,"E1616"),sQuery(id+"F0.wireOp",EDGE,"E1617"),sQuery(id+"F0.wireOp",EDGE,"E1618"),sQuery(id+"F0.wireOp",EDGE,"E1619"),sQuery(id+"F0.wireOp",EDGE,"E1620"),sQuery(id+"F0.wireOp",EDGE,"E1621"),sQuery(id+"F0.wireOp",EDGE,"E1622"),sQuery(id+"F0.wireOp",EDGE,"E1623"),sQuery(id+"F0.wireOp",EDGE,"E1624"),sQuery(id+"F0.wireOp",EDGE,"E1625"),sQuery(id+"F0.wireOp",EDGE,"E1626"),sQuery(id+"F0.wireOp",EDGE,"E1627"),sQuery(id+"F0.wireOp",EDGE,"E1628"),sQuery(id+"F0.wireOp",EDGE,"E1629"),sQuery(id+"F0.wireOp",EDGE,"E1630"),sQuery(id+"F0.wireOp",EDGE,"E1631"),sQuery(id+"F0.wireOp",EDGE,"E1632"),sQuery(id+"F0.wireOp",EDGE,"E1633"),sQuery(id+"F0.wireOp",EDGE,"E1634"),sQuery(id+"F0.wireOp",EDGE,"E1635"),sQuery(id+"F0.wireOp",EDGE,"E1636"),sQuery(id+"F0.wireOp",EDGE,"E1637"),sQuery(id+"F0.wireOp",EDGE,"E1640")])],"isStart":false});
            extrude(context, id + "F3", {"entities" : qUnion([Q0]), "operationType" : NewBodyOperationType.REMOVE, "endBound" : BoundingType.UP_TO_SURFACE, "oppositeDirection" : true, "depth" : 25 * mm, "endBoundEntityFace" : qUnion([Q1]), "offsetDistance" : 25 * mm});
        }
    });
